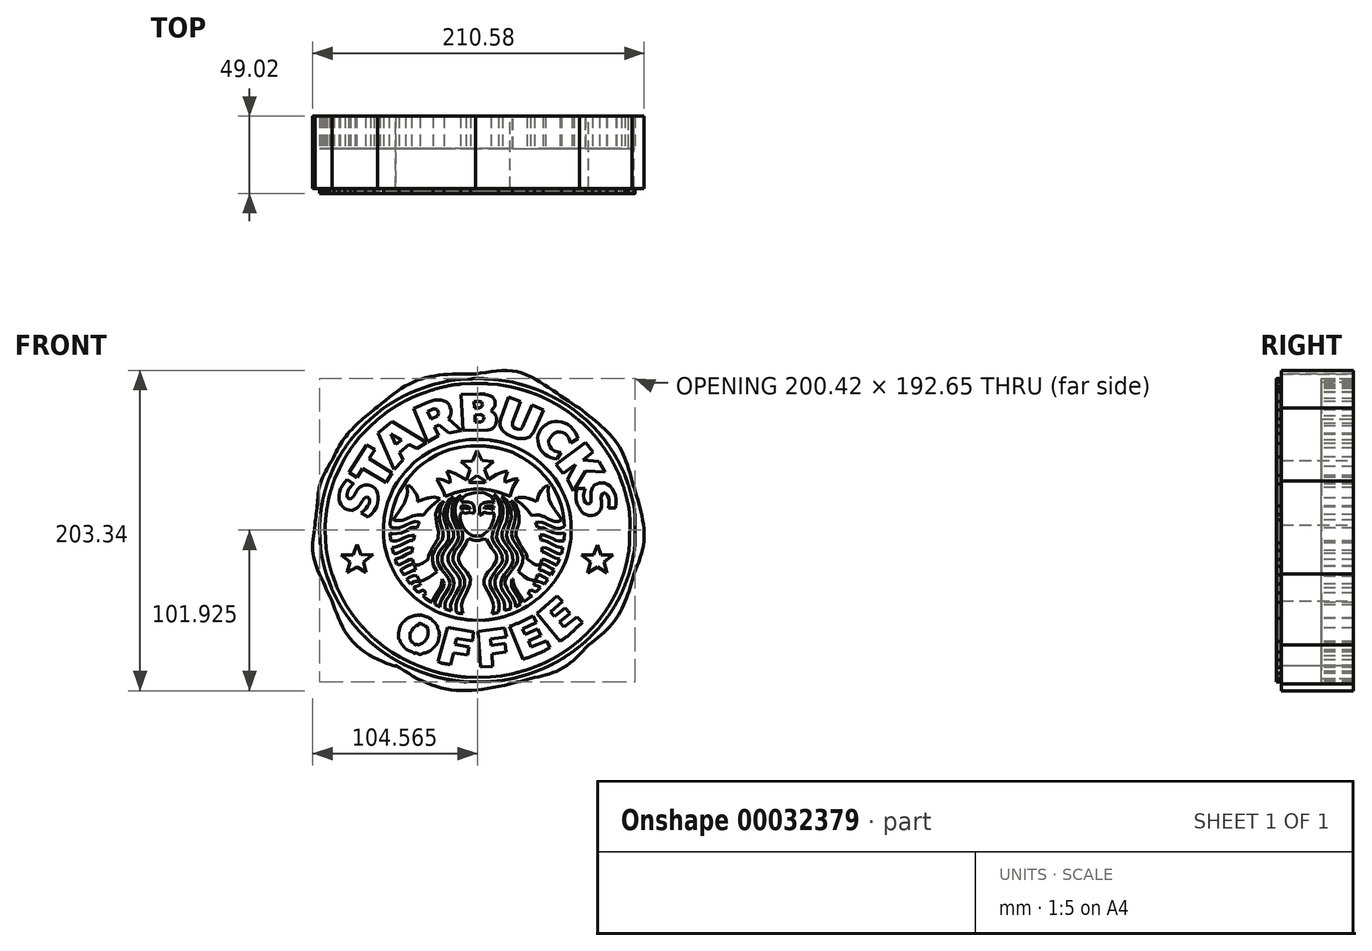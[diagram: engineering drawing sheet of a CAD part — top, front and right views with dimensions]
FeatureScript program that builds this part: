
annotation { "Feature Type Name" : "Feature", "Feature Type Description" : "" }
export const myFeature = defineFeature(function(context is Context, id is Id, definition is map)
    precondition{}
    {
        {
            var Q0;
            Q0=qCreatedBy(makeId("Front.planeOp"),FACE);
            var sketch = newSketch(context, id + "F0", { "sketchPlane" : qUnion([Q0])});
            skFitSpline(sketch, "E0", {"points": [v(-1.26, 99.12) * mm, v(25.57, 100.63) * mm, v(47.78, 88.94) * mm, v(64.86, 77.55) * mm]});
            skFitSpline(sketch, "E1", {"points": [v(64.86, 77.55) * mm, v(80.4, 64.67) * mm, v(91.74, 50.25) * mm, v(98.22, 31.18) * mm]});
            skFitSpline(sketch, "E2", {"points": [v(98.22, 31.18) * mm, v(103.53, 13.35) * mm, v(105.81, -7.15) * mm, v(99.43, -27.68) * mm]});
            skFitSpline(sketch, "E3", {"points": [v(99.43, -27.68) * mm, v(94.37, -44) * mm, v(85.73, -59.44) * mm, v(70.7, -72.73) * mm]});
            skFitSpline(sketch, "E4", {"points": [v(70.7, -72.73) * mm, v(54.04, -87.63) * mm, v(36.86, -93.5) * mm, v(20.71, -97.63) * mm]});
            skFitSpline(sketch, "E5", {"points": [v(20.71, -97.63) * mm, v(-7.45, -101.86) * mm, v(-30.33, -97.78) * mm, v(-51.96, -85.74) * mm]});
            skFitSpline(sketch, "E6", {"points": [v(-51.96, -85.74) * mm, v(-52.06, -86.04) * mm, v(-74.8, -74.8) * mm, v(-92.18, -45.02) * mm]});
            skFitSpline(sketch, "E7", {"points": [v(-92.18, -45.02) * mm, v(-99.16, -30.2) * mm, v(-104.3, -14.84) * mm, v(-103.16, 3.47) * mm]});
            skFitSpline(sketch, "E8", {"points": [v(-103.16, 3.47) * mm, v(-101.66, 16.33) * mm, v(-99.76, 29.6) * mm, v(-92.28, 44.39) * mm]});
            skFitSpline(sketch, "E9", {"points": [v(-92.28, 44.39) * mm, v(-85.03, 57.64) * mm, v(-75.05, 68.69) * mm, v(-63.25, 78.46) * mm]});
            skFitSpline(sketch, "E10", {"points": [v(-63.25, 78.46) * mm, v(-42.92, 93.13) * mm, v(-22.97, 98.67) * mm, v(-1.26, 99.12) * mm]});
            skFitSpline(sketch, "E11", {"points": [v(52.4, -70.46) * mm, v(57.54, -67.03) * mm, v(62.11, -62.8) * mm, v(66.78, -58.62) * mm]});
            skLineSegment(sketch, "E12", {"start": v(38.05, -52.88) * mm, "end": v(52.4, -70.46) * mm});
            skLineSegment(sketch, "E13", {"start": v(52.4, -70.46) * mm, "end": v(38.05, -52.88) * mm});
            skFitSpline(sketch, "E14", {"points": [v(20.45, -61.17) * mm, v(25.51, -59.1) * mm, v(30.46, -56.86) * mm, v(35.24, -54.33) * mm]});
            skLineSegment(sketch, "E15", {"start": v(66.78, -58.62) * mm, "end": v(63.35, -55) * mm});
            skLineSegment(sketch, "E16", {"start": v(63.35, -55) * mm, "end": v(55.18, -61.45) * mm});
            skLineSegment(sketch, "E17", {"start": v(55.18, -61.45) * mm, "end": v(52.36, -58.22) * mm});
            skLineSegment(sketch, "E18", {"start": v(52.36, -58.22) * mm, "end": v(59.01, -52.78) * mm});
            skLineSegment(sketch, "E19", {"start": v(59.01, -52.78) * mm, "end": v(55.81, -49.27) * mm});
            skLineSegment(sketch, "E20", {"start": v(55.81, -49.27) * mm, "end": v(49.02, -54.8) * mm});
            skLineSegment(sketch, "E21", {"start": v(49.02, -54.8) * mm, "end": v(46.52, -51.77) * mm});
            skLineSegment(sketch, "E22", {"start": v(46.52, -51.77) * mm, "end": v(54.09, -45.04) * mm});
            skLineSegment(sketch, "E23", {"start": v(54.09, -45.04) * mm, "end": v(50.65, -41.84) * mm});
            skLineSegment(sketch, "E24", {"start": v(50.65, -41.84) * mm, "end": v(38.05, -52.88) * mm});
            skLineSegment(sketch, "E25", {"start": v(38.05, -52.88) * mm, "end": v(66.78, -58.62) * mm});
            skFitSpline(sketch, "E26", {"points": [v(46.18, -74.46) * mm, v(40.49, -77.49) * mm, v(34.71, -79.84) * mm, v(28.93, -82.12) * mm]});
            skLineSegment(sketch, "E27", {"start": v(35.24, -54.33) * mm, "end": v(35.7, -54.4) * mm});
            skLineSegment(sketch, "E28", {"start": v(35.7, -54.4) * mm, "end": v(37.84, -57.92) * mm});
            skLineSegment(sketch, "E29", {"start": v(37.84, -57.92) * mm, "end": v(37.88, -58.25) * mm});
            skLineSegment(sketch, "E30", {"start": v(37.88, -58.25) * mm, "end": v(28.72, -62.63) * mm});
            skLineSegment(sketch, "E31", {"start": v(28.72, -62.63) * mm, "end": v(30.32, -66.05) * mm});
            skLineSegment(sketch, "E32", {"start": v(30.32, -66.05) * mm, "end": v(38.37, -62.6) * mm});
            skLineSegment(sketch, "E33", {"start": v(38.37, -62.6) * mm, "end": v(40.58, -66.8) * mm});
            skLineSegment(sketch, "E34", {"start": v(40.58, -66.8) * mm, "end": v(32.57, -70.3) * mm});
            skLineSegment(sketch, "E35", {"start": v(32.57, -70.3) * mm, "end": v(34.2, -74.21) * mm});
            skLineSegment(sketch, "E36", {"start": v(34.2, -74.21) * mm, "end": v(43.86, -70.18) * mm});
            skLineSegment(sketch, "E37", {"start": v(43.86, -70.18) * mm, "end": v(46.18, -74.46) * mm});
            skLineSegment(sketch, "E38", {"start": v(46.18, -74.46) * mm, "end": v(35.24, -54.33) * mm});
            skLineSegment(sketch, "E39", {"start": v(28.93, -82.12) * mm, "end": v(20.45, -61.17) * mm});
            skLineSegment(sketch, "E40", {"start": v(20.45, -61.17) * mm, "end": v(28.93, -82.12) * mm});
            skLineSegment(sketch, "E41", {"start": v(0.5, -64.16) * mm, "end": v(17.31, -62.17) * mm});
            skLineSegment(sketch, "E42", {"start": v(17.31, -62.17) * mm, "end": v(18.42, -67.69) * mm});
            skLineSegment(sketch, "E43", {"start": v(18.42, -67.69) * mm, "end": v(8.37, -69.15) * mm});
            skLineSegment(sketch, "E44", {"start": v(8.37, -69.15) * mm, "end": v(8.62, -73.03) * mm});
            skLineSegment(sketch, "E45", {"start": v(8.62, -73.03) * mm, "end": v(17.5, -71.9) * mm});
            skLineSegment(sketch, "E46", {"start": v(17.5, -71.9) * mm, "end": v(18.28, -77.24) * mm});
            skLineSegment(sketch, "E47", {"start": v(18.28, -77.24) * mm, "end": v(9.3, -78.42) * mm});
            skLineSegment(sketch, "E48", {"start": v(9.3, -78.42) * mm, "end": v(9.69, -86.4) * mm});
            skLineSegment(sketch, "E49", {"start": v(9.69, -86.4) * mm, "end": v(1.95, -86.75) * mm});
            skLineSegment(sketch, "E50", {"start": v(1.95, -86.75) * mm, "end": v(0.5, -64.16) * mm});
            skFitSpline(sketch, "E51", {"points": [v(-17.11, -85.44) * mm, v(-19.73, -84.85) * mm, v(-22.4, -84.38) * mm, v(-24.84, -83.44) * mm]});
            skLineSegment(sketch, "E52", {"start": v(-19.07, -61.56) * mm, "end": v(-2.32, -64.52) * mm});
            skLineSegment(sketch, "E53", {"start": v(-2.32, -64.52) * mm, "end": v(-3, -70.15) * mm});
            skLineSegment(sketch, "E54", {"start": v(-3, -70.15) * mm, "end": v(-13.23, -68.54) * mm});
            skLineSegment(sketch, "E55", {"start": v(-13.23, -68.54) * mm, "end": v(-14.08, -72.36) * mm});
            skLineSegment(sketch, "E56", {"start": v(-14.08, -72.36) * mm, "end": v(-5.28, -74.03) * mm});
            skLineSegment(sketch, "E57", {"start": v(-5.28, -74.03) * mm, "end": v(-6.17, -79.3) * mm});
            skLineSegment(sketch, "E58", {"start": v(-6.17, -79.3) * mm, "end": v(-15.08, -77.85) * mm});
            skLineSegment(sketch, "E59", {"start": v(-15.08, -77.85) * mm, "end": v(-17.11, -85.44) * mm});
            skLineSegment(sketch, "E60", {"start": v(-17.11, -85.44) * mm, "end": v(-19.07, -61.56) * mm});
            skFitSpline(sketch, "E61", {"points": [v(-38.45, -60.39) * mm, v(-38.66, -60.44) * mm, v(-40.27, -61.92) * mm, v(-40.32, -61.95) * mm]});
            skFitSpline(sketch, "E62", {"points": [v(-40.32, -61.95) * mm, v(-41.1, -62.57) * mm, v(-41.43, -63.51) * mm, v(-41.93, -64.37) * mm]});
            skFitSpline(sketch, "E63", {"points": [v(-41.93, -64.37) * mm, v(-42.79, -65.33) * mm, v(-42.74, -67) * mm, v(-42.69, -67.24) * mm]});
            skFitSpline(sketch, "E64", {"points": [v(-42.69, -67.24) * mm, v(-42.84, -68.64) * mm, v(-42.48, -69.28) * mm, v(-42.13, -70.06) * mm]});
            skFitSpline(sketch, "E65", {"points": [v(-42.13, -70.06) * mm, v(-41.65, -71.05) * mm, v(-40.74, -71.42) * mm, v(-40.22, -71.93) * mm]});
            skFitSpline(sketch, "E66", {"points": [v(-40.22, -71.93) * mm, v(-39.51, -72.72) * mm, v(-38.54, -72.43) * mm, v(-37.7, -72.68) * mm]});
            skFitSpline(sketch, "E67", {"points": [v(-37.7, -72.68) * mm, v(-36.96, -72.71) * mm, v(-36.14, -72.2) * mm, v(-35.58, -72.03) * mm]});
            skFitSpline(sketch, "E68", {"points": [v(-35.58, -72.03) * mm, v(-34.78, -71.65) * mm, v(-34.2, -71.06) * mm, v(-33.72, -70.72) * mm]});
            skFitSpline(sketch, "E69", {"points": [v(-33.72, -70.72) * mm, v(-32.97, -70.05) * mm, v(-32.64, -69.49) * mm, v(-32.46, -68.95) * mm]});
            skFitSpline(sketch, "E70", {"points": [v(-32.46, -68.95) * mm, v(-31.88, -68.29) * mm, v(-31.53, -67.38) * mm, v(-31.55, -67.14) * mm]});
            skFitSpline(sketch, "E71", {"points": [v(-31.55, -67.14) * mm, v(-31.25, -66.05) * mm, v(-31.24, -65.55) * mm, v(-31.3, -65.02) * mm]});
            skFitSpline(sketch, "E72", {"points": [v(-31.3, -65.02) * mm, v(-31.23, -64.28) * mm, v(-31.25, -63.34) * mm, v(-31.65, -62.86) * mm]});
            skFitSpline(sketch, "E73", {"points": [v(-31.65, -62.86) * mm, v(-31.9, -61.3) * mm, v(-33.05, -61.03) * mm, v(-33.56, -60.29) * mm]});
            skFitSpline(sketch, "E74", {"points": [v(-33.56, -60.29) * mm, v(-37.32, -59.31) * mm, v(-37.4, -60.37) * mm, v(-38.45, -60.39) * mm]});
            skLineSegment(sketch, "E75", {"start": v(-24.84, -83.44) * mm, "end": v(-19.07, -61.56) * mm});
            skLineSegment(sketch, "E76", {"start": v(-19.07, -61.56) * mm, "end": v(-24.84, -83.44) * mm});
            skFitSpline(sketch, "E77", {"points": [v(-40.82, -54.4) * mm, v(-41.9, -54.84) * mm, v(-42.77, -55.18) * mm, v(-43.8, -55.6) * mm]});
            skFitSpline(sketch, "E78", {"points": [v(-43.8, -55.6) * mm, v(-45, -56.3) * mm, v(-46.1, -57.47) * mm, v(-46.82, -58.07) * mm]});
            skFitSpline(sketch, "E79", {"points": [v(-46.82, -58.07) * mm, v(-47.5, -58.83) * mm, v(-48.6, -60.24) * mm, v(-48.88, -60.94) * mm]});
            skFitSpline(sketch, "E80", {"points": [v(-48.88, -60.94) * mm, v(-49.27, -61.9) * mm, v(-49.49, -62.95) * mm, v(-49.8, -63.97) * mm]});
            skFitSpline(sketch, "E81", {"points": [v(-49.8, -63.97) * mm, v(-49.92, -65.1) * mm, v(-49.98, -66.5) * mm, v(-49.94, -67.4) * mm]});
            skFitSpline(sketch, "E82", {"points": [v(-49.94, -67.4) * mm, v(-49.9, -68.95) * mm, v(-49.08, -69.92) * mm, v(-48.94, -70.92) * mm]});
            skFitSpline(sketch, "E83", {"points": [v(-48.94, -70.92) * mm, v(-48.3, -71.81) * mm, v(-47.7, -72.68) * mm, v(-47.22, -73.34) * mm]});
            skFitSpline(sketch, "E84", {"points": [v(-47.22, -73.34) * mm, v(-46.55, -74.1) * mm, v(-45.9, -74.77) * mm, v(-45.4, -75.3) * mm]});
            skFitSpline(sketch, "E85", {"points": [v(-45.4, -75.3) * mm, v(-43.93, -76.31) * mm, v(-42.53, -76.76) * mm, v(-41.02, -77.52) * mm]});
            skFitSpline(sketch, "E86", {"points": [v(-41.02, -77.52) * mm, v(-40.01, -78.08) * mm, v(-38.95, -78) * mm, v(-37.75, -78.28) * mm]});
            skFitSpline(sketch, "E87", {"points": [v(-37.75, -78.28) * mm, v(-36.4, -78.91) * mm, v(-34.56, -78.12) * mm, v(-33.72, -78.08) * mm]});
            skFitSpline(sketch, "E88", {"points": [v(-33.72, -78.08) * mm, v(-32.56, -77.77) * mm, v(-31.8, -77.38) * mm, v(-30.94, -77.07) * mm]});
            skFitSpline(sketch, "E89", {"points": [v(-30.94, -77.07) * mm, v(-29.98, -76.62) * mm, v(-29.2, -75.89) * mm, v(-28.63, -75.5) * mm]});
            skFitSpline(sketch, "E90", {"points": [v(-28.63, -75.5) * mm, v(-27.98, -74.72) * mm, v(-27.24, -73.97) * mm, v(-26.76, -73.44) * mm]});
            skFitSpline(sketch, "E91", {"points": [v(-26.76, -73.44) * mm, v(-26.1, -72.9) * mm, v(-25.75, -72.15) * mm, v(-25.35, -71.63) * mm]});
            skFitSpline(sketch, "E92", {"points": [v(-25.35, -71.63) * mm, v(-24.81, -70.53) * mm, v(-24.74, -69.25) * mm, v(-24.3, -68) * mm]});
            skFitSpline(sketch, "E93", {"points": [v(-24.3, -68) * mm, v(-24.4, -67.23) * mm, v(-23.8, -66.52) * mm, v(-24.3, -66.03) * mm]});
            skFitSpline(sketch, "E94", {"points": [v(-24.3, -66.03) * mm, v(-24.2, -64.6) * mm, v(-25.09, -62.38) * mm, v(-25.3, -60.94) * mm]});
            skFitSpline(sketch, "E95", {"points": [v(-25.3, -60.94) * mm, v(-25.47, -60.75) * mm, v(-26.52, -59.13) * mm, v(-27.16, -58.77) * mm]});
            skFitSpline(sketch, "E96", {"points": [v(-27.16, -58.77) * mm, v(-27.55, -57.95) * mm, v(-28.33, -57.67) * mm, v(-28.73, -57.21) * mm]});
            skFitSpline(sketch, "E97", {"points": [v(-28.73, -57.21) * mm, v(-29.65, -56.02) * mm, v(-30.05, -56.1) * mm, v(-30.74, -55.7) * mm]});
            skFitSpline(sketch, "E98", {"points": [v(-30.74, -55.7) * mm, v(-31.3, -55.06) * mm, v(-32.3, -55.05) * mm, v(-32.86, -54.7) * mm]});
            skFitSpline(sketch, "E99", {"points": [v(-32.86, -54.7) * mm, v(-33.62, -54.55) * mm, v(-34.3, -54.25) * mm, v(-35.13, -54.19) * mm]});
            skFitSpline(sketch, "E100", {"points": [v(-35.13, -54.19) * mm, v(-35.74, -53.8) * mm, v(-36.82, -54.04) * mm, v(-37.5, -53.79) * mm]});
            skFitSpline(sketch, "E101", {"points": [v(-37.5, -53.79) * mm, v(-38.92, -54.07) * mm, v(-39.58, -54.16) * mm, v(-40.82, -54.4) * mm]});
            skFitSpline(sketch, "E102", {"points": [v(-42.74, -51.32) * mm, v(-44.4, -52.08) * mm, v(-45.55, -52.66) * mm, v(-47.02, -53.38) * mm]});
            skFitSpline(sketch, "E103", {"points": [v(-47.02, -53.38) * mm, v(-47.94, -50.58) * mm, v(-49, -49.5) * mm, v(-50.65, -48.4) * mm]});
            skFitSpline(sketch, "E104", {"points": [v(-50.65, -48.4) * mm, v(-51.34, -47.59) * mm, v(-52.03, -47.77) * mm, v(-52.77, -47.44) * mm]});
            skFitSpline(sketch, "E105", {"points": [v(-52.77, -47.44) * mm, v(-53.56, -47.2) * mm, v(-54.37, -47.6) * mm, v(-55.23, -47.54) * mm]});
            skFitSpline(sketch, "E106", {"points": [v(-55.23, -47.54) * mm, v(-57.59, -48.17) * mm, v(-58.26, -49.4) * mm, v(-59.52, -50.26) * mm]});
            skFitSpline(sketch, "E107", {"points": [v(-59.52, -50.26) * mm, v(-61.02, -52.3) * mm, v(-60.88, -54.45) * mm, v(-60.07, -56.76) * mm]});
            skFitSpline(sketch, "E108", {"points": [v(-60.07, -56.76) * mm, v(-58.02, -60.05) * mm, v(-56.12, -59.45) * mm, v(-52.87, -60.44) * mm]});
            skFitSpline(sketch, "E109", {"points": [v(-54.63, -64.62) * mm, v(-54.02, -63.49) * mm, v(-52.8, -62.16) * mm, v(-52.41, -60.49) * mm]});
            skFitSpline(sketch, "E110", {"points": [v(-52.41, -60.49) * mm, v(-52.7, -60.51) * mm, v(-52.75, -60.4) * mm, v(-52.97, -60.34) * mm]});
            skLineSegment(sketch, "E111", {"start": v(-54.58, -64.82) * mm, "end": v(-54.58, -64.87) * mm});
            skFitSpline(sketch, "E112", {"points": [v(-57.35, -64.62) * mm, v(-59.72, -64.06) * mm, v(-61.79, -62.53) * mm, v(-63.6, -61.7) * mm]});
            skFitSpline(sketch, "E113", {"points": [v(-63.6, -61.7) * mm, v(-65.22, -60.15) * mm, v(-66.07, -58.44) * mm, v(-67.08, -56.96) * mm]});
            skFitSpline(sketch, "E114", {"points": [v(-67.08, -56.96) * mm, v(-67.51, -55.42) * mm, v(-67.7, -53.78) * mm, v(-67.73, -52.22) * mm]});
            skFitSpline(sketch, "E115", {"points": [v(-67.73, -52.22) * mm, v(-68.14, -50.5) * mm, v(-66.5, -46.73) * mm, v(-66.57, -47.39) * mm]});
            skFitSpline(sketch, "E116", {"points": [v(-66.57, -47.39) * mm, v(-65.76, -45.58) * mm, v(-64.45, -44.13) * mm, v(-62.9, -43.05) * mm]});
            skFitSpline(sketch, "E117", {"points": [v(-62.9, -43.05) * mm, v(-61.36, -41.63) * mm, v(-59.65, -41.36) * mm, v(-57.6, -40.93) * mm]});
            skFitSpline(sketch, "E118", {"points": [v(-57.6, -40.93) * mm, v(-55.6, -40.78) * mm, v(-53.72, -41.12) * mm, v(-51.9, -41.29) * mm]});
            skFitSpline(sketch, "E119", {"points": [v(-51.9, -41.29) * mm, v(-50.48, -41.91) * mm, v(-48.93, -42.81) * mm, v(-47.68, -43.45) * mm]});
            skFitSpline(sketch, "E120", {"points": [v(-47.68, -43.45) * mm, v(-45.8, -44.76) * mm, v(-44.8, -46.06) * mm, v(-44.15, -47.54) * mm]});
            skFitSpline(sketch, "E121", {"points": [v(-44.15, -47.54) * mm, v(-42.6, -48.51) * mm, v(-42.87, -51.05) * mm, v(-42.48, -51.16) * mm]});
            skFitSpline(sketch, "E122", {"points": [v(-81.34, 36.63) * mm, v(-77.63, 42.83) * mm, v(-73.92, 48.68) * mm, v(-70.2, 54.21) * mm]});
            skLineSegment(sketch, "E123", {"start": v(-54.58, -64.72) * mm, "end": v(-57.35, -64.62) * mm});
            skLineSegment(sketch, "E124", {"start": v(-70.2, 54.21) * mm, "end": v(-65.06, 51.3) * mm});
            skLineSegment(sketch, "E125", {"start": v(-65.06, 51.3) * mm, "end": v(-68.64, 45.55) * mm});
            skLineSegment(sketch, "E126", {"start": v(-68.64, 45.55) * mm, "end": v(-54.18, 36.42) * mm});
            skLineSegment(sketch, "E127", {"start": v(-54.18, 36.42) * mm, "end": v(-58.06, 30.33) * mm});
            skLineSegment(sketch, "E128", {"start": v(-58.06, 30.33) * mm, "end": v(-72.82, 39.25) * mm});
            skLineSegment(sketch, "E129", {"start": v(-72.82, 39.25) * mm, "end": v(-76.45, 33.65) * mm});
            skLineSegment(sketch, "E130", {"start": v(-76.45, 33.65) * mm, "end": v(-81.34, 36.63) * mm});
            skLineSegment(sketch, "E131", {"start": v(-81.34, 36.63) * mm, "end": v(-70.2, 54.21) * mm});
            skLineSegment(sketch, "E132", {"start": v(-62.9, 61.77) * mm, "end": v(-54.08, 69.03) * mm});
            skLineSegment(sketch, "E133", {"start": v(-54.08, 69.03) * mm, "end": v(-32.25, 55.88) * mm});
            skLineSegment(sketch, "E134", {"start": v(-32.25, 55.88) * mm, "end": v(-38.4, 51.9) * mm});
            skLineSegment(sketch, "E135", {"start": v(-38.4, 51.9) * mm, "end": v(-43.2, 54.37) * mm});
            skLineSegment(sketch, "E136", {"start": v(-43.2, 54.37) * mm, "end": v(-49.29, 49.33) * mm});
            skLineSegment(sketch, "E137", {"start": v(-49.29, 49.33) * mm, "end": v(-47.17, 44.59) * mm});
            skLineSegment(sketch, "E138", {"start": v(-47.17, 44.59) * mm, "end": v(-52.92, 38.6) * mm});
            skLineSegment(sketch, "E139", {"start": v(-52.92, 38.6) * mm, "end": v(-62.9, 61.77) * mm});
            skFitSpline(sketch, "E140", {"points": [v(68.8, 55.73) * mm, v(62.47, 51.53) * mm, v(56.28, 46.79) * mm, v(50.1, 41.92) * mm]});
            skLineSegment(sketch, "E141", {"start": v(-54.78, 61.27) * mm, "end": v(-51.9, 54.62) * mm});
            skLineSegment(sketch, "E142", {"start": v(-51.9, 54.62) * mm, "end": v(-48.18, 57.39) * mm});
            skLineSegment(sketch, "E143", {"start": v(-48.18, 57.39) * mm, "end": v(-54.78, 61.27) * mm});
            skLineSegment(sketch, "E144", {"start": v(50.1, 41.92) * mm, "end": v(54.48, 36.22) * mm});
            skLineSegment(sketch, "E145", {"start": v(54.48, 36.22) * mm, "end": v(62.24, 41.67) * mm});
            skLineSegment(sketch, "E146", {"start": v(62.24, 41.67) * mm, "end": v(57.2, 32.14) * mm});
            skLineSegment(sketch, "E147", {"start": v(57.2, 32.14) * mm, "end": v(61.13, 25.09) * mm});
            skLineSegment(sketch, "E148", {"start": v(61.13, 25.09) * mm, "end": v(68.84, 37.74) * mm});
            skLineSegment(sketch, "E149", {"start": v(68.84, 37.74) * mm, "end": v(81.24, 36.93) * mm});
            skLineSegment(sketch, "E150", {"start": v(81.24, 36.93) * mm, "end": v(77.36, 43.63) * mm});
            skLineSegment(sketch, "E151", {"start": v(77.36, 43.63) * mm, "end": v(66.98, 44.69) * mm});
            skLineSegment(sketch, "E152", {"start": v(66.98, 44.69) * mm, "end": v(73.63, 49.83) * mm});
            skLineSegment(sketch, "E153", {"start": v(73.63, 49.83) * mm, "end": v(68.8, 55.73) * mm});
            skLineSegment(sketch, "E154", {"start": v(68.8, 55.73) * mm, "end": v(50.1, 41.92) * mm});
            skLineSegment(sketch, "E155", {"start": v(76.4, -9.18) * mm, "end": v(73.73, -15.58) * mm});
            skLineSegment(sketch, "E156", {"start": v(73.73, -15.58) * mm, "end": v(66.12, -15.79) * mm});
            skLineSegment(sketch, "E157", {"start": v(66.12, -15.79) * mm, "end": v(71.92, -20.17) * mm});
            skLineSegment(sketch, "E158", {"start": v(71.92, -20.17) * mm, "end": v(69.9, -26.97) * mm});
            skLineSegment(sketch, "E159", {"start": v(69.9, -26.97) * mm, "end": v(76.25, -23.3) * mm});
            skLineSegment(sketch, "E160", {"start": v(76.25, -23.3) * mm, "end": v(82.25, -27.18) * mm});
            skLineSegment(sketch, "E161", {"start": v(82.25, -27.18) * mm, "end": v(80.43, -20.12) * mm});
            skLineSegment(sketch, "E162", {"start": v(80.43, -20.12) * mm, "end": v(86.18, -15.53) * mm});
            skLineSegment(sketch, "E163", {"start": v(86.18, -15.53) * mm, "end": v(78.67, -15.58) * mm});
            skLineSegment(sketch, "E164", {"start": v(78.67, -15.58) * mm, "end": v(76.4, -9.18) * mm});
            skLineSegment(sketch, "E165", {"start": v(-76.4, -9.03) * mm, "end": v(-78.97, -15.69) * mm});
            skLineSegment(sketch, "E166", {"start": v(-78.97, -15.69) * mm, "end": v(-86.63, -15.64) * mm});
            skLineSegment(sketch, "E167", {"start": v(-86.63, -15.64) * mm, "end": v(-80.74, -20.12) * mm});
            skLineSegment(sketch, "E168", {"start": v(-80.74, -20.12) * mm, "end": v(-82.7, -26.92) * mm});
            skLineSegment(sketch, "E169", {"start": v(-82.7, -26.92) * mm, "end": v(-76.45, -23.4) * mm});
            skLineSegment(sketch, "E170", {"start": v(-76.45, -23.4) * mm, "end": v(-70.56, -26.92) * mm});
            skLineSegment(sketch, "E171", {"start": v(-70.56, -26.92) * mm, "end": v(-72.22, -20.07) * mm});
            skLineSegment(sketch, "E172", {"start": v(-72.22, -20.07) * mm, "end": v(-66.37, -15.48) * mm});
            skLineSegment(sketch, "E173", {"start": v(-66.37, -15.48) * mm, "end": v(-73.78, -15.53) * mm});
            skLineSegment(sketch, "E174", {"start": v(-73.78, -15.53) * mm, "end": v(-76.4, -9.03) * mm});
            skFitSpline(sketch, "E175", {"points": [v(-75.13, 15.41) * mm, v(-74.72, 15.99) * mm, v(-74.33, 16.57) * mm, v(-73.95, 17.16) * mm]});
            skFitSpline(sketch, "E176", {"points": [v(-73.95, 17.16) * mm, v(-73.6, 17.71) * mm, v(-73.25, 18.27) * mm, v(-72.92, 18.84) * mm]});
            skLineSegment(sketch, "E177", {"start": v(-82.6, 32.13) * mm, "end": v(-84.25, 30.49) * mm});
            skLineSegment(sketch, "E178", {"start": v(-84.25, 30.49) * mm, "end": v(-85.7, 28.6) * mm});
            skLineSegment(sketch, "E179", {"start": v(-85.7, 28.6) * mm, "end": v(-86.7, 26.5) * mm});
            skLineSegment(sketch, "E180", {"start": v(-86.7, 26.5) * mm, "end": v(-87.42, 24.47) * mm});
            skLineSegment(sketch, "E181", {"start": v(-87.42, 24.47) * mm, "end": v(-87.78, 22.33) * mm});
            skLineSegment(sketch, "E182", {"start": v(-87.78, 22.33) * mm, "end": v(-87.74, 19.73) * mm});
            skLineSegment(sketch, "E183", {"start": v(-87.74, 19.73) * mm, "end": v(-87.5, 18.12) * mm});
            skLineSegment(sketch, "E184", {"start": v(-87.5, 18.12) * mm, "end": v(-86.64, 16.38) * mm});
            skLineSegment(sketch, "E185", {"start": v(-86.64, 16.38) * mm, "end": v(-85.57, 14.99) * mm});
            skLineSegment(sketch, "E186", {"start": v(-85.57, 14.99) * mm, "end": v(-84.32, 13.88) * mm});
            skLineSegment(sketch, "E187", {"start": v(-84.32, 13.88) * mm, "end": v(-82.86, 13.13) * mm});
            skLineSegment(sketch, "E188", {"start": v(-82.86, 13.13) * mm, "end": v(-81.33, 12.78) * mm});
            skLineSegment(sketch, "E189", {"start": v(-81.33, 12.78) * mm, "end": v(-79.69, 12.7) * mm});
            skLineSegment(sketch, "E190", {"start": v(-79.69, 12.7) * mm, "end": v(-78.15, 13.2) * mm});
            skLineSegment(sketch, "E191", {"start": v(-78.15, 13.2) * mm, "end": v(-76.48, 14.13) * mm});
            skLineSegment(sketch, "E192", {"start": v(-76.48, 14.13) * mm, "end": v(-75.13, 15.41) * mm});
            skFitSpline(sketch, "E193", {"points": [v(-76.87, 24.6) * mm, v(-77.11, 24.13) * mm, v(-77.36, 23.65) * mm, v(-77.62, 23.18) * mm]});
            skFitSpline(sketch, "E194", {"points": [v(-77.62, 23.18) * mm, v(-77.96, 22.56) * mm, v(-78.32, 21.94) * mm, v(-78.69, 21.33) * mm]});
            skLineSegment(sketch, "E195", {"start": v(-72.92, 18.84) * mm, "end": v(-71.85, 20.26) * mm});
            skLineSegment(sketch, "E196", {"start": v(-71.85, 20.26) * mm, "end": v(-70.92, 20.94) * mm});
            skLineSegment(sketch, "E197", {"start": v(-70.92, 20.94) * mm, "end": v(-70.14, 21.12) * mm});
            skLineSegment(sketch, "E198", {"start": v(-70.14, 21.12) * mm, "end": v(-69.25, 20.9) * mm});
            skLineSegment(sketch, "E199", {"start": v(-69.25, 20.9) * mm, "end": v(-68.85, 20.33) * mm});
            skLineSegment(sketch, "E200", {"start": v(-68.85, 20.33) * mm, "end": v(-68.43, 19.26) * mm});
            skLineSegment(sketch, "E201", {"start": v(-68.43, 19.26) * mm, "end": v(-68.46, 17.98) * mm});
            skLineSegment(sketch, "E202", {"start": v(-68.46, 17.98) * mm, "end": v(-68.89, 16.63) * mm});
            skLineSegment(sketch, "E203", {"start": v(-68.89, 16.63) * mm, "end": v(-69.57, 15.38) * mm});
            skLineSegment(sketch, "E204", {"start": v(-69.57, 15.38) * mm, "end": v(-70.64, 13.95) * mm});
            skLineSegment(sketch, "E205", {"start": v(-70.64, 13.95) * mm, "end": v(-71.7, 12.88) * mm});
            skLineSegment(sketch, "E206", {"start": v(-71.7, 12.88) * mm, "end": v(-73.84, 11.07) * mm});
            skLineSegment(sketch, "E207", {"start": v(-73.84, 11.07) * mm, "end": v(-69.28, 8.47) * mm});
            skLineSegment(sketch, "E208", {"start": v(-69.28, 8.47) * mm, "end": v(-67.86, 9.64) * mm});
            skLineSegment(sketch, "E209", {"start": v(-67.86, 9.64) * mm, "end": v(-66.79, 10.75) * mm});
            skLineSegment(sketch, "E210", {"start": v(-66.79, 10.75) * mm, "end": v(-65.54, 12.31) * mm});
            skLineSegment(sketch, "E211", {"start": v(-65.54, 12.31) * mm, "end": v(-64.58, 13.92) * mm});
            skLineSegment(sketch, "E212", {"start": v(-64.58, 13.92) * mm, "end": v(-63.83, 15.6) * mm});
            skLineSegment(sketch, "E213", {"start": v(-63.83, 15.6) * mm, "end": v(-63.3, 17.4) * mm});
            skLineSegment(sketch, "E214", {"start": v(-63.3, 17.4) * mm, "end": v(-63, 19.37) * mm});
            skLineSegment(sketch, "E215", {"start": v(-63, 19.37) * mm, "end": v(-62.94, 21.33) * mm});
            skLineSegment(sketch, "E216", {"start": v(-62.94, 21.33) * mm, "end": v(-63.26, 23.47) * mm});
            skLineSegment(sketch, "E217", {"start": v(-63.26, 23.47) * mm, "end": v(-63.97, 25.32) * mm});
            skLineSegment(sketch, "E218", {"start": v(-63.97, 25.32) * mm, "end": v(-65.08, 26.64) * mm});
            skLineSegment(sketch, "E219", {"start": v(-65.08, 26.64) * mm, "end": v(-66.4, 27.7) * mm});
            skLineSegment(sketch, "E220", {"start": v(-66.4, 27.7) * mm, "end": v(-68.1, 28.46) * mm});
            skLineSegment(sketch, "E221", {"start": v(-68.1, 28.46) * mm, "end": v(-69.25, 28.74) * mm});
            skLineSegment(sketch, "E222", {"start": v(-69.25, 28.74) * mm, "end": v(-71.74, 28.67) * mm});
            skLineSegment(sketch, "E223", {"start": v(-71.74, 28.67) * mm, "end": v(-73.13, 28.28) * mm});
            skLineSegment(sketch, "E224", {"start": v(-73.13, 28.28) * mm, "end": v(-74.48, 27.42) * mm});
            skLineSegment(sketch, "E225", {"start": v(-74.48, 27.42) * mm, "end": v(-75.66, 26.25) * mm});
            skLineSegment(sketch, "E226", {"start": v(-75.66, 26.25) * mm, "end": v(-76.87, 24.6) * mm});
            skFitSpline(sketch, "E227", {"points": [v(-80.33, 27.82) * mm, v(-79.94, 28.21) * mm, v(-79.54, 28.6) * mm, v(-79.12, 28.96) * mm]});
            skFitSpline(sketch, "E228", {"points": [v(-79.12, 28.96) * mm, v(-78.96, 29.09) * mm, v(-78.81, 29.22) * mm, v(-78.65, 29.35) * mm]});
            skLineSegment(sketch, "E229", {"start": v(-78.69, 21.33) * mm, "end": v(-80.11, 20.22) * mm});
            skLineSegment(sketch, "E230", {"start": v(-80.11, 20.22) * mm, "end": v(-80.97, 20.01) * mm});
            skLineSegment(sketch, "E231", {"start": v(-80.97, 20.01) * mm, "end": v(-81.79, 20.12) * mm});
            skLineSegment(sketch, "E232", {"start": v(-81.79, 20.12) * mm, "end": v(-82.43, 20.94) * mm});
            skLineSegment(sketch, "E233", {"start": v(-82.43, 20.94) * mm, "end": v(-82.68, 21.8) * mm});
            skLineSegment(sketch, "E234", {"start": v(-82.68, 21.8) * mm, "end": v(-82.65, 22.83) * mm});
            skLineSegment(sketch, "E235", {"start": v(-82.65, 22.83) * mm, "end": v(-82.54, 23.9) * mm});
            skLineSegment(sketch, "E236", {"start": v(-82.54, 23.9) * mm, "end": v(-82.04, 25.43) * mm});
            skLineSegment(sketch, "E237", {"start": v(-82.04, 25.43) * mm, "end": v(-81.4, 26.57) * mm});
            skLineSegment(sketch, "E238", {"start": v(-81.4, 26.57) * mm, "end": v(-80.33, 27.82) * mm});
            skLineSegment(sketch, "E239", {"start": v(-78.65, 29.35) * mm, "end": v(-82.6, 32.13) * mm});
            skLineSegment(sketch, "E240", {"start": v(-18.29, 70.8) * mm, "end": v(-9.91, 63.34) * mm});
            skLineSegment(sketch, "E241", {"start": v(-9.91, 63.34) * mm, "end": v(-18.04, 61.74) * mm});
            skLineSegment(sketch, "E242", {"start": v(-18.04, 61.74) * mm, "end": v(-24.34, 66.94) * mm});
            skLineSegment(sketch, "E243", {"start": v(-24.34, 66.94) * mm, "end": v(-27.16, 65.7) * mm});
            skLineSegment(sketch, "E244", {"start": v(-27.16, 65.7) * mm, "end": v(-24.45, 60.07) * mm});
            skLineSegment(sketch, "E245", {"start": v(-24.45, 60.07) * mm, "end": v(-31.58, 56.22) * mm});
            skLineSegment(sketch, "E246", {"start": v(-31.58, 56.22) * mm, "end": v(-40.56, 77.42) * mm});
            skLineSegment(sketch, "E247", {"start": v(-40.56, 77.42) * mm, "end": v(-31.08, 81.41) * mm});
            skLineSegment(sketch, "E248", {"start": v(-31.08, 81.41) * mm, "end": v(-29.01, 82.12) * mm});
            skLineSegment(sketch, "E249", {"start": v(-29.01, 82.12) * mm, "end": v(-27.12, 82.62) * mm});
            skLineSegment(sketch, "E250", {"start": v(-27.12, 82.62) * mm, "end": v(-25.6, 82.73) * mm});
            skLineSegment(sketch, "E251", {"start": v(-25.6, 82.73) * mm, "end": v(-23.1, 82.73) * mm});
            skLineSegment(sketch, "E252", {"start": v(-23.1, 82.73) * mm, "end": v(-21.07, 82.23) * mm});
            skLineSegment(sketch, "E253", {"start": v(-21.07, 82.23) * mm, "end": v(-19.53, 81.41) * mm});
            skLineSegment(sketch, "E254", {"start": v(-19.53, 81.41) * mm, "end": v(-18.36, 80.34) * mm});
            skLineSegment(sketch, "E255", {"start": v(-18.36, 80.34) * mm, "end": v(-17.6, 79.13) * mm});
            skLineSegment(sketch, "E256", {"start": v(-17.6, 79.13) * mm, "end": v(-17.18, 77.85) * mm});
            skLineSegment(sketch, "E257", {"start": v(-17.18, 77.85) * mm, "end": v(-16.72, 76.32) * mm});
            skLineSegment(sketch, "E258", {"start": v(-16.72, 76.32) * mm, "end": v(-16.72, 74.53) * mm});
            skLineSegment(sketch, "E259", {"start": v(-16.72, 74.53) * mm, "end": v(-17.04, 73.14) * mm});
            skLineSegment(sketch, "E260", {"start": v(-17.04, 73.14) * mm, "end": v(-17.22, 72.43) * mm});
            skLineSegment(sketch, "E261", {"start": v(-17.22, 72.43) * mm, "end": v(-18.29, 70.8) * mm});
            skLineSegment(sketch, "E262", {"start": v(-25.24, 72.47) * mm, "end": v(-29.51, 70.83) * mm});
            skLineSegment(sketch, "E263", {"start": v(-29.51, 70.83) * mm, "end": v(-31.65, 75.35) * mm});
            skLineSegment(sketch, "E264", {"start": v(-31.65, 75.35) * mm, "end": v(-28.02, 76.92) * mm});
            skLineSegment(sketch, "E265", {"start": v(-28.02, 76.92) * mm, "end": v(-26.73, 77.14) * mm});
            skLineSegment(sketch, "E266", {"start": v(-26.73, 77.14) * mm, "end": v(-25.56, 76.6) * mm});
            skLineSegment(sketch, "E267", {"start": v(-25.56, 76.6) * mm, "end": v(-24.8, 75.5) * mm});
            skLineSegment(sketch, "E268", {"start": v(-24.8, 75.5) * mm, "end": v(-24.6, 74.46) * mm});
            skLineSegment(sketch, "E269", {"start": v(-24.6, 74.46) * mm, "end": v(-24.8, 73.32) * mm});
            skLineSegment(sketch, "E270", {"start": v(-24.8, 73.32) * mm, "end": v(-25.24, 72.47) * mm});
            skFitSpline(sketch, "E271", {"points": [v(8.33, 85.4) * mm, v(7.76, 85.57) * mm, v(7.2, 85.74) * mm, v(6.62, 85.9) * mm]});
            skFitSpline(sketch, "E272", {"points": [v(6.62, 85.9) * mm, v(6.05, 86.07) * mm, v(5.48, 86.23) * mm, v(4.91, 86.4) * mm]});
            skFitSpline(sketch, "E273", {"points": [v(4.91, 86.4) * mm, v(4.32, 86.44) * mm, v(3.72, 86.48) * mm, v(3.13, 86.5) * mm]});
            skFitSpline(sketch, "E274", {"points": [v(3.13, 86.5) * mm, v(2.51, 86.54) * mm, v(1.9, 86.56) * mm, v(1.28, 86.58) * mm]});
            skLineSegment(sketch, "E275", {"start": v(1.28, 86.58) * mm, "end": v(-10.27, 86.15) * mm});
            skLineSegment(sketch, "E276", {"start": v(-10.27, 86.15) * mm, "end": v(-9.2, 63.49) * mm});
            skLineSegment(sketch, "E277", {"start": v(-9.2, 63.49) * mm, "end": v(6.87, 63.8) * mm});
            skLineSegment(sketch, "E278", {"start": v(6.87, 63.8) * mm, "end": v(8.37, 64.13) * mm});
            skLineSegment(sketch, "E279", {"start": v(8.37, 64.13) * mm, "end": v(9.55, 64.8) * mm});
            skLineSegment(sketch, "E280", {"start": v(9.55, 64.8) * mm, "end": v(10.61, 65.7) * mm});
            skLineSegment(sketch, "E281", {"start": v(10.61, 65.7) * mm, "end": v(11.47, 66.87) * mm});
            skLineSegment(sketch, "E282", {"start": v(11.47, 66.87) * mm, "end": v(12.04, 68.05) * mm});
            skLineSegment(sketch, "E283", {"start": v(12.04, 68.05) * mm, "end": v(12.32, 69.44) * mm});
            skLineSegment(sketch, "E284", {"start": v(12.32, 69.44) * mm, "end": v(12.32, 70.58) * mm});
            skLineSegment(sketch, "E285", {"start": v(12.32, 70.58) * mm, "end": v(12.22, 71.83) * mm});
            skLineSegment(sketch, "E286", {"start": v(12.22, 71.83) * mm, "end": v(11.68, 73.04) * mm});
            skLineSegment(sketch, "E287", {"start": v(11.68, 73.04) * mm, "end": v(10.86, 74.1) * mm});
            skLineSegment(sketch, "E288", {"start": v(10.86, 74.1) * mm, "end": v(9.83, 75) * mm});
            skLineSegment(sketch, "E289", {"start": v(9.83, 75) * mm, "end": v(8.76, 75.75) * mm});
            skLineSegment(sketch, "E290", {"start": v(8.76, 75.75) * mm, "end": v(9.83, 76.89) * mm});
            skLineSegment(sketch, "E291", {"start": v(9.83, 76.89) * mm, "end": v(10.65, 78.1) * mm});
            skLineSegment(sketch, "E292", {"start": v(10.65, 78.1) * mm, "end": v(11.15, 79.3) * mm});
            skLineSegment(sketch, "E293", {"start": v(11.15, 79.3) * mm, "end": v(11.33, 80.49) * mm});
            skLineSegment(sketch, "E294", {"start": v(11.33, 80.49) * mm, "end": v(11.18, 82.16) * mm});
            skLineSegment(sketch, "E295", {"start": v(11.18, 82.16) * mm, "end": v(10.69, 83.37) * mm});
            skLineSegment(sketch, "E296", {"start": v(10.69, 83.37) * mm, "end": v(9.65, 84.65) * mm});
            skLineSegment(sketch, "E297", {"start": v(9.65, 84.65) * mm, "end": v(8.33, 85.4) * mm});
            skLineSegment(sketch, "E298", {"start": v(-2.04, 81.8) * mm, "end": v(-1.86, 77.78) * mm});
            skLineSegment(sketch, "E299", {"start": v(-1.86, 77.78) * mm, "end": v(1.2, 77.81) * mm});
            skLineSegment(sketch, "E300", {"start": v(1.2, 77.81) * mm, "end": v(2.31, 78.2) * mm});
            skLineSegment(sketch, "E301", {"start": v(2.31, 78.2) * mm, "end": v(3.1, 78.88) * mm});
            skLineSegment(sketch, "E302", {"start": v(3.1, 78.88) * mm, "end": v(3.17, 79.77) * mm});
            skLineSegment(sketch, "E303", {"start": v(3.17, 79.77) * mm, "end": v(3.13, 80.6) * mm});
            skLineSegment(sketch, "E304", {"start": v(3.13, 80.6) * mm, "end": v(2.74, 81.45) * mm});
            skLineSegment(sketch, "E305", {"start": v(2.74, 81.45) * mm, "end": v(1.67, 81.88) * mm});
            skLineSegment(sketch, "E306", {"start": v(1.67, 81.88) * mm, "end": v(-2.04, 81.8) * mm});
            skLineSegment(sketch, "E307", {"start": v(-1.4, 73.22) * mm, "end": v(-1.32, 68.76) * mm});
            skLineSegment(sketch, "E308", {"start": v(-1.32, 68.76) * mm, "end": v(2.35, 68.94) * mm});
            skLineSegment(sketch, "E309", {"start": v(2.35, 68.94) * mm, "end": v(3.24, 69.3) * mm});
            skLineSegment(sketch, "E310", {"start": v(3.24, 69.3) * mm, "end": v(4.1, 70.3) * mm});
            skLineSegment(sketch, "E311", {"start": v(4.1, 70.3) * mm, "end": v(4.16, 72.11) * mm});
            skLineSegment(sketch, "E312", {"start": v(4.16, 72.11) * mm, "end": v(3.45, 72.9) * mm});
            skLineSegment(sketch, "E313", {"start": v(3.45, 72.9) * mm, "end": v(2.17, 73.4) * mm});
            skLineSegment(sketch, "E314", {"start": v(2.17, 73.4) * mm, "end": v(-1.4, 73.22) * mm});
            skLineSegment(sketch, "E315", {"start": v(22.52, 68.51) * mm, "end": v(27.58, 81.91) * mm});
            skLineSegment(sketch, "E316", {"start": v(27.58, 81.91) * mm, "end": v(19.84, 84.55) * mm});
            skLineSegment(sketch, "E317", {"start": v(19.84, 84.55) * mm, "end": v(14.82, 70.5) * mm});
            skLineSegment(sketch, "E318", {"start": v(14.82, 70.5) * mm, "end": v(14.57, 68.87) * mm});
            skLineSegment(sketch, "E319", {"start": v(14.57, 68.87) * mm, "end": v(14.57, 66.23) * mm});
            skLineSegment(sketch, "E320", {"start": v(14.57, 66.23) * mm, "end": v(16.07, 63.52) * mm});
            skLineSegment(sketch, "E321", {"start": v(16.07, 63.52) * mm, "end": v(18.6, 61.28) * mm});
            skLineSegment(sketch, "E322", {"start": v(18.6, 61.28) * mm, "end": v(21.7, 59.46) * mm});
            skLineSegment(sketch, "E323", {"start": v(21.7, 59.46) * mm, "end": v(25.47, 58.43) * mm});
            skLineSegment(sketch, "E324", {"start": v(25.47, 58.43) * mm, "end": v(30.43, 58.32) * mm});
            skLineSegment(sketch, "E325", {"start": v(30.43, 58.32) * mm, "end": v(33.31, 59.35) * mm});
            skLineSegment(sketch, "E326", {"start": v(33.31, 59.35) * mm, "end": v(35.38, 61.88) * mm});
            skLineSegment(sketch, "E327", {"start": v(35.38, 61.88) * mm, "end": v(36.98, 64.95) * mm});
            skLineSegment(sketch, "E328", {"start": v(36.98, 64.95) * mm, "end": v(41.97, 76.53) * mm});
            skLineSegment(sketch, "E329", {"start": v(41.97, 76.53) * mm, "end": v(34.85, 79.67) * mm});
            skLineSegment(sketch, "E330", {"start": v(34.85, 79.67) * mm, "end": v(29.75, 67.73) * mm});
            skLineSegment(sketch, "E331", {"start": v(29.75, 67.73) * mm, "end": v(28.72, 65.7) * mm});
            skLineSegment(sketch, "E332", {"start": v(28.72, 65.7) * mm, "end": v(27.65, 64.27) * mm});
            skLineSegment(sketch, "E333", {"start": v(27.65, 64.27) * mm, "end": v(26.04, 64.1) * mm});
            skLineSegment(sketch, "E334", {"start": v(26.04, 64.1) * mm, "end": v(24.23, 64.66) * mm});
            skLineSegment(sketch, "E335", {"start": v(24.23, 64.66) * mm, "end": v(22.84, 65.55) * mm});
            skLineSegment(sketch, "E336", {"start": v(22.84, 65.55) * mm, "end": v(22.34, 66.84) * mm});
            skLineSegment(sketch, "E337", {"start": v(22.34, 66.84) * mm, "end": v(22.52, 68.51) * mm});
            skLineSegment(sketch, "E338", {"start": v(63.89, 58.28) * mm, "end": v(59.22, 55.58) * mm});
            skLineSegment(sketch, "E339", {"start": v(59.22, 55.58) * mm, "end": v(58.62, 57.43) * mm});
            skLineSegment(sketch, "E340", {"start": v(58.62, 57.43) * mm, "end": v(57.9, 58.89) * mm});
            skLineSegment(sketch, "E341", {"start": v(57.9, 58.89) * mm, "end": v(57.05, 60.14) * mm});
            skLineSegment(sketch, "E342", {"start": v(57.05, 60.14) * mm, "end": v(55.66, 61.35) * mm});
            skLineSegment(sketch, "E343", {"start": v(55.66, 61.35) * mm, "end": v(54.2, 62.17) * mm});
            skLineSegment(sketch, "E344", {"start": v(54.2, 62.17) * mm, "end": v(52.52, 62.49) * mm});
            skLineSegment(sketch, "E345", {"start": v(52.52, 62.49) * mm, "end": v(50.67, 62.38) * mm});
            skLineSegment(sketch, "E346", {"start": v(50.67, 62.38) * mm, "end": v(48.82, 61.53) * mm});
            skLineSegment(sketch, "E347", {"start": v(48.82, 61.53) * mm, "end": v(47.43, 60.35) * mm});
            skLineSegment(sketch, "E348", {"start": v(47.43, 60.35) * mm, "end": v(46.36, 59) * mm});
            skLineSegment(sketch, "E349", {"start": v(46.36, 59) * mm, "end": v(45.57, 57.57) * mm});
            skLineSegment(sketch, "E350", {"start": v(45.57, 57.57) * mm, "end": v(45.32, 56.32) * mm});
            skLineSegment(sketch, "E351", {"start": v(45.32, 56.32) * mm, "end": v(45.43, 54.61) * mm});
            skLineSegment(sketch, "E352", {"start": v(45.43, 54.61) * mm, "end": v(46.21, 53.15) * mm});
            skLineSegment(sketch, "E353", {"start": v(46.21, 53.15) * mm, "end": v(47.18, 51.66) * mm});
            skLineSegment(sketch, "E354", {"start": v(47.18, 51.66) * mm, "end": v(48.89, 50.48) * mm});
            skLineSegment(sketch, "E355", {"start": v(48.89, 50.48) * mm, "end": v(51.1, 49.59) * mm});
            skLineSegment(sketch, "E356", {"start": v(51.1, 49.59) * mm, "end": v(51.24, 49.62) * mm});
            skLineSegment(sketch, "E357", {"start": v(51.24, 49.62) * mm, "end": v(53.13, 49.34) * mm});
            skLineSegment(sketch, "E358", {"start": v(53.13, 49.34) * mm, "end": v(50.5, 45.35) * mm});
            skLineSegment(sketch, "E359", {"start": v(50.5, 45.35) * mm, "end": v(48.74, 45.5) * mm});
            skLineSegment(sketch, "E360", {"start": v(48.74, 45.5) * mm, "end": v(46.46, 46.1) * mm});
            skLineSegment(sketch, "E361", {"start": v(46.46, 46.1) * mm, "end": v(44.47, 47.2) * mm});
            skLineSegment(sketch, "E362", {"start": v(44.47, 47.2) * mm, "end": v(43.08, 48.2) * mm});
            skLineSegment(sketch, "E363", {"start": v(43.08, 48.2) * mm, "end": v(41.72, 49.41) * mm});
            skLineSegment(sketch, "E364", {"start": v(41.72, 49.41) * mm, "end": v(40.48, 50.76) * mm});
            skLineSegment(sketch, "E365", {"start": v(40.48, 50.76) * mm, "end": v(39.37, 52.65) * mm});
            skLineSegment(sketch, "E366", {"start": v(39.37, 52.65) * mm, "end": v(38.8, 54.47) * mm});
            skLineSegment(sketch, "E367", {"start": v(38.8, 54.47) * mm, "end": v(38.48, 56.72) * mm});
            skLineSegment(sketch, "E368", {"start": v(38.48, 56.72) * mm, "end": v(38.41, 58.71) * mm});
            skLineSegment(sketch, "E369", {"start": v(38.41, 58.71) * mm, "end": v(38.73, 60.67) * mm});
            skLineSegment(sketch, "E370", {"start": v(38.73, 60.67) * mm, "end": v(39.44, 62.45) * mm});
            skLineSegment(sketch, "E371", {"start": v(39.44, 62.45) * mm, "end": v(40.58, 64.34) * mm});
            skLineSegment(sketch, "E372", {"start": v(40.58, 64.34) * mm, "end": v(42.26, 66.12) * mm});
            skLineSegment(sketch, "E373", {"start": v(42.26, 66.12) * mm, "end": v(43.19, 66.84) * mm});
            skLineSegment(sketch, "E374", {"start": v(43.19, 66.84) * mm, "end": v(43.97, 67.3) * mm});
            skLineSegment(sketch, "E375", {"start": v(43.97, 67.3) * mm, "end": v(45.32, 68.08) * mm});
            skLineSegment(sketch, "E376", {"start": v(45.32, 68.08) * mm, "end": v(47.14, 68.73) * mm});
            skLineSegment(sketch, "E377", {"start": v(47.14, 68.73) * mm, "end": v(49.03, 69.05) * mm});
            skLineSegment(sketch, "E378", {"start": v(49.03, 69.05) * mm, "end": v(51.31, 69.15) * mm});
            skLineSegment(sketch, "E379", {"start": v(51.31, 69.15) * mm, "end": v(53.56, 68.76) * mm});
            skLineSegment(sketch, "E380", {"start": v(53.56, 68.76) * mm, "end": v(55.4, 68.2) * mm});
            skLineSegment(sketch, "E381", {"start": v(55.4, 68.2) * mm, "end": v(57.51, 67.05) * mm});
            skLineSegment(sketch, "E382", {"start": v(57.51, 67.05) * mm, "end": v(59.47, 65.66) * mm});
            skLineSegment(sketch, "E383", {"start": v(59.47, 65.66) * mm, "end": v(60.93, 64.16) * mm});
            skLineSegment(sketch, "E384", {"start": v(60.93, 64.16) * mm, "end": v(62.32, 62.17) * mm});
            skLineSegment(sketch, "E385", {"start": v(62.32, 62.17) * mm, "end": v(63.32, 60.03) * mm});
            skLineSegment(sketch, "E386", {"start": v(63.32, 60.03) * mm, "end": v(63.89, 58.28) * mm});
            skFitSpline(sketch, "E387", {"points": [v(83.6, 16.84) * mm, v(83.6, 17.37) * mm, v(83.6, 17.9) * mm, v(83.6, 18.44) * mm]});
            skFitSpline(sketch, "E388", {"points": [v(83.6, 18.44) * mm, v(83.58, 19) * mm, v(83.56, 19.54) * mm, v(83.53, 20.08) * mm]});
            skLineSegment(sketch, "E389", {"start": v(68.84, 17.62) * mm, "end": v(69.02, 17.4) * mm});
            skLineSegment(sketch, "E390", {"start": v(69.02, 17.4) * mm, "end": v(70.2, 16.63) * mm});
            skLineSegment(sketch, "E391", {"start": v(70.2, 16.63) * mm, "end": v(71.73, 17.05) * mm});
            skLineSegment(sketch, "E392", {"start": v(71.73, 17.05) * mm, "end": v(72.34, 18.23) * mm});
            skLineSegment(sketch, "E393", {"start": v(72.34, 18.23) * mm, "end": v(72.23, 24.25) * mm});
            skLineSegment(sketch, "E394", {"start": v(72.23, 24.25) * mm, "end": v(73.23, 27.17) * mm});
            skLineSegment(sketch, "E395", {"start": v(73.23, 27.17) * mm, "end": v(74.47, 28.64) * mm});
            skLineSegment(sketch, "E396", {"start": v(74.47, 28.64) * mm, "end": v(75.86, 29.5) * mm});
            skLineSegment(sketch, "E397", {"start": v(75.86, 29.5) * mm, "end": v(77.5, 30.06) * mm});
            skLineSegment(sketch, "E398", {"start": v(77.5, 30.06) * mm, "end": v(80.71, 30.06) * mm});
            skLineSegment(sketch, "E399", {"start": v(80.71, 30.06) * mm, "end": v(82.56, 29.24) * mm});
            skLineSegment(sketch, "E400", {"start": v(82.56, 29.24) * mm, "end": v(84.3, 28.06) * mm});
            skLineSegment(sketch, "E401", {"start": v(84.3, 28.06) * mm, "end": v(85.63, 26.46) * mm});
            skLineSegment(sketch, "E402", {"start": v(85.63, 26.46) * mm, "end": v(86.77, 24.47) * mm});
            skLineSegment(sketch, "E403", {"start": v(86.77, 24.47) * mm, "end": v(87.66, 22.15) * mm});
            skLineSegment(sketch, "E404", {"start": v(87.66, 22.15) * mm, "end": v(88.09, 19.94) * mm});
            skLineSegment(sketch, "E405", {"start": v(88.09, 19.94) * mm, "end": v(88.09, 17.23) * mm});
            skLineSegment(sketch, "E406", {"start": v(88.09, 17.23) * mm, "end": v(87.8, 14.3) * mm});
            skLineSegment(sketch, "E407", {"start": v(87.8, 14.3) * mm, "end": v(83.24, 14.2) * mm});
            skLineSegment(sketch, "E408", {"start": v(83.24, 14.2) * mm, "end": v(83.6, 16.84) * mm});
            skFitSpline(sketch, "E409", {"points": [v(62.6, 19.73) * mm, v(62.6, 20.51) * mm, v(62.63, 21.3) * mm, v(62.68, 22.08) * mm]});
            skFitSpline(sketch, "E410", {"points": [v(62.68, 22.08) * mm, v(62.71, 22.67) * mm, v(62.76, 23.27) * mm, v(62.82, 23.86) * mm]});
            skLineSegment(sketch, "E411", {"start": v(83.53, 20.08) * mm, "end": v(82.81, 21.94) * mm});
            skLineSegment(sketch, "E412", {"start": v(82.81, 21.94) * mm, "end": v(81.96, 22.93) * mm});
            skLineSegment(sketch, "E413", {"start": v(81.96, 22.93) * mm, "end": v(81.1, 23.61) * mm});
            skLineSegment(sketch, "E414", {"start": v(81.1, 23.61) * mm, "end": v(80.25, 23.65) * mm});
            skLineSegment(sketch, "E415", {"start": v(80.25, 23.65) * mm, "end": v(79.53, 23.18) * mm});
            skLineSegment(sketch, "E416", {"start": v(79.53, 23.18) * mm, "end": v(78.71, 21.4) * mm});
            skLineSegment(sketch, "E417", {"start": v(78.71, 21.4) * mm, "end": v(78.71, 20.08) * mm});
            skLineSegment(sketch, "E418", {"start": v(78.71, 20.08) * mm, "end": v(78.93, 18.73) * mm});
            skLineSegment(sketch, "E419", {"start": v(78.93, 18.73) * mm, "end": v(78.93, 14.88) * mm});
            skLineSegment(sketch, "E420", {"start": v(78.93, 14.88) * mm, "end": v(78.1, 13) * mm});
            skLineSegment(sketch, "E421", {"start": v(78.1, 13) * mm, "end": v(77.18, 11.64) * mm});
            skLineSegment(sketch, "E422", {"start": v(77.18, 11.64) * mm, "end": v(76.18, 10.53) * mm});
            skLineSegment(sketch, "E423", {"start": v(76.18, 10.53) * mm, "end": v(74.44, 9.68) * mm});
            skLineSegment(sketch, "E424", {"start": v(74.44, 9.68) * mm, "end": v(72.83, 9.32) * mm});
            skLineSegment(sketch, "E425", {"start": v(72.83, 9.32) * mm, "end": v(70.48, 9.53) * mm});
            skLineSegment(sketch, "E426", {"start": v(70.48, 9.53) * mm, "end": v(69.13, 9.93) * mm});
            skLineSegment(sketch, "E427", {"start": v(69.13, 9.93) * mm, "end": v(67.6, 10.82) * mm});
            skLineSegment(sketch, "E428", {"start": v(67.6, 10.82) * mm, "end": v(66.63, 11.67) * mm});
            skLineSegment(sketch, "E429", {"start": v(66.63, 11.67) * mm, "end": v(65.46, 13.03) * mm});
            skLineSegment(sketch, "E430", {"start": v(65.46, 13.03) * mm, "end": v(64.5, 14.67) * mm});
            skLineSegment(sketch, "E431", {"start": v(64.5, 14.67) * mm, "end": v(63.46, 16.77) * mm});
            skLineSegment(sketch, "E432", {"start": v(63.46, 16.77) * mm, "end": v(62.9, 18.4) * mm});
            skLineSegment(sketch, "E433", {"start": v(62.9, 18.4) * mm, "end": v(62.6, 19.73) * mm});
            skFitSpline(sketch, "E434", {"points": [v(-39.06, 88.68) * mm, v(-37.26, 89.36) * mm, v(-35.46, 90.04) * mm, v(-33.65, 90.68) * mm]});
            skFitSpline(sketch, "E435", {"points": [v(-33.65, 90.68) * mm, v(-31.78, 91.33) * mm, v(-29.9, 91.95) * mm, v(-28.02, 92.53) * mm]});
            skLineSegment(sketch, "E436", {"start": v(62.82, 23.86) * mm, "end": v(63.1, 25.4) * mm});
            skLineSegment(sketch, "E437", {"start": v(63.1, 25.4) * mm, "end": v(63.6, 26.57) * mm});
            skLineSegment(sketch, "E438", {"start": v(63.6, 26.57) * mm, "end": v(68.52, 26.6) * mm});
            skLineSegment(sketch, "E439", {"start": v(68.52, 26.6) * mm, "end": v(67.95, 24.93) * mm});
            skLineSegment(sketch, "E440", {"start": v(67.95, 24.93) * mm, "end": v(67.6, 22.3) * mm});
            skLineSegment(sketch, "E441", {"start": v(67.6, 22.3) * mm, "end": v(67.88, 19.37) * mm});
            skLineSegment(sketch, "E442", {"start": v(67.88, 19.37) * mm, "end": v(68.84, 17.62) * mm});
            skFitSpline(sketch, "E443", {"points": [v(-21.28, 94.2) * mm, v(-17.79, 95.07) * mm, v(-14.22, 95.6) * mm, v(-10.62, 95.8) * mm]});
            skLineSegment(sketch, "E444", {"start": v(-28.02, 92.53) * mm, "end": v(-21.28, 94.2) * mm});
            skFitSpline(sketch, "E445", {"points": [v(-4.21, 96.17) * mm, v(-0.52, 96.37) * mm, v(3.18, 96.31) * mm, v(6.87, 96.06) * mm]});
            skLineSegment(sketch, "E446", {"start": v(-10.62, 95.8) * mm, "end": v(-4.21, 96.17) * mm});
            skFitSpline(sketch, "E447", {"points": [v(22.3, 94.1) * mm, v(23.68, 93.72) * mm, v(25.06, 93.34) * mm, v(26.44, 92.96) * mm]});
            skFitSpline(sketch, "E448", {"points": [v(26.44, 92.96) * mm, v(28.19, 92.47) * mm, v(29.94, 92) * mm, v(31.68, 91.46) * mm]});
            skFitSpline(sketch, "E449", {"points": [v(31.68, 91.46) * mm, v(33.23, 90.99) * mm, v(34.78, 90.48) * mm, v(36.3, 89.93) * mm]});
            skFitSpline(sketch, "E450", {"points": [v(36.3, 89.93) * mm, v(38.11, 89.28) * mm, v(39.9, 88.58) * mm, v(41.65, 87.83) * mm]});
            skFitSpline(sketch, "E451", {"points": [v(41.65, 87.83) * mm, v(43.6, 86.91) * mm, v(45.52, 85.96) * mm, v(47.43, 84.98) * mm]});
            skFitSpline(sketch, "E452", {"points": [v(47.43, 84.98) * mm, v(49.42, 83.94) * mm, v(51.4, 82.87) * mm, v(53.34, 81.73) * mm]});
            skFitSpline(sketch, "E453", {"points": [v(53.34, 81.73) * mm, v(54.64, 80.97) * mm, v(55.92, 80.2) * mm, v(57.2, 79.38) * mm]});
            skFitSpline(sketch, "E454", {"points": [v(57.2, 79.38) * mm, v(58.6, 78.47) * mm, v(59.96, 77.5) * mm, v(61.29, 76.5) * mm]});
            skFitSpline(sketch, "E455", {"points": [v(61.29, 76.5) * mm, v(62.41, 75.64) * mm, v(63.51, 74.75) * mm, v(64.6, 73.86) * mm]});
            skFitSpline(sketch, "E456", {"points": [v(64.6, 73.86) * mm, v(65.94, 72.76) * mm, v(67.27, 71.66) * mm, v(68.6, 70.54) * mm]});
            skLineSegment(sketch, "E457", {"start": v(6.87, 96.06) * mm, "end": v(13.54, 95.6) * mm});
            skLineSegment(sketch, "E458", {"start": v(13.54, 95.6) * mm, "end": v(22.3, 94.1) * mm});
            skFitSpline(sketch, "E459", {"points": [v(77.47, 61.53) * mm, v(79.17, 59.48) * mm, v(80.8, 57.38) * mm, v(82.35, 55.22) * mm]});
            skFitSpline(sketch, "E460", {"points": [v(82.35, 55.22) * mm, v(83.28, 53.93) * mm, v(84.18, 52.62) * mm, v(85.06, 51.3) * mm]});
            skFitSpline(sketch, "E461", {"points": [v(85.06, 51.3) * mm, v(86.1, 49.72) * mm, v(87.11, 48.12) * mm, v(88.09, 46.49) * mm]});
            skFitSpline(sketch, "E462", {"points": [v(88.09, 46.49) * mm, v(89.22, 44.39) * mm, v(90.32, 42.26) * mm, v(91.37, 40.1) * mm]});
            skFitSpline(sketch, "E463", {"points": [v(91.37, 40.1) * mm, v(92.23, 38.34) * mm, v(93.06, 36.56) * mm, v(93.86, 34.76) * mm]});
            skLineSegment(sketch, "E464", {"start": v(68.6, 70.54) * mm, "end": v(73.23, 66.12) * mm});
            skLineSegment(sketch, "E465", {"start": v(73.23, 66.12) * mm, "end": v(77.47, 61.53) * mm});
            skFitSpline(sketch, "E466", {"points": [v(95.78, 29.45) * mm, v(96.57, 26.72) * mm, v(97.32, 23.98) * mm, v(98.03, 21.22) * mm]});
            skFitSpline(sketch, "E467", {"points": [v(98.03, 21.22) * mm, v(98.52, 19.3) * mm, v(99, 17.36) * mm, v(99.45, 15.41) * mm]});
            skFitSpline(sketch, "E468", {"points": [v(99.45, 15.41) * mm, v(99.7, 13.68) * mm, v(99.9, 11.93) * mm, v(100.02, 10.18) * mm]});
            skFitSpline(sketch, "E469", {"points": [v(100.02, 10.18) * mm, v(100.11, 9.01) * mm, v(100.17, 7.85) * mm, v(100.2, 6.68) * mm]});
            skLineSegment(sketch, "E470", {"start": v(93.86, 34.76) * mm, "end": v(95.78, 29.45) * mm});
            skFitSpline(sketch, "E471", {"points": [v(99.81, -12.85) * mm, v(99.3, -14.72) * mm, v(98.93, -16.64) * mm, v(98.56, -18.55) * mm]});
            skFitSpline(sketch, "E472", {"points": [v(98.56, -18.55) * mm, v(98.27, -20.08) * mm, v(97.94, -21.6) * mm, v(97.57, -23.1) * mm]});
            skFitSpline(sketch, "E473", {"points": [v(97.57, -23.1) * mm, v(97.12, -24.93) * mm, v(96.62, -26.73) * mm, v(96.07, -28.53) * mm]});
            skFitSpline(sketch, "E474", {"points": [v(96.07, -28.53) * mm, v(95.38, -30.43) * mm, v(94.66, -32.33) * mm, v(93.93, -34.23) * mm]});
            skFitSpline(sketch, "E475", {"points": [v(93.93, -34.23) * mm, v(93.21, -36.08) * mm, v(92.48, -37.92) * mm, v(91.72, -39.75) * mm]});
            skFitSpline(sketch, "E476", {"points": [v(91.72, -39.75) * mm, v(90.72, -41.79) * mm, v(89.67, -43.8) * mm, v(88.55, -45.77) * mm]});
            skFitSpline(sketch, "E477", {"points": [v(88.55, -45.77) * mm, v(87.53, -47.58) * mm, v(86.46, -49.37) * mm, v(85.34, -51.12) * mm]});
            skFitSpline(sketch, "E478", {"points": [v(85.34, -51.12) * mm, v(84.28, -52.74) * mm, v(83.18, -54.33) * mm, v(82.03, -55.9) * mm]});
            skFitSpline(sketch, "E479", {"points": [v(82.03, -55.9) * mm, v(80.69, -57.71) * mm, v(79.28, -59.48) * mm, v(77.82, -61.2) * mm]});
            skFitSpline(sketch, "E480", {"points": [v(77.82, -61.2) * mm, v(76.29, -62.95) * mm, v(74.7, -64.67) * mm, v(73.08, -66.33) * mm]});
            skFitSpline(sketch, "E481", {"points": [v(73.08, -66.33) * mm, v(71.68, -67.78) * mm, v(70.24, -69.2) * mm, v(68.77, -70.58) * mm]});
            skFitSpline(sketch, "E482", {"points": [v(68.77, -70.58) * mm, v(67.19, -71.92) * mm, v(65.59, -73.24) * mm, v(63.96, -74.53) * mm]});
            skFitSpline(sketch, "E483", {"points": [v(63.96, -74.53) * mm, v(62.73, -75.5) * mm, v(61.5, -76.47) * mm, v(60.22, -77.38) * mm]});
            skFitSpline(sketch, "E484", {"points": [v(60.22, -77.38) * mm, v(59.03, -78.23) * mm, v(57.81, -79.04) * mm, v(56.58, -79.84) * mm]});
            skFitSpline(sketch, "E485", {"points": [v(56.58, -79.84) * mm, v(55.2, -80.74) * mm, v(53.8, -81.64) * mm, v(52.38, -82.48) * mm]});
            skFitSpline(sketch, "E486", {"points": [v(52.38, -82.48) * mm, v(50.67, -83.49) * mm, v(48.91, -84.43) * mm, v(47.14, -85.33) * mm]});
            skFitSpline(sketch, "E487", {"points": [v(47.14, -85.33) * mm, v(45.87, -85.97) * mm, v(44.6, -86.6) * mm, v(43.3, -87.18) * mm]});
            skFitSpline(sketch, "E488", {"points": [v(43.3, -87.18) * mm, v(41.81, -87.84) * mm, v(40.3, -88.44) * mm, v(38.8, -89.03) * mm]});
            skFitSpline(sketch, "E489", {"points": [v(38.8, -89.03) * mm, v(37.16, -89.68) * mm, v(35.53, -90.32) * mm, v(33.88, -90.96) * mm]});
            skFitSpline(sketch, "E490", {"points": [v(33.88, -90.96) * mm, v(32.05, -91.5) * mm, v(30.2, -92.04) * mm, v(28.36, -92.56) * mm]});
            skFitSpline(sketch, "E491", {"points": [v(28.36, -92.56) * mm, v(26.44, -93.1) * mm, v(24.52, -93.63) * mm, v(22.59, -94.13) * mm]});
            skLineSegment(sketch, "E492", {"start": v(100.2, 6.68) * mm, "end": v(100.13, -7.9) * mm});
            skLineSegment(sketch, "E493", {"start": v(100.13, -7.9) * mm, "end": v(99.81, -12.85) * mm});
            skFitSpline(sketch, "E494", {"points": [v(-7.2, -96.27) * mm, v(-10.17, -95.96) * mm, v(-13.13, -95.58) * mm, v(-16.08, -95.13) * mm]});
            skFitSpline(sketch, "E495", {"points": [v(-16.08, -95.13) * mm, v(-17.72, -94.87) * mm, v(-19.36, -94.6) * mm, v(-21, -94.27) * mm]});
            skFitSpline(sketch, "E496", {"points": [v(-21, -94.27) * mm, v(-22.9, -93.9) * mm, v(-24.79, -93.46) * mm, v(-26.66, -92.95) * mm]});
            skFitSpline(sketch, "E497", {"points": [v(-26.66, -92.95) * mm, v(-28.2, -92.51) * mm, v(-29.74, -92.04) * mm, v(-31.26, -91.53) * mm]});
            skFitSpline(sketch, "E498", {"points": [v(-31.26, -91.53) * mm, v(-33.02, -90.94) * mm, v(-34.77, -90.31) * mm, v(-36.5, -89.64) * mm]});
            skFitSpline(sketch, "E499", {"points": [v(-36.5, -89.64) * mm, v(-38.24, -88.96) * mm, v(-39.98, -88.24) * mm, v(-41.7, -87.5) * mm]});
            skFitSpline(sketch, "E500", {"points": [v(-41.7, -87.5) * mm, v(-42.98, -86.95) * mm, v(-44.25, -86.39) * mm, v(-45.51, -85.8) * mm]});
            skFitSpline(sketch, "E501", {"points": [v(-45.51, -85.8) * mm, v(-47.24, -84.97) * mm, v(-48.94, -84.1) * mm, v(-50.6, -83.15) * mm]});
            skFitSpline(sketch, "E502", {"points": [v(-50.6, -83.15) * mm, v(-52.44, -82.1) * mm, v(-54.25, -81.01) * mm, v(-56.03, -79.88) * mm]});
            skFitSpline(sketch, "E503", {"points": [v(-56.03, -79.88) * mm, v(-58, -78.61) * mm, v(-59.96, -77.3) * mm, v(-61.87, -75.92) * mm]});
            skLineSegment(sketch, "E504", {"start": v(22.59, -94.13) * mm, "end": v(15.92, -95.34) * mm});
            skLineSegment(sketch, "E505", {"start": v(15.92, -95.34) * mm, "end": v(8.69, -96.13) * mm});
            skLineSegment(sketch, "E506", {"start": v(8.69, -96.13) * mm, "end": v(-7.2, -96.27) * mm});
            skFitSpline(sketch, "E507", {"points": [v(-67.68, -71.25) * mm, v(-69.35, -69.67) * mm, v(-70.99, -68.05) * mm, v(-72.6, -66.4) * mm]});
            skFitSpline(sketch, "E508", {"points": [v(-72.6, -66.4) * mm, v(-74.03, -64.93) * mm, v(-75.45, -63.44) * mm, v(-76.84, -61.92) * mm]});
            skFitSpline(sketch, "E509", {"points": [v(-76.84, -61.92) * mm, v(-78.54, -59.93) * mm, v(-80.17, -57.89) * mm, v(-81.72, -55.79) * mm]});
            skFitSpline(sketch, "E510", {"points": [v(-81.72, -55.79) * mm, v(-82.68, -54.49) * mm, v(-83.6, -53.17) * mm, v(-84.5, -51.83) * mm]});
            skFitSpline(sketch, "E511", {"points": [v(-84.5, -51.83) * mm, v(-85.47, -50.37) * mm, v(-86.41, -48.88) * mm, v(-87.31, -47.38) * mm]});
            skFitSpline(sketch, "E512", {"points": [v(-87.31, -47.38) * mm, v(-88.17, -45.82) * mm, v(-89, -44.25) * mm, v(-89.8, -42.67) * mm]});
            skFitSpline(sketch, "E513", {"points": [v(-89.8, -42.67) * mm, v(-90.8, -40.72) * mm, v(-91.77, -38.75) * mm, v(-92.7, -36.76) * mm]});
            skLineSegment(sketch, "E514", {"start": v(-61.87, -75.92) * mm, "end": v(-67.68, -71.25) * mm});
            skFitSpline(sketch, "E515", {"points": [v(-95.44, -29.34) * mm, v(-96.13, -27.15) * mm, v(-96.76, -24.94) * mm, v(-97.33, -22.72) * mm]});
            skFitSpline(sketch, "E516", {"points": [v(-97.33, -22.72) * mm, v(-98, -20.06) * mm, v(-98.6, -17.39) * mm, v(-99.1, -14.7) * mm]});
            skLineSegment(sketch, "E517", {"start": v(-92.7, -36.76) * mm, "end": v(-95.44, -29.34) * mm});
            skFitSpline(sketch, "E518", {"points": [v(-100.21, 1.37) * mm, v(-100.1, 3.94) * mm, v(-99.93, 6.51) * mm, v(-99.68, 9.07) * mm]});
            skFitSpline(sketch, "E519", {"points": [v(-99.68, 9.07) * mm, v(-99.5, 10.96) * mm, v(-99.27, 12.85) * mm, v(-99, 14.74) * mm]});
            skLineSegment(sketch, "E520", {"start": v(-99.1, -14.7) * mm, "end": v(-99.93, -6.79) * mm});
            skLineSegment(sketch, "E521", {"start": v(-99.93, -6.79) * mm, "end": v(-100.21, 1.37) * mm});
            skFitSpline(sketch, "E522", {"points": [v(-97.9, 20.51) * mm, v(-97.37, 22.74) * mm, v(-96.78, 24.95) * mm, v(-96.12, 27.14) * mm]});
            skFitSpline(sketch, "E523", {"points": [v(-96.12, 27.14) * mm, v(-95.46, 29.31) * mm, v(-94.73, 31.46) * mm, v(-93.94, 33.59) * mm]});
            skLineSegment(sketch, "E524", {"start": v(-99, 14.74) * mm, "end": v(-97.9, 20.51) * mm});
            skFitSpline(sketch, "E525", {"points": [v(-87.78, 46.42) * mm, v(-86.62, 48.42) * mm, v(-85.4, 50.38) * mm, v(-84.1, 52.3) * mm]});
            skFitSpline(sketch, "E526", {"points": [v(-84.1, 52.3) * mm, v(-82.98, 53.98) * mm, v(-81.8, 55.63) * mm, v(-80.58, 57.25) * mm]});
            skLineSegment(sketch, "E527", {"start": v(-93.94, 33.59) * mm, "end": v(-90.84, 40.68) * mm});
            skLineSegment(sketch, "E528", {"start": v(-90.84, 40.68) * mm, "end": v(-87.78, 46.42) * mm});
            skFitSpline(sketch, "E529", {"points": [v(-59.41, 77.67) * mm, v(-57.7, 78.8) * mm, v(-55.99, 79.91) * mm, v(-54.24, 80.98) * mm]});
            skFitSpline(sketch, "E530", {"points": [v(-54.24, 80.98) * mm, v(-52.7, 81.93) * mm, v(-51.15, 82.85) * mm, v(-49.57, 83.73) * mm]});
            skFitSpline(sketch, "E531", {"points": [v(-49.57, 83.73) * mm, v(-48.2, 84.5) * mm, v(-46.79, 85.23) * mm, v(-45.37, 85.94) * mm]});
            skFitSpline(sketch, "E532", {"points": [v(-45.37, 85.94) * mm, v(-44.19, 86.53) * mm, v(-43, 87.1) * mm, v(-41.77, 87.61) * mm]});
            skFitSpline(sketch, "E533", {"points": [v(-41.77, 87.61) * mm, v(-40.88, 87.99) * mm, v(-39.97, 88.34) * mm, v(-39.06, 88.68) * mm]});
            skFitSpline(sketch, "E534", {"points": [v(-37.63, 85.9) * mm, v(-35.89, 86.55) * mm, v(-34.15, 87.2) * mm, v(-32.4, 87.83) * mm]});
            skFitSpline(sketch, "E535", {"points": [v(-32.4, 87.83) * mm, v(-30.6, 88.46) * mm, v(-28.78, 89.06) * mm, v(-26.96, 89.62) * mm]});
            skLineSegment(sketch, "E536", {"start": v(-80.58, 57.25) * mm, "end": v(-77.7, 60.78) * mm});
            skLineSegment(sketch, "E537", {"start": v(-77.7, 60.78) * mm, "end": v(-71.03, 67.87) * mm});
            skLineSegment(sketch, "E538", {"start": v(-71.03, 67.87) * mm, "end": v(-65.68, 72.72) * mm});
            skLineSegment(sketch, "E539", {"start": v(-65.68, 72.72) * mm, "end": v(-59.41, 77.67) * mm});
            skFitSpline(sketch, "E540", {"points": [v(-20.45, 91.25) * mm, v(-17.08, 92.09) * mm, v(-13.63, 92.6) * mm, v(-10.16, 92.8) * mm]});
            skLineSegment(sketch, "E541", {"start": v(-26.96, 89.62) * mm, "end": v(-20.45, 91.25) * mm});
            skFitSpline(sketch, "E542", {"points": [v(-3.97, 93.15) * mm, v(-0.4, 93.34) * mm, v(3.18, 93.3) * mm, v(6.74, 93.04) * mm]});
            skLineSegment(sketch, "E543", {"start": v(-10.16, 92.8) * mm, "end": v(-3.97, 93.15) * mm});
            skFitSpline(sketch, "E544", {"points": [v(21.64, 91.14) * mm, v(22.97, 90.77) * mm, v(24.3, 90.4) * mm, v(25.63, 90.04) * mm]});
            skFitSpline(sketch, "E545", {"points": [v(25.63, 90.04) * mm, v(27.32, 89.57) * mm, v(29.01, 89.1) * mm, v(30.7, 88.59) * mm]});
            skFitSpline(sketch, "E546", {"points": [v(30.7, 88.59) * mm, v(32.2, 88.13) * mm, v(33.69, 87.63) * mm, v(35.17, 87.1) * mm]});
            skFitSpline(sketch, "E547", {"points": [v(35.17, 87.1) * mm, v(36.9, 86.47) * mm, v(38.63, 85.8) * mm, v(40.33, 85.06) * mm]});
            skFitSpline(sketch, "E548", {"points": [v(40.33, 85.06) * mm, v(42.2, 84.18) * mm, v(44.06, 83.26) * mm, v(45.9, 82.3) * mm]});
            skFitSpline(sketch, "E549", {"points": [v(45.9, 82.3) * mm, v(47.83, 81.3) * mm, v(49.74, 80.26) * mm, v(51.62, 79.16) * mm]});
            skFitSpline(sketch, "E550", {"points": [v(51.62, 79.16) * mm, v(52.87, 78.42) * mm, v(54.11, 77.66) * mm, v(55.34, 76.88) * mm]});
            skFitSpline(sketch, "E551", {"points": [v(55.34, 76.88) * mm, v(56.69, 76) * mm, v(58, 75.06) * mm, v(59.3, 74.08) * mm]});
            skFitSpline(sketch, "E552", {"points": [v(59.3, 74.08) * mm, v(60.38, 73.25) * mm, v(61.44, 72.4) * mm, v(62.5, 71.53) * mm]});
            skFitSpline(sketch, "E553", {"points": [v(62.5, 71.53) * mm, v(63.79, 70.46) * mm, v(65.07, 69.4) * mm, v(66.35, 68.31) * mm]});
            skLineSegment(sketch, "E554", {"start": v(6.74, 93.04) * mm, "end": v(13.17, 92.6) * mm});
            skLineSegment(sketch, "E555", {"start": v(13.17, 92.6) * mm, "end": v(21.64, 91.14) * mm});
            skFitSpline(sketch, "E556", {"points": [v(74.92, 59.58) * mm, v(76.56, 57.6) * mm, v(78.13, 55.55) * mm, v(79.63, 53.46) * mm]});
            skFitSpline(sketch, "E557", {"points": [v(79.63, 53.46) * mm, v(80.53, 52.22) * mm, v(81.4, 50.95) * mm, v(82.25, 49.67) * mm]});
            skFitSpline(sketch, "E558", {"points": [v(82.25, 49.67) * mm, v(83.26, 48.13) * mm, v(84.24, 46.58) * mm, v(85.17, 45) * mm]});
            skFitSpline(sketch, "E559", {"points": [v(85.17, 45) * mm, v(86.27, 42.96) * mm, v(87.33, 40.9) * mm, v(88.34, 38.82) * mm]});
            skFitSpline(sketch, "E560", {"points": [v(88.34, 38.82) * mm, v(89.17, 37.1) * mm, v(89.98, 35.38) * mm, v(90.75, 33.64) * mm]});
            skLineSegment(sketch, "E561", {"start": v(66.35, 68.31) * mm, "end": v(70.82, 64.03) * mm});
            skLineSegment(sketch, "E562", {"start": v(70.82, 64.03) * mm, "end": v(74.92, 59.58) * mm});
            skFitSpline(sketch, "E563", {"points": [v(92.6, 28.5) * mm, v(93.37, 25.85) * mm, v(94.1, 23.19) * mm, v(94.78, 20.52) * mm]});
            skFitSpline(sketch, "E564", {"points": [v(94.78, 20.52) * mm, v(95.26, 18.65) * mm, v(95.71, 16.77) * mm, v(96.15, 14.89) * mm]});
            skFitSpline(sketch, "E565", {"points": [v(96.15, 14.89) * mm, v(96.4, 13.2) * mm, v(96.58, 11.5) * mm, v(96.7, 9.81) * mm]});
            skFitSpline(sketch, "E566", {"points": [v(96.7, 9.81) * mm, v(96.79, 8.68) * mm, v(96.85, 7.56) * mm, v(96.88, 6.43) * mm]});
            skLineSegment(sketch, "E567", {"start": v(90.75, 33.64) * mm, "end": v(92.6, 28.5) * mm});
            skFitSpline(sketch, "E568", {"points": [v(96.5, -12.5) * mm, v(96, -14.32) * mm, v(95.65, -16.17) * mm, v(95.3, -18.02) * mm]});
            skFitSpline(sketch, "E569", {"points": [v(95.3, -18.02) * mm, v(95, -19.5) * mm, v(94.69, -20.98) * mm, v(94.33, -22.44) * mm]});
            skFitSpline(sketch, "E570", {"points": [v(94.33, -22.44) * mm, v(93.9, -24.2) * mm, v(93.42, -25.96) * mm, v(92.88, -27.7) * mm]});
            skFitSpline(sketch, "E571", {"points": [v(92.88, -27.7) * mm, v(92.22, -29.54) * mm, v(91.53, -31.39) * mm, v(90.82, -33.22) * mm]});
            skFitSpline(sketch, "E572", {"points": [v(90.82, -33.22) * mm, v(90.13, -35.01) * mm, v(89.42, -36.8) * mm, v(88.69, -38.57) * mm]});
            skFitSpline(sketch, "E573", {"points": [v(88.69, -38.57) * mm, v(87.72, -40.55) * mm, v(86.7, -42.5) * mm, v(85.62, -44.4) * mm]});
            skFitSpline(sketch, "E574", {"points": [v(85.62, -44.4) * mm, v(84.64, -46.16) * mm, v(83.6, -47.9) * mm, v(82.52, -49.59) * mm]});
            skFitSpline(sketch, "E575", {"points": [v(82.52, -49.59) * mm, v(81.5, -51.16) * mm, v(80.44, -52.7) * mm, v(79.32, -54.22) * mm]});
            skFitSpline(sketch, "E576", {"points": [v(79.32, -54.22) * mm, v(78.03, -55.98) * mm, v(76.67, -57.7) * mm, v(75.26, -59.36) * mm]});
            skFitSpline(sketch, "E577", {"points": [v(75.26, -59.36) * mm, v(73.78, -61.06) * mm, v(72.25, -62.72) * mm, v(70.69, -64.34) * mm]});
            skFitSpline(sketch, "E578", {"points": [v(70.69, -64.34) * mm, v(69.33, -65.74) * mm, v(67.94, -67.1) * mm, v(66.52, -68.45) * mm]});
            skFitSpline(sketch, "E579", {"points": [v(66.52, -68.45) * mm, v(65, -69.75) * mm, v(63.44, -71.03) * mm, v(61.87, -72.28) * mm]});
            skFitSpline(sketch, "E580", {"points": [v(61.87, -72.28) * mm, v(60.69, -73.23) * mm, v(59.5, -74.16) * mm, v(58.26, -75.04) * mm]});
            skFitSpline(sketch, "E581", {"points": [v(58.26, -75.04) * mm, v(57.11, -75.87) * mm, v(55.93, -76.65) * mm, v(54.75, -77.43) * mm]});
            skFitSpline(sketch, "E582", {"points": [v(54.75, -77.43) * mm, v(53.41, -78.3) * mm, v(52.06, -79.17) * mm, v(50.69, -79.98) * mm]});
            skFitSpline(sketch, "E583", {"points": [v(50.69, -79.98) * mm, v(49.04, -80.96) * mm, v(47.34, -81.87) * mm, v(45.63, -82.74) * mm]});
            skFitSpline(sketch, "E584", {"points": [v(45.63, -82.74) * mm, v(44.4, -83.37) * mm, v(43.17, -83.98) * mm, v(41.91, -84.54) * mm]});
            skFitSpline(sketch, "E585", {"points": [v(41.91, -84.54) * mm, v(40.48, -85.18) * mm, v(39.03, -85.76) * mm, v(37.58, -86.34) * mm]});
            skFitSpline(sketch, "E586", {"points": [v(37.58, -86.34) * mm, v(36, -86.96) * mm, v(34.41, -87.58) * mm, v(32.83, -88.2) * mm]});
            skFitSpline(sketch, "E587", {"points": [v(32.83, -88.2) * mm, v(31.05, -88.73) * mm, v(29.27, -89.25) * mm, v(27.5, -89.75) * mm]});
            skFitSpline(sketch, "E588", {"points": [v(27.5, -89.75) * mm, v(25.64, -90.28) * mm, v(23.78, -90.78) * mm, v(21.92, -91.27) * mm]});
            skLineSegment(sketch, "E589", {"start": v(96.88, 6.43) * mm, "end": v(96.8, -7.7) * mm});
            skLineSegment(sketch, "E590", {"start": v(96.8, -7.7) * mm, "end": v(96.5, -12.5) * mm});
            skFitSpline(sketch, "E591", {"points": [v(-6.86, -93.35) * mm, v(-9.72, -93.05) * mm, v(-12.58, -92.68) * mm, v(-15.43, -92.24) * mm]});
            skFitSpline(sketch, "E592", {"points": [v(-15.43, -92.24) * mm, v(-17.01, -92) * mm, v(-18.6, -91.73) * mm, v(-20.18, -91.41) * mm]});
            skFitSpline(sketch, "E593", {"points": [v(-20.18, -91.41) * mm, v(-22.01, -91.05) * mm, v(-23.84, -90.62) * mm, v(-25.65, -90.13) * mm]});
            skFitSpline(sketch, "E594", {"points": [v(-25.65, -90.13) * mm, v(-27.14, -89.7) * mm, v(-28.62, -89.24) * mm, v(-30.09, -88.75) * mm]});
            skFitSpline(sketch, "E595", {"points": [v(-30.09, -88.75) * mm, v(-31.79, -88.18) * mm, v(-33.48, -87.57) * mm, v(-35.15, -86.92) * mm]});
            skFitSpline(sketch, "E596", {"points": [v(-35.15, -86.92) * mm, v(-36.84, -86.27) * mm, v(-38.5, -85.57) * mm, v(-40.17, -84.85) * mm]});
            skFitSpline(sketch, "E597", {"points": [v(-40.17, -84.85) * mm, v(-41.4, -84.32) * mm, v(-42.64, -83.77) * mm, v(-43.86, -83.2) * mm]});
            skFitSpline(sketch, "E598", {"points": [v(-43.86, -83.2) * mm, v(-45.53, -82.4) * mm, v(-47.17, -81.55) * mm, v(-48.78, -80.64) * mm]});
            skLineSegment(sketch, "E599", {"start": v(21.92, -91.27) * mm, "end": v(15.48, -92.45) * mm});
            skLineSegment(sketch, "E600", {"start": v(15.48, -92.45) * mm, "end": v(8.5, -93.2) * mm});
            skLineSegment(sketch, "E601", {"start": v(8.5, -93.2) * mm, "end": v(-6.86, -93.35) * mm});
            skFitSpline(sketch, "E602", {"points": [v(-65.26, -69.1) * mm, v(-66.88, -67.57) * mm, v(-68.46, -66) * mm, v(-70.01, -64.4) * mm]});
            skFitSpline(sketch, "E603", {"points": [v(-70.01, -64.4) * mm, v(-71.4, -62.98) * mm, v(-72.77, -61.53) * mm, v(-74.1, -60.05) * mm]});
            skFitSpline(sketch, "E604", {"points": [v(-74.1, -60.05) * mm, v(-75.75, -58.13) * mm, v(-77.33, -56.15) * mm, v(-78.82, -54.11) * mm]});
            skFitSpline(sketch, "E605", {"points": [v(-78.82, -54.11) * mm, v(-79.75, -52.86) * mm, v(-80.64, -51.58) * mm, v(-81.5, -50.28) * mm]});
            skFitSpline(sketch, "E606", {"points": [v(-81.5, -50.28) * mm, v(-82.45, -48.86) * mm, v(-83.36, -47.43) * mm, v(-84.23, -45.96) * mm]});
            skFitSpline(sketch, "E607", {"points": [v(-84.23, -45.96) * mm, v(-85.05, -44.46) * mm, v(-85.86, -42.94) * mm, v(-86.64, -41.4) * mm]});
            skFitSpline(sketch, "E608", {"points": [v(-86.64, -41.4) * mm, v(-87.6, -39.51) * mm, v(-88.53, -37.6) * mm, v(-89.42, -35.67) * mm]});
            skLineSegment(sketch, "E609", {"start": v(-48.78, -80.64) * mm, "end": v(-54, -77.46) * mm});
            skLineSegment(sketch, "E610", {"start": v(-54, -77.46) * mm, "end": v(-59.65, -73.63) * mm});
            skLineSegment(sketch, "E611", {"start": v(-59.65, -73.63) * mm, "end": v(-65.26, -69.1) * mm});
            skFitSpline(sketch, "E612", {"points": [v(-92.07, -28.49) * mm, v(-92.74, -26.36) * mm, v(-93.35, -24.22) * mm, v(-93.9, -22.06) * mm]});
            skFitSpline(sketch, "E613", {"points": [v(-93.9, -22.06) * mm, v(-94.55, -19.5) * mm, v(-95.13, -16.9) * mm, v(-95.62, -14.3) * mm]});
            skLineSegment(sketch, "E614", {"start": v(-89.42, -35.67) * mm, "end": v(-92.07, -28.49) * mm});
            skFitSpline(sketch, "E615", {"points": [v(-96.69, 1.28) * mm, v(-96.58, 3.77) * mm, v(-96.41, 6.26) * mm, v(-96.17, 8.74) * mm]});
            skFitSpline(sketch, "E616", {"points": [v(-96.17, 8.74) * mm, v(-96, 10.58) * mm, v(-95.77, 12.4) * mm, v(-95.52, 14.23) * mm]});
            skLineSegment(sketch, "E617", {"start": v(-95.62, -14.3) * mm, "end": v(-96.41, -6.63) * mm});
            skLineSegment(sketch, "E618", {"start": v(-96.41, -6.63) * mm, "end": v(-96.69, 1.28) * mm});
            skFitSpline(sketch, "E619", {"points": [v(-94.45, 19.83) * mm, v(-93.94, 21.98) * mm, v(-93.37, 24.13) * mm, v(-92.73, 26.25) * mm]});
            skFitSpline(sketch, "E620", {"points": [v(-92.73, 26.25) * mm, v(-92.1, 28.35) * mm, v(-91.4, 30.44) * mm, v(-90.63, 32.5) * mm]});
            skLineSegment(sketch, "E621", {"start": v(-95.52, 14.23) * mm, "end": v(-94.45, 19.83) * mm});
            skFitSpline(sketch, "E622", {"points": [v(-84.67, 44.93) * mm, v(-83.55, 46.87) * mm, v(-82.37, 48.77) * mm, v(-81.13, 50.63) * mm]});
            skFitSpline(sketch, "E623", {"points": [v(-81.13, 50.63) * mm, v(-80.04, 52.26) * mm, v(-78.9, 53.87) * mm, v(-77.72, 55.43) * mm]});
            skLineSegment(sketch, "E624", {"start": v(-90.63, 32.5) * mm, "end": v(-87.63, 39.37) * mm});
            skLineSegment(sketch, "E625", {"start": v(-87.63, 39.37) * mm, "end": v(-84.67, 44.93) * mm});
            skFitSpline(sketch, "E626", {"points": [v(-57.28, 75.22) * mm, v(-55.63, 76.32) * mm, v(-53.97, 77.4) * mm, v(-52.29, 78.43) * mm]});
            skFitSpline(sketch, "E627", {"points": [v(-52.29, 78.43) * mm, v(-50.8, 79.35) * mm, v(-49.3, 80.24) * mm, v(-47.78, 81.1) * mm]});
            skFitSpline(sketch, "E628", {"points": [v(-47.78, 81.1) * mm, v(-46.44, 81.84) * mm, v(-45.09, 82.55) * mm, v(-43.72, 83.23) * mm]});
            skFitSpline(sketch, "E629", {"points": [v(-43.72, 83.23) * mm, v(-42.57, 83.8) * mm, v(-41.42, 84.36) * mm, v(-40.24, 84.86) * mm]});
            skFitSpline(sketch, "E630", {"points": [v(-40.24, 84.86) * mm, v(-39.38, 85.22) * mm, v(-38.5, 85.56) * mm, v(-37.63, 85.9) * mm]});
            skLineSegment(sketch, "E631", {"start": v(-77.72, 55.43) * mm, "end": v(-74.93, 58.85) * mm});
            skLineSegment(sketch, "E632", {"start": v(-74.93, 58.85) * mm, "end": v(-68.5, 65.72) * mm});
            skLineSegment(sketch, "E633", {"start": v(-68.5, 65.72) * mm, "end": v(-63.34, 70.42) * mm});
            skLineSegment(sketch, "E634", {"start": v(-63.34, 70.42) * mm, "end": v(-57.28, 75.22) * mm});
            skFitSpline(sketch, "E635", {"points": [v(-44.24, 38.77) * mm, v(-45.53, 37.33) * mm, v(-46.78, 35.85) * mm, v(-47.98, 34.33) * mm]});
            skFitSpline(sketch, "E636", {"points": [v(-47.98, 34.33) * mm, v(-49.02, 33.01) * mm, v(-50.03, 31.67) * mm, v(-51, 30.3) * mm]});
            skLineSegment(sketch, "E637", {"start": v(-29.86, 50.13) * mm, "end": v(-35.16, 47) * mm});
            skLineSegment(sketch, "E638", {"start": v(-35.16, 47) * mm, "end": v(-39.72, 43.25) * mm});
            skLineSegment(sketch, "E639", {"start": v(-39.72, 43.25) * mm, "end": v(-44.24, 38.77) * mm});
            skFitSpline(sketch, "E640", {"points": [v(-57.02, -17.1) * mm, v(-56.2, -19.15) * mm, v(-55.33, -21.19) * mm, v(-54.4, -23.2) * mm]});
            skFitSpline(sketch, "E641", {"points": [v(-54.4, -23.2) * mm, v(-53.44, -25.27) * mm, v(-52.42, -27.32) * mm, v(-51.35, -29.34) * mm]});
            skLineSegment(sketch, "E642", {"start": v(-51, 30.3) * mm, "end": v(-53.08, 26.8) * mm});
            skLineSegment(sketch, "E643", {"start": v(-53.08, 26.8) * mm, "end": v(-55.25, 22.23) * mm});
            skLineSegment(sketch, "E644", {"start": v(-55.25, 22.23) * mm, "end": v(-56.99, 17.52) * mm});
            skLineSegment(sketch, "E645", {"start": v(-56.99, 17.52) * mm, "end": v(-58.26, 12.73) * mm});
            skLineSegment(sketch, "E646", {"start": v(-58.26, 12.73) * mm, "end": v(-59.15, 7.67) * mm});
            skLineSegment(sketch, "E647", {"start": v(-59.15, 7.67) * mm, "end": v(-59.65, 1.72) * mm});
            skLineSegment(sketch, "E648", {"start": v(-59.65, 1.72) * mm, "end": v(-59.65, -4.23) * mm});
            skLineSegment(sketch, "E649", {"start": v(-59.65, -4.23) * mm, "end": v(-58.76, -10.06) * mm});
            skLineSegment(sketch, "E650", {"start": v(-58.76, -10.06) * mm, "end": v(-57.02, -17.1) * mm});
            skFitSpline(sketch, "E651", {"points": [v(-37.01, -44.8) * mm, v(-36.1, -45.5) * mm, v(-35.16, -46.17) * mm, v(-34.2, -46.8) * mm]});
            skFitSpline(sketch, "E652", {"points": [v(-34.2, -46.8) * mm, v(-33.32, -47.38) * mm, v(-32.43, -47.93) * mm, v(-31.53, -48.46) * mm]});
            skFitSpline(sketch, "E653", {"points": [v(-31.53, -48.46) * mm, v(-30.62, -49) * mm, v(-29.7, -49.54) * mm, v(-28.78, -50.05) * mm]});
            skFitSpline(sketch, "E654", {"points": [v(-28.78, -50.05) * mm, v(-28.1, -50.43) * mm, v(-27.4, -50.8) * mm, v(-26.7, -51.17) * mm]});
            skLineSegment(sketch, "E655", {"start": v(-51.35, -29.34) * mm, "end": v(-47.71, -34.36) * mm});
            skLineSegment(sketch, "E656", {"start": v(-47.71, -34.36) * mm, "end": v(-44.4, -38.11) * mm});
            skLineSegment(sketch, "E657", {"start": v(-44.4, -38.11) * mm, "end": v(-40.06, -42.28) * mm});
            skLineSegment(sketch, "E658", {"start": v(-40.06, -42.28) * mm, "end": v(-37.01, -44.8) * mm});
            skFitSpline(sketch, "E659", {"points": [v(-24, -52.37) * mm, v(-22.64, -52.92) * mm, v(-21.26, -53.43) * mm, v(-19.86, -53.87) * mm]});
            skFitSpline(sketch, "E660", {"points": [v(-19.86, -53.87) * mm, v(-18.92, -54.17) * mm, v(-17.98, -54.44) * mm, v(-17.04, -54.72) * mm]});
            skFitSpline(sketch, "E661", {"points": [v(-17.04, -54.72) * mm, v(-15.98, -55.04) * mm, v(-14.92, -55.36) * mm, v(-13.87, -55.69) * mm]});
            skFitSpline(sketch, "E662", {"points": [v(-13.87, -55.69) * mm, v(-12.86, -55.82) * mm, v(-11.86, -55.96) * mm, v(-10.86, -56.11) * mm]});
            skFitSpline(sketch, "E663", {"points": [v(-10.86, -56.11) * mm, v(-9.5, -56.32) * mm, v(-8.15, -56.55) * mm, v(-6.8, -56.8) * mm]});
            skLineSegment(sketch, "E664", {"start": v(-26.7, -51.17) * mm, "end": v(-24, -52.37) * mm});
            skFitSpline(sketch, "E665", {"points": [v(4.2, -57.16) * mm, v(5.57, -57.02) * mm, v(6.92, -56.86) * mm, v(8.27, -56.65) * mm]});
            skFitSpline(sketch, "E666", {"points": [v(8.27, -56.65) * mm, v(9.46, -56.48) * mm, v(10.64, -56.27) * mm, v(11.82, -56.04) * mm]});
            skFitSpline(sketch, "E667", {"points": [v(11.82, -56.04) * mm, v(13.4, -55.72) * mm, v(14.97, -55.36) * mm, v(16.53, -54.95) * mm]});
            skLineSegment(sketch, "E668", {"start": v(-6.8, -56.8) * mm, "end": v(-3.17, -57.08) * mm});
            skLineSegment(sketch, "E669", {"start": v(-3.17, -57.08) * mm, "end": v(4.2, -57.16) * mm});
            skFitSpline(sketch, "E670", {"points": [v(20.78, -53.56) * mm, v(22.2, -53.03) * mm, v(23.58, -52.45) * mm, v(24.96, -51.83) * mm]});
            skFitSpline(sketch, "E671", {"points": [v(24.96, -51.83) * mm, v(26.22, -51.25) * mm, v(27.47, -50.65) * mm, v(28.7, -50) * mm]});
            skLineSegment(sketch, "E672", {"start": v(16.53, -54.95) * mm, "end": v(20.78, -53.56) * mm});
            skFitSpline(sketch, "E673", {"points": [v(31.95, -48.16) * mm, v(32.81, -47.59) * mm, v(33.66, -47) * mm, v(34.5, -46.38) * mm]});
            skFitSpline(sketch, "E674", {"points": [v(34.5, -46.38) * mm, v(35.27, -45.81) * mm, v(36.02, -45.23) * mm, v(36.78, -44.64) * mm]});
            skFitSpline(sketch, "E675", {"points": [v(36.78, -44.64) * mm, v(37.64, -43.97) * mm, v(38.5, -43.3) * mm, v(39.37, -42.63) * mm]});
            skLineSegment(sketch, "E676", {"start": v(28.7, -50) * mm, "end": v(31.95, -48.16) * mm});
            skFitSpline(sketch, "E677", {"points": [v(42.42, -39.93) * mm, v(43.28, -39.08) * mm, v(44.12, -38.2) * mm, v(44.93, -37.3) * mm]});
            skFitSpline(sketch, "E678", {"points": [v(44.93, -37.3) * mm, v(45.75, -36.38) * mm, v(46.55, -35.44) * mm, v(47.32, -34.48) * mm]});
            skFitSpline(sketch, "E679", {"points": [v(47.32, -34.48) * mm, v(48.08, -33.54) * mm, v(48.81, -32.59) * mm, v(49.53, -31.62) * mm]});
            skFitSpline(sketch, "E680", {"points": [v(49.53, -31.62) * mm, v(50.19, -30.64) * mm, v(50.83, -29.65) * mm, v(51.46, -28.65) * mm]});
            skFitSpline(sketch, "E681", {"points": [v(51.46, -28.65) * mm, v(52.2, -27.46) * mm, v(52.9, -26.27) * mm, v(53.58, -25.05) * mm]});
            skLineSegment(sketch, "E682", {"start": v(39.37, -42.63) * mm, "end": v(42.42, -39.93) * mm});
            skFitSpline(sketch, "E683", {"points": [v(59.38, -5.08) * mm, v(59.5, -4.07) * mm, v(59.53, -3.05) * mm, v(59.53, -2.03) * mm]});
            skLineSegment(sketch, "E684", {"start": v(53.58, -25.05) * mm, "end": v(55.4, -21.3) * mm});
            skLineSegment(sketch, "E685", {"start": v(55.4, -21.3) * mm, "end": v(56.83, -17.25) * mm});
            skLineSegment(sketch, "E686", {"start": v(56.83, -17.25) * mm, "end": v(58.34, -11.92) * mm});
            skLineSegment(sketch, "E687", {"start": v(58.34, -11.92) * mm, "end": v(59.15, -7.01) * mm});
            skLineSegment(sketch, "E688", {"start": v(59.15, -7.01) * mm, "end": v(59.38, -5.08) * mm});
            skFitSpline(sketch, "E689", {"points": [v(59, 9.8) * mm, v(58.77, 10.99) * mm, v(58.51, 12.17) * mm, v(58.22, 13.35) * mm]});
            skFitSpline(sketch, "E690", {"points": [v(58.22, 13.35) * mm, v(57.93, 14.52) * mm, v(57.6, 15.68) * mm, v(57.25, 16.83) * mm]});
            skFitSpline(sketch, "E691", {"points": [v(57.25, 16.83) * mm, v(56.87, 17.9) * mm, v(56.47, 18.97) * mm, v(56.06, 20.03) * mm]});
            skFitSpline(sketch, "E692", {"points": [v(56.06, 20.03) * mm, v(55.65, 21.07) * mm, v(55.22, 22.1) * mm, v(54.78, 23.12) * mm]});
            skLineSegment(sketch, "E693", {"start": v(59.53, -2.03) * mm, "end": v(59.57, 4.3) * mm});
            skLineSegment(sketch, "E694", {"start": v(59.57, 4.3) * mm, "end": v(59.15, 8.75) * mm});
            skLineSegment(sketch, "E695", {"start": v(59.15, 8.75) * mm, "end": v(59, 9.8) * mm});
            skFitSpline(sketch, "E696", {"points": [v(42.15, 40.86) * mm, v(41.17, 41.8) * mm, v(40.16, 42.71) * mm, v(39.13, 43.6) * mm]});
            skFitSpline(sketch, "E697", {"points": [v(39.13, 43.6) * mm, v(38.07, 44.52) * mm, v(36.97, 45.4) * mm, v(35.85, 46.26) * mm]});
            skFitSpline(sketch, "E698", {"points": [v(35.85, 46.26) * mm, v(34.84, 46.98) * mm, v(33.8, 47.66) * mm, v(32.76, 48.31) * mm]});
            skFitSpline(sketch, "E699", {"points": [v(32.76, 48.31) * mm, v(31.56, 49.06) * mm, v(30.34, 49.77) * mm, v(29.09, 50.44) * mm]});
            skFitSpline(sketch, "E700", {"points": [v(29.09, 50.44) * mm, v(27.65, 51.18) * mm, v(26.2, 51.9) * mm, v(24.72, 52.56) * mm]});
            skFitSpline(sketch, "E701", {"points": [v(24.72, 52.56) * mm, v(23.6, 53.07) * mm, v(22.47, 53.56) * mm, v(21.32, 54.03) * mm]});
            skLineSegment(sketch, "E702", {"start": v(54.78, 23.12) * mm, "end": v(52.27, 28.03) * mm});
            skLineSegment(sketch, "E703", {"start": v(52.27, 28.03) * mm, "end": v(49.26, 32.78) * mm});
            skLineSegment(sketch, "E704", {"start": v(49.26, 32.78) * mm, "end": v(45.74, 37.1) * mm});
            skLineSegment(sketch, "E705", {"start": v(45.74, 37.1) * mm, "end": v(42.15, 40.86) * mm});
            skFitSpline(sketch, "E706", {"points": [v(16.96, 55.54) * mm, v(15.51, 55.9) * mm, v(14.06, 56.22) * mm, v(12.6, 56.5) * mm]});
            skFitSpline(sketch, "E707", {"points": [v(12.6, 56.5) * mm, v(10.95, 56.81) * mm, v(9.3, 57.07) * mm, v(7.65, 57.28) * mm]});
            skLineSegment(sketch, "E708", {"start": v(21.32, 54.03) * mm, "end": v(16.96, 55.54) * mm});
            skFitSpline(sketch, "E709", {"points": [v(4.33, 57.55) * mm, v(2.76, 57.67) * mm, v(1.18, 57.76) * mm, v(-0.39, 57.66) * mm]});
            skLineSegment(sketch, "E710", {"start": v(7.65, 57.28) * mm, "end": v(4.33, 57.55) * mm});
            skFitSpline(sketch, "E711", {"points": [v(-22.49, 53.49) * mm, v(-24, 52.87) * mm, v(-25.52, 52.21) * mm, v(-27, 51.52) * mm]});
            skFitSpline(sketch, "E712", {"points": [v(-27, 51.52) * mm, v(-27.97, 51.07) * mm, v(-28.92, 50.6) * mm, v(-29.86, 50.13) * mm]});
            skLineSegment(sketch, "E713", {"start": v(-0.39, 57.66) * mm, "end": v(-5.26, 57.62) * mm});
            skLineSegment(sketch, "E714", {"start": v(-5.26, 57.62) * mm, "end": v(-11.44, 56.73) * mm});
            skLineSegment(sketch, "E715", {"start": v(-11.44, 56.73) * mm, "end": v(-16.96, 55.42) * mm});
            skLineSegment(sketch, "E716", {"start": v(-16.96, 55.42) * mm, "end": v(-22.49, 53.49) * mm});
            skFitSpline(sketch, "E717", {"points": [v(17.46, 30.43) * mm, v(18.84, 30.96) * mm, v(20.23, 31.46) * mm, v(21.63, 31.93) * mm]});
            skFitSpline(sketch, "E718", {"points": [v(21.63, 31.93) * mm, v(22.35, 32.17) * mm, v(23.07, 32.4) * mm, v(23.8, 32.63) * mm]});
            skLineSegment(sketch, "E719", {"start": v(-6.96, 32.09) * mm, "end": v(-4.71, 38.77) * mm});
            skLineSegment(sketch, "E720", {"start": v(-4.71, 38.77) * mm, "end": v(-10.32, 43.6) * mm});
            skLineSegment(sketch, "E721", {"start": v(-10.32, 43.6) * mm, "end": v(-3.01, 44.06) * mm});
            skLineSegment(sketch, "E722", {"start": v(-3.01, 44.06) * mm, "end": v(-0.04, 50.75) * mm});
            skLineSegment(sketch, "E723", {"start": v(-0.04, 50.75) * mm, "end": v(2.9, 44.26) * mm});
            skLineSegment(sketch, "E724", {"start": v(2.9, 44.26) * mm, "end": v(10.28, 43.75) * mm});
            skLineSegment(sketch, "E725", {"start": v(10.28, 43.75) * mm, "end": v(4.56, 38.54) * mm});
            skLineSegment(sketch, "E726", {"start": v(4.56, 38.54) * mm, "end": v(7.26, 32.36) * mm});
            skLineSegment(sketch, "E727", {"start": v(7.26, 32.36) * mm, "end": v(12.1, 35.3) * mm});
            skLineSegment(sketch, "E728", {"start": v(12.1, 35.3) * mm, "end": v(15.41, 36.6) * mm});
            skLineSegment(sketch, "E729", {"start": v(15.41, 36.6) * mm, "end": v(17.65, 37.22) * mm});
            skLineSegment(sketch, "E730", {"start": v(17.65, 37.22) * mm, "end": v(19.28, 37.26) * mm});
            skLineSegment(sketch, "E731", {"start": v(19.28, 37.26) * mm, "end": v(18.5, 35.33) * mm});
            skLineSegment(sketch, "E732", {"start": v(18.5, 35.33) * mm, "end": v(17.77, 32.97) * mm});
            skLineSegment(sketch, "E733", {"start": v(17.77, 32.97) * mm, "end": v(17.46, 30.43) * mm});
            skFitSpline(sketch, "E734", {"points": [v(14.18, 24.01) * mm, v(13.13, 24.27) * mm, v(12.09, 24.52) * mm, v(11.05, 24.78) * mm]});
            skFitSpline(sketch, "E735", {"points": [v(11.05, 24.78) * mm, v(9.89, 25.08) * mm, v(8.73, 25.37) * mm, v(7.57, 25.67) * mm]});
            skLineSegment(sketch, "E736", {"start": v(23.8, 32.63) * mm, "end": v(25.88, 32.67) * mm});
            skLineSegment(sketch, "E737", {"start": v(25.88, 32.67) * mm, "end": v(22.83, 27.37) * mm});
            skLineSegment(sketch, "E738", {"start": v(22.83, 27.37) * mm, "end": v(21.71, 24.78) * mm});
            skLineSegment(sketch, "E739", {"start": v(21.71, 24.78) * mm, "end": v(21.13, 22.62) * mm});
            skLineSegment(sketch, "E740", {"start": v(21.13, 22.62) * mm, "end": v(20.98, 21.58) * mm});
            skLineSegment(sketch, "E741", {"start": v(20.98, 21.58) * mm, "end": v(14.18, 24.01) * mm});
            skFitSpline(sketch, "E742", {"points": [v(-6.45, 25.6) * mm, v(-7.45, 25.42) * mm, v(-8.44, 25.23) * mm, v(-9.43, 25.02) * mm]});
            skFitSpline(sketch, "E743", {"points": [v(-9.43, 25.02) * mm, v(-10.87, 24.7) * mm, v(-12.3, 24.36) * mm, v(-13.72, 23.97) * mm]});
            skLineSegment(sketch, "E744", {"start": v(7.57, 25.67) * mm, "end": v(3.7, 26.14) * mm});
            skLineSegment(sketch, "E745", {"start": v(3.7, 26.14) * mm, "end": v(-2.47, 26.1) * mm});
            skLineSegment(sketch, "E746", {"start": v(-2.47, 26.1) * mm, "end": v(-6.45, 25.6) * mm});
            skFitSpline(sketch, "E747", {"points": [v(-21.6, 31.85) * mm, v(-20.75, 31.5) * mm, v(-19.9, 31.16) * mm, v(-19.05, 30.81) * mm]});
            skFitSpline(sketch, "E748", {"points": [v(-19.05, 30.81) * mm, v(-18.44, 30.57) * mm, v(-17.84, 30.32) * mm, v(-17.23, 30.08) * mm]});
            skLineSegment(sketch, "E749", {"start": v(-13.72, 23.97) * mm, "end": v(-20.52, 21.35) * mm});
            skLineSegment(sketch, "E750", {"start": v(-20.52, 21.35) * mm, "end": v(-21.17, 23.66) * mm});
            skLineSegment(sketch, "E751", {"start": v(-21.17, 23.66) * mm, "end": v(-22.02, 26.06) * mm});
            skLineSegment(sketch, "E752", {"start": v(-22.02, 26.06) * mm, "end": v(-24.88, 30.93) * mm});
            skLineSegment(sketch, "E753", {"start": v(-24.88, 30.93) * mm, "end": v(-25.96, 32.28) * mm});
            skLineSegment(sketch, "E754", {"start": v(-25.96, 32.28) * mm, "end": v(-24.26, 32.47) * mm});
            skLineSegment(sketch, "E755", {"start": v(-24.26, 32.47) * mm, "end": v(-21.6, 31.85) * mm});
            skFitSpline(sketch, "E756", {"points": [v(-17.77, 33.79) * mm, v(-18, 34.28) * mm, v(-18.24, 34.77) * mm, v(-18.47, 35.25) * mm]});
            skFitSpline(sketch, "E757", {"points": [v(-18.47, 35.25) * mm, v(-18.75, 35.85) * mm, v(-19.03, 36.44) * mm, v(-19.32, 37.03) * mm]});
            skLineSegment(sketch, "E758", {"start": v(-17.23, 30.08) * mm, "end": v(-17.15, 31.7) * mm});
            skLineSegment(sketch, "E759", {"start": v(-17.15, 31.7) * mm, "end": v(-17.77, 33.79) * mm});
            skFitSpline(sketch, "E760", {"points": [v(-14.18, 35.95) * mm, v(-13.24, 35.45) * mm, v(-12.3, 34.95) * mm, v(-11.36, 34.44) * mm]});
            skFitSpline(sketch, "E761", {"points": [v(-11.36, 34.44) * mm, v(-9.9, 33.66) * mm, v(-8.42, 32.87) * mm, v(-6.96, 32.09) * mm]});
            skLineSegment(sketch, "E762", {"start": v(-19.32, 37.03) * mm, "end": v(-19.36, 37.42) * mm});
            skLineSegment(sketch, "E763", {"start": v(-19.36, 37.42) * mm, "end": v(-17.58, 37.22) * mm});
            skLineSegment(sketch, "E764", {"start": v(-17.58, 37.22) * mm, "end": v(-14.18, 35.95) * mm});
            skLineSegment(sketch, "E765", {"start": v(-5.37, 30.81) * mm, "end": v(-4.83, 30.39) * mm});
            skLineSegment(sketch, "E766", {"start": v(-4.83, 30.39) * mm, "end": v(4.75, 30.5) * mm});
            skLineSegment(sketch, "E767", {"start": v(4.75, 30.5) * mm, "end": v(5.25, 30.85) * mm});
            skLineSegment(sketch, "E768", {"start": v(5.25, 30.85) * mm, "end": v(4.98, 31.28) * mm});
            skLineSegment(sketch, "E769", {"start": v(4.98, 31.28) * mm, "end": v(-0.23, 34.87) * mm});
            skLineSegment(sketch, "E770", {"start": v(-0.23, 34.87) * mm, "end": v(-5.06, 31.4) * mm});
            skLineSegment(sketch, "E771", {"start": v(-5.06, 31.4) * mm, "end": v(-5.37, 30.81) * mm});
            skFitSpline(sketch, "E772", {"points": [v(6.22, 17.83) * mm, v(5.78, 17.74) * mm, v(5.34, 17.65) * mm, v(4.9, 17.56) * mm]});
            skFitSpline(sketch, "E773", {"points": [v(4.9, 17.56) * mm, v(4.39, 17.45) * mm, v(3.87, 17.33) * mm, v(3.36, 17.21) * mm]});
            skFitSpline(sketch, "E774", {"points": [v(3.36, 17.21) * mm, v(3.3, 17.2) * mm, v(3.26, 17.19) * mm, v(3.2, 17.17) * mm]});
            skLineSegment(sketch, "E775", {"start": v(-2.36, 23.86) * mm, "end": v(2.93, 23.9) * mm});
            skLineSegment(sketch, "E776", {"start": v(2.93, 23.9) * mm, "end": v(4.71, 23.55) * mm});
            skLineSegment(sketch, "E777", {"start": v(4.71, 23.55) * mm, "end": v(6.6, 22.81) * mm});
            skLineSegment(sketch, "E778", {"start": v(6.6, 22.81) * mm, "end": v(8.42, 21.7) * mm});
            skLineSegment(sketch, "E779", {"start": v(8.42, 21.7) * mm, "end": v(9.62, 20.5) * mm});
            skLineSegment(sketch, "E780", {"start": v(9.62, 20.5) * mm, "end": v(10.4, 18.95) * mm});
            skLineSegment(sketch, "E781", {"start": v(10.4, 18.95) * mm, "end": v(10.55, 17.64) * mm});
            skLineSegment(sketch, "E782", {"start": v(10.55, 17.64) * mm, "end": v(10.24, 17.48) * mm});
            skLineSegment(sketch, "E783", {"start": v(10.24, 17.48) * mm, "end": v(9, 17.9) * mm});
            skLineSegment(sketch, "E784", {"start": v(9, 17.9) * mm, "end": v(6.22, 17.83) * mm});
            skFitSpline(sketch, "E785", {"points": [v(1.43, 15.05) * mm, v(1.4, 14.68) * mm, v(1.37, 14.3) * mm, v(1.35, 13.93) * mm]});
            skFitSpline(sketch, "E786", {"points": [v(1.35, 13.93) * mm, v(1.3, 13.05) * mm, v(1.28, 12.18) * mm, v(1.27, 11.3) * mm]});
            skLineSegment(sketch, "E787", {"start": v(3.2, 17.17) * mm, "end": v(2.28, 16.25) * mm});
            skLineSegment(sketch, "E788", {"start": v(2.28, 16.25) * mm, "end": v(1.43, 15.05) * mm});
            skFitSpline(sketch, "E789", {"points": [v(2.4, -3.56) * mm, v(1.96, -3.7) * mm, v(1.48, -3.73) * mm, v(1, -3.73) * mm]});
            skLineSegment(sketch, "E790", {"start": v(1.27, 11.3) * mm, "end": v(1.54, 10.41) * mm});
            skLineSegment(sketch, "E791", {"start": v(1.54, 10.41) * mm, "end": v(1.9, 9.72) * mm});
            skLineSegment(sketch, "E792", {"start": v(1.9, 9.72) * mm, "end": v(2.55, 9.56) * mm});
            skLineSegment(sketch, "E793", {"start": v(2.55, 9.56) * mm, "end": v(3.05, 10.1) * mm});
            skLineSegment(sketch, "E794", {"start": v(3.05, 10.1) * mm, "end": v(3.78, 11.07) * mm});
            skLineSegment(sketch, "E795", {"start": v(3.78, 11.07) * mm, "end": v(4.17, 11.34) * mm});
            skLineSegment(sketch, "E796", {"start": v(4.17, 11.34) * mm, "end": v(5.02, 11.19) * mm});
            skLineSegment(sketch, "E797", {"start": v(5.02, 11.19) * mm, "end": v(5.95, 10.88) * mm});
            skLineSegment(sketch, "E798", {"start": v(5.95, 10.88) * mm, "end": v(7.88, 10.8) * mm});
            skLineSegment(sketch, "E799", {"start": v(7.88, 10.8) * mm, "end": v(8.88, 11.03) * mm});
            skLineSegment(sketch, "E800", {"start": v(8.88, 11.03) * mm, "end": v(9.46, 11.42) * mm});
            skLineSegment(sketch, "E801", {"start": v(9.46, 11.42) * mm, "end": v(9.93, 11.19) * mm});
            skLineSegment(sketch, "E802", {"start": v(9.93, 11.19) * mm, "end": v(10.5, 10.6) * mm});
            skLineSegment(sketch, "E803", {"start": v(10.5, 10.6) * mm, "end": v(10.7, 8.83) * mm});
            skLineSegment(sketch, "E804", {"start": v(10.7, 8.83) * mm, "end": v(10.44, 6.92) * mm});
            skLineSegment(sketch, "E805", {"start": v(10.44, 6.92) * mm, "end": v(8.86, 2.49) * mm});
            skLineSegment(sketch, "E806", {"start": v(8.86, 2.49) * mm, "end": v(7.17, 0.14) * mm});
            skLineSegment(sketch, "E807", {"start": v(7.17, 0.14) * mm, "end": v(3.64, -2.88) * mm});
            skLineSegment(sketch, "E808", {"start": v(3.64, -2.88) * mm, "end": v(2.4, -3.56) * mm});
            skFitSpline(sketch, "E809", {"points": [v(-10.16, 18.91) * mm, v(-10.02, 19.15) * mm, v(-9.87, 19.38) * mm, v(-9.72, 19.61) * mm]});
            skFitSpline(sketch, "E810", {"points": [v(-9.72, 19.61) * mm, v(-9.46, 20.01) * mm, v(-9.2, 20.4) * mm, v(-8.94, 20.8) * mm]});
            skLineSegment(sketch, "E811", {"start": v(1, -3.73) * mm, "end": v(-0.39, -3.73) * mm});
            skLineSegment(sketch, "E812", {"start": v(-0.39, -3.73) * mm, "end": v(-2.28, -3.46) * mm});
            skLineSegment(sketch, "E813", {"start": v(-2.28, -3.46) * mm, "end": v(-3.88, -2.97) * mm});
            skLineSegment(sketch, "E814", {"start": v(-3.88, -2.97) * mm, "end": v(-6.2, -1.34) * mm});
            skLineSegment(sketch, "E815", {"start": v(-6.2, -1.34) * mm, "end": v(-7.39, -0.18) * mm});
            skLineSegment(sketch, "E816", {"start": v(-7.39, -0.18) * mm, "end": v(-8.64, 1.42) * mm});
            skLineSegment(sketch, "E817", {"start": v(-8.64, 1.42) * mm, "end": v(-9.77, 3.5) * mm});
            skLineSegment(sketch, "E818", {"start": v(-9.77, 3.5) * mm, "end": v(-10.64, 5.92) * mm});
            skLineSegment(sketch, "E819", {"start": v(-10.64, 5.92) * mm, "end": v(-10.9, 8.48) * mm});
            skLineSegment(sketch, "E820", {"start": v(-10.9, 8.48) * mm, "end": v(-10.66, 10.64) * mm});
            skLineSegment(sketch, "E821", {"start": v(-10.66, 10.64) * mm, "end": v(-10, 11.46) * mm});
            skLineSegment(sketch, "E822", {"start": v(-10, 11.46) * mm, "end": v(-8.93, 11.22) * mm});
            skLineSegment(sketch, "E823", {"start": v(-8.93, 11.22) * mm, "end": v(-7.46, 10.8) * mm});
            skLineSegment(sketch, "E824", {"start": v(-7.46, 10.8) * mm, "end": v(-6.41, 10.95) * mm});
            skLineSegment(sketch, "E825", {"start": v(-6.41, 10.95) * mm, "end": v(-5.37, 11.19) * mm});
            skLineSegment(sketch, "E826", {"start": v(-5.37, 11.19) * mm, "end": v(-4.29, 11.19) * mm});
            skLineSegment(sketch, "E827", {"start": v(-4.29, 11.19) * mm, "end": v(-3.29, 10.68) * mm});
            skLineSegment(sketch, "E828", {"start": v(-3.29, 10.68) * mm, "end": v(-2.55, 10.95) * mm});
            skLineSegment(sketch, "E829", {"start": v(-2.55, 10.95) * mm, "end": v(-2.13, 11.46) * mm});
            skLineSegment(sketch, "E830", {"start": v(-2.13, 11.46) * mm, "end": v(-1.74, 12.38) * mm});
            skLineSegment(sketch, "E831", {"start": v(-1.74, 12.38) * mm, "end": v(-2.01, 14.62) * mm});
            skLineSegment(sketch, "E832", {"start": v(-2.01, 14.62) * mm, "end": v(-2.32, 16.13) * mm});
            skLineSegment(sketch, "E833", {"start": v(-2.32, 16.13) * mm, "end": v(-3.63, 17.33) * mm});
            skLineSegment(sketch, "E834", {"start": v(-3.63, 17.33) * mm, "end": v(-5.8, 17.87) * mm});
            skLineSegment(sketch, "E835", {"start": v(-5.8, 17.87) * mm, "end": v(-9.39, 17.9) * mm});
            skLineSegment(sketch, "E836", {"start": v(-9.39, 17.9) * mm, "end": v(-10.05, 18.14) * mm});
            skLineSegment(sketch, "E837", {"start": v(-10.05, 18.14) * mm, "end": v(-10.16, 18.91) * mm});
            skLineSegment(sketch, "E838", {"start": v(-8.94, 20.8) * mm, "end": v(-7.13, 22.28) * mm});
            skLineSegment(sketch, "E839", {"start": v(-7.13, 22.28) * mm, "end": v(-5.06, 23.16) * mm});
            skLineSegment(sketch, "E840", {"start": v(-5.06, 23.16) * mm, "end": v(-2.36, 23.86) * mm});
            skLineSegment(sketch, "E841", {"start": v(4.69, 14.71) * mm, "end": v(5.29, 15.1) * mm});
            skLineSegment(sketch, "E842", {"start": v(5.29, 15.1) * mm, "end": v(6.46, 15.37) * mm});
            skLineSegment(sketch, "E843", {"start": v(6.46, 15.37) * mm, "end": v(7.67, 15.53) * mm});
            skLineSegment(sketch, "E844", {"start": v(7.67, 15.53) * mm, "end": v(9.17, 15.5) * mm});
            skLineSegment(sketch, "E845", {"start": v(9.17, 15.5) * mm, "end": v(10.26, 14.99) * mm});
            skLineSegment(sketch, "E846", {"start": v(10.26, 14.99) * mm, "end": v(10.5, 14.06) * mm});
            skLineSegment(sketch, "E847", {"start": v(10.5, 14.06) * mm, "end": v(10.1, 13.4) * mm});
            skLineSegment(sketch, "E848", {"start": v(10.1, 13.4) * mm, "end": v(9.28, 13.57) * mm});
            skLineSegment(sketch, "E849", {"start": v(9.28, 13.57) * mm, "end": v(8.16, 13.92) * mm});
            skLineSegment(sketch, "E850", {"start": v(8.16, 13.92) * mm, "end": v(7.1, 14.11) * mm});
            skLineSegment(sketch, "E851", {"start": v(7.1, 14.11) * mm, "end": v(5.75, 14.09) * mm});
            skLineSegment(sketch, "E852", {"start": v(5.75, 14.09) * mm, "end": v(5.04, 13.79) * mm});
            skLineSegment(sketch, "E853", {"start": v(5.04, 13.79) * mm, "end": v(4.58, 13.68) * mm});
            skLineSegment(sketch, "E854", {"start": v(4.58, 13.68) * mm, "end": v(4.41, 14.22) * mm});
            skLineSegment(sketch, "E855", {"start": v(4.41, 14.22) * mm, "end": v(4.69, 14.71) * mm});
            skFitSpline(sketch, "E856", {"points": [v(-8.89, 13.81) * mm, v(-9.09, 13.67) * mm, v(-9.29, 13.53) * mm, v(-9.5, 13.4) * mm]});
            skFitSpline(sketch, "E857", {"points": [v(-9.5, 13.4) * mm, v(-9.6, 13.33) * mm, v(-9.73, 13.26) * mm, v(-9.85, 13.18) * mm]});
            skLineSegment(sketch, "E858", {"start": v(-9.19, 15.64) * mm, "end": v(-7.06, 15.59) * mm});
            skLineSegment(sketch, "E859", {"start": v(-7.06, 15.59) * mm, "end": v(-5.86, 15.15) * mm});
            skLineSegment(sketch, "E860", {"start": v(-5.86, 15.15) * mm, "end": v(-5.04, 14.6) * mm});
            skLineSegment(sketch, "E861", {"start": v(-5.04, 14.6) * mm, "end": v(-4.55, 14.11) * mm});
            skLineSegment(sketch, "E862", {"start": v(-4.55, 14.11) * mm, "end": v(-4.5, 13.51) * mm});
            skLineSegment(sketch, "E863", {"start": v(-4.5, 13.51) * mm, "end": v(-4.98, 13.54) * mm});
            skLineSegment(sketch, "E864", {"start": v(-4.98, 13.54) * mm, "end": v(-5.37, 13.73) * mm});
            skLineSegment(sketch, "E865", {"start": v(-5.37, 13.73) * mm, "end": v(-5.75, 13.7) * mm});
            skLineSegment(sketch, "E866", {"start": v(-5.75, 13.7) * mm, "end": v(-6, 13.92) * mm});
            skLineSegment(sketch, "E867", {"start": v(-6, 13.92) * mm, "end": v(-6.76, 13.98) * mm});
            skLineSegment(sketch, "E868", {"start": v(-6.76, 13.98) * mm, "end": v(-6.95, 14.2) * mm});
            skLineSegment(sketch, "E869", {"start": v(-6.95, 14.2) * mm, "end": v(-8.15, 14.14) * mm});
            skLineSegment(sketch, "E870", {"start": v(-8.15, 14.14) * mm, "end": v(-8.89, 13.81) * mm});
            skFitSpline(sketch, "E871", {"points": [v(-9.87, 15.37) * mm, v(-9.75, 15.41) * mm, v(-9.64, 15.46) * mm, v(-9.52, 15.5) * mm]});
            skFitSpline(sketch, "E872", {"points": [v(-9.52, 15.5) * mm, v(-9.4, 15.55) * mm, v(-9.3, 15.6) * mm, v(-9.19, 15.64) * mm]});
            skLineSegment(sketch, "E873", {"start": v(-9.85, 13.18) * mm, "end": v(-10.26, 13.43) * mm});
            skLineSegment(sketch, "E874", {"start": v(-10.26, 13.43) * mm, "end": v(-10.23, 15.02) * mm});
            skLineSegment(sketch, "E875", {"start": v(-10.23, 15.02) * mm, "end": v(-9.87, 15.37) * mm});
            skLineSegment(sketch, "E876", {"start": v(0.8, 5.92) * mm, "end": v(1.03, 5.95) * mm});
            skLineSegment(sketch, "E877", {"start": v(1.03, 5.95) * mm, "end": v(1.68, 6.22) * mm});
            skLineSegment(sketch, "E878", {"start": v(1.68, 6.22) * mm, "end": v(2.28, 6.55) * mm});
            skLineSegment(sketch, "E879", {"start": v(2.28, 6.55) * mm, "end": v(2.34, 6.98) * mm});
            skLineSegment(sketch, "E880", {"start": v(2.34, 6.98) * mm, "end": v(1.98, 7.28) * mm});
            skLineSegment(sketch, "E881", {"start": v(1.98, 7.28) * mm, "end": v(1.03, 7.64) * mm});
            skLineSegment(sketch, "E882", {"start": v(1.03, 7.64) * mm, "end": v(-0.58, 7.61) * mm});
            skLineSegment(sketch, "E883", {"start": v(-0.58, 7.61) * mm, "end": v(-1.43, 7.4) * mm});
            skLineSegment(sketch, "E884", {"start": v(-1.43, 7.4) * mm, "end": v(-2.06, 7.04) * mm});
            skLineSegment(sketch, "E885", {"start": v(-2.06, 7.04) * mm, "end": v(-2.36, 6.74) * mm});
            skLineSegment(sketch, "E886", {"start": v(-2.36, 6.74) * mm, "end": v(-2.36, 6.27) * mm});
            skLineSegment(sketch, "E887", {"start": v(-2.36, 6.27) * mm, "end": v(-1.87, 5.9) * mm});
            skLineSegment(sketch, "E888", {"start": v(-1.87, 5.9) * mm, "end": v(0.8, 5.92) * mm});
            skFitSpline(sketch, "E889", {"points": [v(35.91, 41.16) * mm, v(34.54, 42.18) * mm, v(33.15, 43.16) * mm, v(31.73, 44.1) * mm]});
            skFitSpline(sketch, "E890", {"points": [v(31.73, 44.1) * mm, v(30.43, 44.98) * mm, v(29.11, 45.82) * mm, v(27.77, 46.62) * mm]});
            skLineSegment(sketch, "E891", {"start": v(47.63, -5.34) * mm, "end": v(50.06, -6.35) * mm});
            skLineSegment(sketch, "E892", {"start": v(50.06, -6.35) * mm, "end": v(51.48, -6.76) * mm});
            skLineSegment(sketch, "E893", {"start": v(51.48, -6.76) * mm, "end": v(54.32, -6.9) * mm});
            skLineSegment(sketch, "E894", {"start": v(54.32, -6.9) * mm, "end": v(55.17, -6.43) * mm});
            skLineSegment(sketch, "E895", {"start": v(55.17, -6.43) * mm, "end": v(55.34, -1.68) * mm});
            skLineSegment(sketch, "E896", {"start": v(55.34, -1.68) * mm, "end": v(53.53, -2.11) * mm});
            skLineSegment(sketch, "E897", {"start": v(53.53, -2.11) * mm, "end": v(50.77, -2.14) * mm});
            skLineSegment(sketch, "E898", {"start": v(50.77, -2.14) * mm, "end": v(47.69, -1.32) * mm});
            skLineSegment(sketch, "E899", {"start": v(47.69, -1.32) * mm, "end": v(44.98, 0.04) * mm});
            skLineSegment(sketch, "E900", {"start": v(44.98, 0.04) * mm, "end": v(41.98, 1.38) * mm});
            skLineSegment(sketch, "E901", {"start": v(41.98, 1.38) * mm, "end": v(39.76, 1.88) * mm});
            skLineSegment(sketch, "E902", {"start": v(39.76, 1.88) * mm, "end": v(38.23, 1.9) * mm});
            skLineSegment(sketch, "E903", {"start": v(38.23, 1.9) * mm, "end": v(36.9, 5.13) * mm});
            skLineSegment(sketch, "E904", {"start": v(36.9, 5.13) * mm, "end": v(39.03, 5.32) * mm});
            skLineSegment(sketch, "E905", {"start": v(39.03, 5.32) * mm, "end": v(41.3, 5.1) * mm});
            skLineSegment(sketch, "E906", {"start": v(41.3, 5.1) * mm, "end": v(43.67, 4.06) * mm});
            skLineSegment(sketch, "E907", {"start": v(43.67, 4.06) * mm, "end": v(47.77, 2.1) * mm});
            skLineSegment(sketch, "E908", {"start": v(47.77, 2.1) * mm, "end": v(50.34, 1.11) * mm});
            skLineSegment(sketch, "E909", {"start": v(50.34, 1.11) * mm, "end": v(52.66, 1.14) * mm});
            skLineSegment(sketch, "E910", {"start": v(52.66, 1.14) * mm, "end": v(55.53, 2.4) * mm});
            skLineSegment(sketch, "E911", {"start": v(55.53, 2.4) * mm, "end": v(54.87, 8.76) * mm});
            skLineSegment(sketch, "E912", {"start": v(54.87, 8.76) * mm, "end": v(54.13, 12.67) * mm});
            skLineSegment(sketch, "E913", {"start": v(54.13, 12.67) * mm, "end": v(53.15, 16.5) * mm});
            skLineSegment(sketch, "E914", {"start": v(53.15, 16.5) * mm, "end": v(51.48, 20.67) * mm});
            skLineSegment(sketch, "E915", {"start": v(51.48, 20.67) * mm, "end": v(49.93, 23.95) * mm});
            skLineSegment(sketch, "E916", {"start": v(49.93, 23.95) * mm, "end": v(47.96, 27.47) * mm});
            skLineSegment(sketch, "E917", {"start": v(47.96, 27.47) * mm, "end": v(45.25, 31.54) * mm});
            skLineSegment(sketch, "E918", {"start": v(45.25, 31.54) * mm, "end": v(42.71, 34.6) * mm});
            skLineSegment(sketch, "E919", {"start": v(42.71, 34.6) * mm, "end": v(39.46, 37.99) * mm});
            skLineSegment(sketch, "E920", {"start": v(39.46, 37.99) * mm, "end": v(35.91, 41.16) * mm});
            skFitSpline(sketch, "E921", {"points": [v(21.93, 49.68) * mm, v(20.26, 50.25) * mm, v(18.59, 50.78) * mm, v(16.9, 51.27) * mm]});
            skFitSpline(sketch, "E922", {"points": [v(16.9, 51.27) * mm, v(15.6, 51.64) * mm, v(14.3, 51.98) * mm, v(13, 52.3) * mm]});
            skFitSpline(sketch, "E923", {"points": [v(13, 52.3) * mm, v(11.39, 52.6) * mm, v(9.77, 52.85) * mm, v(8.16, 53.07) * mm]});
            skFitSpline(sketch, "E924", {"points": [v(8.16, 53.07) * mm, v(6.63, 53.28) * mm, v(5.1, 53.46) * mm, v(3.57, 53.62) * mm]});
            skLineSegment(sketch, "E925", {"start": v(27.77, 46.62) * mm, "end": v(21.93, 49.68) * mm});
            skLineSegment(sketch, "E926", {"start": v(3.57, 53.62) * mm, "end": v(-4.3, 53.67) * mm});
            skLineSegment(sketch, "E927", {"start": v(-4.3, 53.67) * mm, "end": v(-7.52, 53.37) * mm});
            skLineSegment(sketch, "E928", {"start": v(-7.52, 53.37) * mm, "end": v(-11.54, 52.71) * mm});
            skLineSegment(sketch, "E929", {"start": v(-11.54, 52.71) * mm, "end": v(-17.41, 51.24) * mm});
            skLineSegment(sketch, "E930", {"start": v(-17.41, 51.24) * mm, "end": v(-21.76, 49.6) * mm});
            skLineSegment(sketch, "E931", {"start": v(-21.76, 49.6) * mm, "end": v(-25.85, 47.69) * mm});
            skLineSegment(sketch, "E932", {"start": v(-25.85, 47.69) * mm, "end": v(-30.58, 45.06) * mm});
            skLineSegment(sketch, "E933", {"start": v(-30.58, 45.06) * mm, "end": v(-34.7, 42.25) * mm});
            skLineSegment(sketch, "E934", {"start": v(-34.7, 42.25) * mm, "end": v(-37.68, 39.74) * mm});
            skLineSegment(sketch, "E935", {"start": v(-37.68, 39.74) * mm, "end": v(-39.79, 37.66) * mm});
            skLineSegment(sketch, "E936", {"start": v(-39.79, 37.66) * mm, "end": v(-41.94, 35.2) * mm});
            skLineSegment(sketch, "E937", {"start": v(-41.94, 35.2) * mm, "end": v(-44.18, 32.6) * mm});
            skLineSegment(sketch, "E938", {"start": v(-44.18, 32.6) * mm, "end": v(-46.64, 29.11) * mm});
            skLineSegment(sketch, "E939", {"start": v(-46.64, 29.11) * mm, "end": v(-49.24, 24.66) * mm});
            skFitSpline(sketch, "E940", {"points": [v(-53.94, 12.78) * mm, v(-54.2, 11.43) * mm, v(-54.45, 10.08) * mm, v(-54.7, 8.73) * mm]});
            skFitSpline(sketch, "E941", {"points": [v(-54.7, 8.73) * mm, v(-54.95, 7.4) * mm, v(-55.2, 6.06) * mm, v(-55.44, 4.72) * mm]});
            skLineSegment(sketch, "E942", {"start": v(-49.37, 24.58) * mm, "end": v(-49.24, 24.66) * mm});
            skLineSegment(sketch, "E943", {"start": v(-49.24, 24.66) * mm, "end": v(-51.15, 20.78) * mm});
            skLineSegment(sketch, "E944", {"start": v(-51.15, 20.78) * mm, "end": v(-52.95, 16.1) * mm});
            skLineSegment(sketch, "E945", {"start": v(-52.95, 16.1) * mm, "end": v(-53.94, 12.78) * mm});
            skFitSpline(sketch, "E946", {"points": [v(-48.25, 1.98) * mm, v(-47.34, 2.4) * mm, v(-46.42, 2.82) * mm, v(-45.5, 3.24) * mm]});
            skFitSpline(sketch, "E947", {"points": [v(-45.5, 3.24) * mm, v(-44.1, 3.87) * mm, v(-42.71, 4.5) * mm, v(-41.32, 5.13) * mm]});
            skLineSegment(sketch, "E948", {"start": v(-55.44, 4.72) * mm, "end": v(-55.5, 2.91) * mm});
            skLineSegment(sketch, "E949", {"start": v(-55.5, 2.91) * mm, "end": v(-54.84, 2.07) * mm});
            skLineSegment(sketch, "E950", {"start": v(-54.84, 2.07) * mm, "end": v(-53.3, 1.5) * mm});
            skLineSegment(sketch, "E951", {"start": v(-53.3, 1.5) * mm, "end": v(-50.36, 1.38) * mm});
            skLineSegment(sketch, "E952", {"start": v(-50.36, 1.38) * mm, "end": v(-48.25, 1.98) * mm});
            skFitSpline(sketch, "E953", {"points": [v(-38.42, 1.93) * mm, v(-38.72, 1.93) * mm, v(-39.02, 1.93) * mm, v(-39.32, 1.93) * mm]});
            skFitSpline(sketch, "E954", {"points": [v(-39.32, 1.93) * mm, v(-39.75, 1.93) * mm, v(-40.18, 1.92) * mm, v(-40.6, 1.9) * mm]});
            skLineSegment(sketch, "E955", {"start": v(-41.32, 5.13) * mm, "end": v(-39.49, 5.45) * mm});
            skLineSegment(sketch, "E956", {"start": v(-39.49, 5.45) * mm, "end": v(-37.4, 5.43) * mm});
            skLineSegment(sketch, "E957", {"start": v(-37.4, 5.43) * mm, "end": v(-36.86, 4.96) * mm});
            skLineSegment(sketch, "E958", {"start": v(-36.86, 4.96) * mm, "end": v(-37, 4.39) * mm});
            skLineSegment(sketch, "E959", {"start": v(-37, 4.39) * mm, "end": v(-37.6, 3.35) * mm});
            skLineSegment(sketch, "E960", {"start": v(-37.6, 3.35) * mm, "end": v(-37.76, 2.75) * mm});
            skLineSegment(sketch, "E961", {"start": v(-37.76, 2.75) * mm, "end": v(-38.42, 1.93) * mm});
            skFitSpline(sketch, "E962", {"points": [v(-41.4, -13.91) * mm, v(-41.72, -14.04) * mm, v(-42.05, -14.15) * mm, v(-42.38, -14.27) * mm]});
            skFitSpline(sketch, "E963", {"points": [v(-42.38, -14.27) * mm, v(-43.11, -14.52) * mm, v(-43.85, -14.76) * mm, v(-44.6, -14.98) * mm]});
            skLineSegment(sketch, "E964", {"start": v(-40.6, 1.9) * mm, "end": v(-41.59, 1.66) * mm});
            skLineSegment(sketch, "E965", {"start": v(-41.59, 1.66) * mm, "end": v(-44.73, 0) * mm});
            skLineSegment(sketch, "E966", {"start": v(-44.73, 0) * mm, "end": v(-48.12, -1.54) * mm});
            skLineSegment(sketch, "E967", {"start": v(-48.12, -1.54) * mm, "end": v(-50.96, -2.17) * mm});
            skLineSegment(sketch, "E968", {"start": v(-50.96, -2.17) * mm, "end": v(-53.72, -2.2) * mm});
            skLineSegment(sketch, "E969", {"start": v(-53.72, -2.2) * mm, "end": v(-55.36, -1.65) * mm});
            skLineSegment(sketch, "E970", {"start": v(-55.36, -1.65) * mm, "end": v(-55.06, -6.57) * mm});
            skLineSegment(sketch, "E971", {"start": v(-55.06, -6.57) * mm, "end": v(-53.5, -6.84) * mm});
            skLineSegment(sketch, "E972", {"start": v(-53.5, -6.84) * mm, "end": v(-51.72, -6.81) * mm});
            skLineSegment(sketch, "E973", {"start": v(-51.72, -6.81) * mm, "end": v(-49.37, -6.16) * mm});
            skLineSegment(sketch, "E974", {"start": v(-49.37, -6.16) * mm, "end": v(-46.72, -4.9) * mm});
            skLineSegment(sketch, "E975", {"start": v(-46.72, -4.9) * mm, "end": v(-43.8, -3.5) * mm});
            skLineSegment(sketch, "E976", {"start": v(-43.8, -3.5) * mm, "end": v(-41.86, -3.15) * mm});
            skLineSegment(sketch, "E977", {"start": v(-41.86, -3.15) * mm, "end": v(-39.9, -3.18) * mm});
            skLineSegment(sketch, "E978", {"start": v(-39.9, -3.18) * mm, "end": v(-40.28, -5.12) * mm});
            skLineSegment(sketch, "E979", {"start": v(-40.28, -5.12) * mm, "end": v(-40.74, -6.46) * mm});
            skLineSegment(sketch, "E980", {"start": v(-40.74, -6.46) * mm, "end": v(-42.52, -6.6) * mm});
            skLineSegment(sketch, "E981", {"start": v(-42.52, -6.6) * mm, "end": v(-44.07, -7.14) * mm});
            skLineSegment(sketch, "E982", {"start": v(-44.07, -7.14) * mm, "end": v(-46.5, -8.37) * mm});
            skLineSegment(sketch, "E983", {"start": v(-46.5, -8.37) * mm, "end": v(-49.05, -9.73) * mm});
            skLineSegment(sketch, "E984", {"start": v(-49.05, -9.73) * mm, "end": v(-51.78, -10.72) * mm});
            skLineSegment(sketch, "E985", {"start": v(-51.78, -10.72) * mm, "end": v(-54.2, -10.85) * mm});
            skLineSegment(sketch, "E986", {"start": v(-54.2, -10.85) * mm, "end": v(-53.14, -14.62) * mm});
            skLineSegment(sketch, "E987", {"start": v(-53.14, -14.62) * mm, "end": v(-51.23, -14.7) * mm});
            skLineSegment(sketch, "E988", {"start": v(-51.23, -14.7) * mm, "end": v(-48.3, -13.45) * mm});
            skLineSegment(sketch, "E989", {"start": v(-48.3, -13.45) * mm, "end": v(-44.1, -11.32) * mm});
            skLineSegment(sketch, "E990", {"start": v(-44.1, -11.32) * mm, "end": v(-41.15, -11.02) * mm});
            skLineSegment(sketch, "E991", {"start": v(-41.15, -11.02) * mm, "end": v(-41.4, -13.91) * mm});
            skFitSpline(sketch, "E992", {"points": [v(-44.38, -22.68) * mm, v(-45.2, -23.12) * mm, v(-46, -23.58) * mm, v(-46.8, -24.05) * mm]});
            skFitSpline(sketch, "E993", {"points": [v(-46.8, -24.05) * mm, v(-47.43, -24.41) * mm, v(-48.05, -24.79) * mm, v(-48.66, -25.17) * mm]});
            skLineSegment(sketch, "E994", {"start": v(-44.6, -14.98) * mm, "end": v(-47.7, -16.84) * mm});
            skLineSegment(sketch, "E995", {"start": v(-47.7, -16.84) * mm, "end": v(-50.55, -18.01) * mm});
            skLineSegment(sketch, "E996", {"start": v(-50.55, -18.01) * mm, "end": v(-52, -18.07) * mm});
            skLineSegment(sketch, "E997", {"start": v(-52, -18.07) * mm, "end": v(-51.83, -19.76) * mm});
            skLineSegment(sketch, "E998", {"start": v(-51.83, -19.76) * mm, "end": v(-51.01, -21.48) * mm});
            skLineSegment(sketch, "E999", {"start": v(-51.01, -21.48) * mm, "end": v(-49.7, -21.95) * mm});
            skLineSegment(sketch, "E1000", {"start": v(-49.7, -21.95) * mm, "end": v(-47.3, -20.85) * mm});
            skLineSegment(sketch, "E1001", {"start": v(-47.3, -20.85) * mm, "end": v(-44.73, -19.38) * mm});
            skLineSegment(sketch, "E1002", {"start": v(-44.73, -19.38) * mm, "end": v(-42.9, -18.56) * mm});
            skLineSegment(sketch, "E1003", {"start": v(-42.9, -18.56) * mm, "end": v(-41.01, -18.59) * mm});
            skLineSegment(sketch, "E1004", {"start": v(-41.01, -18.59) * mm, "end": v(-40.41, -21.5) * mm});
            skLineSegment(sketch, "E1005", {"start": v(-40.41, -21.5) * mm, "end": v(-42.19, -21.7) * mm});
            skLineSegment(sketch, "E1006", {"start": v(-42.19, -21.7) * mm, "end": v(-44.38, -22.68) * mm});
            skFitSpline(sketch, "E1007", {"points": [v(-46.64, -28.26) * mm, v(-45.6, -27.78) * mm, v(-44.57, -27.3) * mm, v(-43.53, -26.8) * mm]});
            skFitSpline(sketch, "E1008", {"points": [v(-43.53, -26.8) * mm, v(-42.64, -26.4) * mm, v(-41.74, -25.97) * mm, v(-40.85, -25.55) * mm]});
            skLineSegment(sketch, "E1009", {"start": v(-48.66, -25.17) * mm, "end": v(-48.83, -25.25) * mm});
            skLineSegment(sketch, "E1010", {"start": v(-48.83, -25.25) * mm, "end": v(-46.64, -28.26) * mm});
            skFitSpline(sketch, "E1011", {"points": [v(-29.51, -12.99) * mm, v(-28.84, -11.76) * mm, v(-28.15, -10.55) * mm, v(-27.44, -9.35) * mm]});
            skFitSpline(sketch, "E1012", {"points": [v(-27.44, -9.35) * mm, v(-26.59, -7.92) * mm, v(-25.71, -6.5) * mm, v(-24.82, -5.1) * mm]});
            skLineSegment(sketch, "E1013", {"start": v(-40.85, -25.55) * mm, "end": v(-39.21, -25.47) * mm});
            skLineSegment(sketch, "E1014", {"start": v(-39.21, -25.47) * mm, "end": v(-39.84, -22) * mm});
            skLineSegment(sketch, "E1015", {"start": v(-39.84, -22) * mm, "end": v(-37.46, -22.16) * mm});
            skLineSegment(sketch, "E1016", {"start": v(-37.46, -22.16) * mm, "end": v(-34.57, -20.88) * mm});
            skLineSegment(sketch, "E1017", {"start": v(-34.57, -20.88) * mm, "end": v(-31.4, -18.5) * mm});
            skLineSegment(sketch, "E1018", {"start": v(-31.4, -18.5) * mm, "end": v(-30.83, -16) * mm});
            skLineSegment(sketch, "E1019", {"start": v(-30.83, -16) * mm, "end": v(-29.51, -12.99) * mm});
            skFitSpline(sketch, "E1020", {"points": [v(-21.07, 18.73) * mm, v(-21.47, 18) * mm, v(-21.87, 17.27) * mm, v(-22.27, 16.54) * mm]});
            skFitSpline(sketch, "E1021", {"points": [v(-22.27, 16.54) * mm, v(-22.6, 15.94) * mm, v(-22.95, 15.34) * mm, v(-23.29, 14.74) * mm]});
            skLineSegment(sketch, "E1022", {"start": v(-24.82, -5.1) * mm, "end": v(-24.7, -0.47) * mm});
            skLineSegment(sketch, "E1023", {"start": v(-24.7, -0.47) * mm, "end": v(-25.55, 2.61) * mm});
            skLineSegment(sketch, "E1024", {"start": v(-25.55, 2.61) * mm, "end": v(-26.37, 7.42) * mm});
            skLineSegment(sketch, "E1025", {"start": v(-26.37, 7.42) * mm, "end": v(-26.43, 10.23) * mm});
            skLineSegment(sketch, "E1026", {"start": v(-26.43, 10.23) * mm, "end": v(-25.03, 14.55) * mm});
            skLineSegment(sketch, "E1027", {"start": v(-25.03, 14.55) * mm, "end": v(-23.72, 16.6) * mm});
            skLineSegment(sketch, "E1028", {"start": v(-23.72, 16.6) * mm, "end": v(-22.22, 18.13) * mm});
            skLineSegment(sketch, "E1029", {"start": v(-22.22, 18.13) * mm, "end": v(-21.07, 18.73) * mm});
            skFitSpline(sketch, "E1030", {"points": [v(-22.52, -6.27) * mm, v(-23.24, -7.21) * mm, v(-23.95, -8.18) * mm, v(-24.62, -9.16) * mm]});
            skFitSpline(sketch, "E1031", {"points": [v(-24.62, -9.16) * mm, v(-25.5, -10.43) * mm, v(-26.34, -11.72) * mm, v(-27.14, -13.04) * mm]});
            skLineSegment(sketch, "E1032", {"start": v(-23.29, 14.74) * mm, "end": v(-23.83, 11.96) * mm});
            skLineSegment(sketch, "E1033", {"start": v(-23.83, 11.96) * mm, "end": v(-23.97, 7.89) * mm});
            skLineSegment(sketch, "E1034", {"start": v(-23.97, 7.89) * mm, "end": v(-23.72, 5.62) * mm});
            skLineSegment(sketch, "E1035", {"start": v(-23.72, 5.62) * mm, "end": v(-23.15, 3.16) * mm});
            skLineSegment(sketch, "E1036", {"start": v(-23.15, 3.16) * mm, "end": v(-22.2, 0.3) * mm});
            skLineSegment(sketch, "E1037", {"start": v(-22.2, 0.3) * mm, "end": v(-21.65, -1.62) * mm});
            skLineSegment(sketch, "E1038", {"start": v(-21.65, -1.62) * mm, "end": v(-21.73, -3.86) * mm});
            skLineSegment(sketch, "E1039", {"start": v(-21.73, -3.86) * mm, "end": v(-22.52, -6.27) * mm});
            skFitSpline(sketch, "E1040", {"points": [v(-27.93, -43.23) * mm, v(-27.34, -42.29) * mm, v(-26.75, -41.35) * mm, v(-26.15, -40.41) * mm]});
            skFitSpline(sketch, "E1041", {"points": [v(-26.15, -40.41) * mm, v(-25.52, -39.42) * mm, v(-24.9, -38.43) * mm, v(-24.27, -37.44) * mm]});
            skFitSpline(sketch, "E1042", {"points": [v(-24.27, -37.44) * mm, v(-23.86, -36.77) * mm, v(-23.45, -36.1) * mm, v(-23.04, -35.44) * mm]});
            skFitSpline(sketch, "E1043", {"points": [v(-23.04, -35.44) * mm, v(-22.8, -34.24) * mm, v(-22.59, -33.02) * mm, v(-22.41, -31.8) * mm]});
            skFitSpline(sketch, "E1044", {"points": [v(-22.41, -31.8) * mm, v(-22.37, -31.54) * mm, v(-22.34, -31.28) * mm, v(-22.3, -31.02) * mm]});
            skLineSegment(sketch, "E1045", {"start": v(-27.14, -13.04) * mm, "end": v(-28.37, -16) * mm});
            skLineSegment(sketch, "E1046", {"start": v(-28.37, -16) * mm, "end": v(-28.48, -19.13) * mm});
            skLineSegment(sketch, "E1047", {"start": v(-28.48, -19.13) * mm, "end": v(-27.71, -22.52) * mm});
            skLineSegment(sketch, "E1048", {"start": v(-27.71, -22.52) * mm, "end": v(-25.69, -26.1) * mm});
            skLineSegment(sketch, "E1049", {"start": v(-25.69, -26.1) * mm, "end": v(-26.15, -26.7) * mm});
            skLineSegment(sketch, "E1050", {"start": v(-26.15, -26.7) * mm, "end": v(-30.66, -30.03) * mm});
            skLineSegment(sketch, "E1051", {"start": v(-30.66, -30.03) * mm, "end": v(-34.46, -31.86) * mm});
            skLineSegment(sketch, "E1052", {"start": v(-34.46, -31.86) * mm, "end": v(-36.59, -32.08) * mm});
            skLineSegment(sketch, "E1053", {"start": v(-36.59, -32.08) * mm, "end": v(-38.2, -28.88) * mm});
            skLineSegment(sketch, "E1054", {"start": v(-38.2, -28.88) * mm, "end": v(-40.2, -28.7) * mm});
            skLineSegment(sketch, "E1055", {"start": v(-40.2, -28.7) * mm, "end": v(-43.28, -30.03) * mm});
            skLineSegment(sketch, "E1056", {"start": v(-43.28, -30.03) * mm, "end": v(-44.87, -31.23) * mm});
            skLineSegment(sketch, "E1057", {"start": v(-44.87, -31.23) * mm, "end": v(-42.44, -34.16) * mm});
            skLineSegment(sketch, "E1058", {"start": v(-42.44, -34.16) * mm, "end": v(-39.73, -32.52) * mm});
            skLineSegment(sketch, "E1059", {"start": v(-39.73, -32.52) * mm, "end": v(-37.85, -32.4) * mm});
            skLineSegment(sketch, "E1060", {"start": v(-37.85, -32.4) * mm, "end": v(-36.8, -32.76) * mm});
            skLineSegment(sketch, "E1061", {"start": v(-36.8, -32.76) * mm, "end": v(-36.13, -33.88) * mm});
            skLineSegment(sketch, "E1062", {"start": v(-36.13, -33.88) * mm, "end": v(-36.32, -34.76) * mm});
            skLineSegment(sketch, "E1063", {"start": v(-36.32, -34.76) * mm, "end": v(-38.04, -35.25) * mm});
            skLineSegment(sketch, "E1064", {"start": v(-38.04, -35.25) * mm, "end": v(-39.84, -35.93) * mm});
            skLineSegment(sketch, "E1065", {"start": v(-39.84, -35.93) * mm, "end": v(-40.33, -36.64) * mm});
            skLineSegment(sketch, "E1066", {"start": v(-40.33, -36.64) * mm, "end": v(-37.63, -39.35) * mm});
            skLineSegment(sketch, "E1067", {"start": v(-37.63, -39.35) * mm, "end": v(-35.22, -38.36) * mm});
            skLineSegment(sketch, "E1068", {"start": v(-35.22, -38.36) * mm, "end": v(-33.78, -38.3) * mm});
            skLineSegment(sketch, "E1069", {"start": v(-33.78, -38.3) * mm, "end": v(-32.4, -40.11) * mm});
            skLineSegment(sketch, "E1070", {"start": v(-32.4, -40.11) * mm, "end": v(-34.46, -41.67) * mm});
            skLineSegment(sketch, "E1071", {"start": v(-34.46, -41.67) * mm, "end": v(-32.74, -43.45) * mm});
            skLineSegment(sketch, "E1072", {"start": v(-32.74, -43.45) * mm, "end": v(-29.43, -45.52) * mm});
            skLineSegment(sketch, "E1073", {"start": v(-29.43, -45.52) * mm, "end": v(-28.89, -45.58) * mm});
            skLineSegment(sketch, "E1074", {"start": v(-28.89, -45.58) * mm, "end": v(-27.93, -43.23) * mm});
            skFitSpline(sketch, "E1075", {"points": [v(-18.5, -19.08) * mm, v(-18.52, -19.02) * mm, v(-18.54, -18.97) * mm, v(-18.56, -18.91) * mm]});
            skLineSegment(sketch, "E1076", {"start": v(-22.3, -31.02) * mm, "end": v(-21.1, -33.88) * mm});
            skLineSegment(sketch, "E1077", {"start": v(-21.1, -33.88) * mm, "end": v(-21.9, -37.08) * mm});
            skLineSegment(sketch, "E1078", {"start": v(-21.9, -37.08) * mm, "end": v(-24.19, -40.5) * mm});
            skLineSegment(sketch, "E1079", {"start": v(-24.19, -40.5) * mm, "end": v(-26, -43.36) * mm});
            skLineSegment(sketch, "E1080", {"start": v(-26, -43.36) * mm, "end": v(-26.95, -45.5) * mm});
            skLineSegment(sketch, "E1081", {"start": v(-26.95, -45.5) * mm, "end": v(-26.8, -47.08) * mm});
            skLineSegment(sketch, "E1082", {"start": v(-26.8, -47.08) * mm, "end": v(-23.75, -48.72) * mm});
            skLineSegment(sketch, "E1083", {"start": v(-23.75, -48.72) * mm, "end": v(-23.67, -46.64) * mm});
            skLineSegment(sketch, "E1084", {"start": v(-23.67, -46.64) * mm, "end": v(-22.58, -44.02) * mm});
            skLineSegment(sketch, "E1085", {"start": v(-22.58, -44.02) * mm, "end": v(-19.73, -39.57) * mm});
            skLineSegment(sketch, "E1086", {"start": v(-19.73, -39.57) * mm, "end": v(-17.93, -36.18) * mm});
            skLineSegment(sketch, "E1087", {"start": v(-17.93, -36.18) * mm, "end": v(-17.36, -33.4) * mm});
            skLineSegment(sketch, "E1088", {"start": v(-17.36, -33.4) * mm, "end": v(-18.23, -30.72) * mm});
            skLineSegment(sketch, "E1089", {"start": v(-18.23, -30.72) * mm, "end": v(-19.76, -28.37) * mm});
            skLineSegment(sketch, "E1090", {"start": v(-19.76, -28.37) * mm, "end": v(-22.68, -24.81) * mm});
            skLineSegment(sketch, "E1091", {"start": v(-22.68, -24.81) * mm, "end": v(-24.65, -21.8) * mm});
            skLineSegment(sketch, "E1092", {"start": v(-24.65, -21.8) * mm, "end": v(-25.33, -19.46) * mm});
            skLineSegment(sketch, "E1093", {"start": v(-25.33, -19.46) * mm, "end": v(-25.23, -16.76) * mm});
            skLineSegment(sketch, "E1094", {"start": v(-25.23, -16.76) * mm, "end": v(-24.05, -13.4) * mm});
            skLineSegment(sketch, "E1095", {"start": v(-24.05, -13.4) * mm, "end": v(-21.5, -10.17) * mm});
            skLineSegment(sketch, "E1096", {"start": v(-21.5, -10.17) * mm, "end": v(-19.32, -7.58) * mm});
            skLineSegment(sketch, "E1097", {"start": v(-19.32, -7.58) * mm, "end": v(-18.34, -5.4) * mm});
            skLineSegment(sketch, "E1098", {"start": v(-18.34, -5.4) * mm, "end": v(-18.23, -3.4) * mm});
            skLineSegment(sketch, "E1099", {"start": v(-18.23, -3.4) * mm, "end": v(-18.37, -1.38) * mm});
            skLineSegment(sketch, "E1100", {"start": v(-18.37, -1.38) * mm, "end": v(-19.22, 1.38) * mm});
            skLineSegment(sketch, "E1101", {"start": v(-19.22, 1.38) * mm, "end": v(-20.3, 4.28) * mm});
            skLineSegment(sketch, "E1102", {"start": v(-20.3, 4.28) * mm, "end": v(-21.13, 7.26) * mm});
            skLineSegment(sketch, "E1103", {"start": v(-21.13, 7.26) * mm, "end": v(-21.48, 10.1) * mm});
            skLineSegment(sketch, "E1104", {"start": v(-21.48, 10.1) * mm, "end": v(-20.94, 13.13) * mm});
            skLineSegment(sketch, "E1105", {"start": v(-20.94, 13.13) * mm, "end": v(-19.32, 16.95) * mm});
            skLineSegment(sketch, "E1106", {"start": v(-19.32, 16.95) * mm, "end": v(-17.69, 19.5) * mm});
            skLineSegment(sketch, "E1107", {"start": v(-17.69, 19.5) * mm, "end": v(-15.25, 21.33) * mm});
            skLineSegment(sketch, "E1108", {"start": v(-15.25, 21.33) * mm, "end": v(-16.1, 19.93) * mm});
            skLineSegment(sketch, "E1109", {"start": v(-16.1, 19.93) * mm, "end": v(-17.93, 16.6) * mm});
            skLineSegment(sketch, "E1110", {"start": v(-17.93, 16.6) * mm, "end": v(-18.91, 13.02) * mm});
            skLineSegment(sketch, "E1111", {"start": v(-18.91, 13.02) * mm, "end": v(-19.16, 9.33) * mm});
            skLineSegment(sketch, "E1112", {"start": v(-19.16, 9.33) * mm, "end": v(-18.45, 5.67) * mm});
            skLineSegment(sketch, "E1113", {"start": v(-18.45, 5.67) * mm, "end": v(-16.81, 2.53) * mm});
            skLineSegment(sketch, "E1114", {"start": v(-16.81, 2.53) * mm, "end": v(-15.17, -1.35) * mm});
            skLineSegment(sketch, "E1115", {"start": v(-15.17, -1.35) * mm, "end": v(-15.25, -4.63) * mm});
            skLineSegment(sketch, "E1116", {"start": v(-15.25, -4.63) * mm, "end": v(-16.87, -8.04) * mm});
            skLineSegment(sketch, "E1117", {"start": v(-16.87, -8.04) * mm, "end": v(-19.46, -11.26) * mm});
            skLineSegment(sketch, "E1118", {"start": v(-19.46, -11.26) * mm, "end": v(-21.46, -14.19) * mm});
            skLineSegment(sketch, "E1119", {"start": v(-21.46, -14.19) * mm, "end": v(-22.36, -16.65) * mm});
            skLineSegment(sketch, "E1120", {"start": v(-22.36, -16.65) * mm, "end": v(-22.41, -20.25) * mm});
            skLineSegment(sketch, "E1121", {"start": v(-22.41, -20.25) * mm, "end": v(-20.88, -23.26) * mm});
            skLineSegment(sketch, "E1122", {"start": v(-20.88, -23.26) * mm, "end": v(-18.15, -26.34) * mm});
            skLineSegment(sketch, "E1123", {"start": v(-18.15, -26.34) * mm, "end": v(-15.58, -29.9) * mm});
            skLineSegment(sketch, "E1124", {"start": v(-15.58, -29.9) * mm, "end": v(-14.74, -33.45) * mm});
            skLineSegment(sketch, "E1125", {"start": v(-14.74, -33.45) * mm, "end": v(-15.3, -37.22) * mm});
            skLineSegment(sketch, "E1126", {"start": v(-15.3, -37.22) * mm, "end": v(-17.71, -41.48) * mm});
            skLineSegment(sketch, "E1127", {"start": v(-17.71, -41.48) * mm, "end": v(-19.7, -44.57) * mm});
            skLineSegment(sketch, "E1128", {"start": v(-19.7, -44.57) * mm, "end": v(-20.47, -46.59) * mm});
            skLineSegment(sketch, "E1129", {"start": v(-20.47, -46.59) * mm, "end": v(-20.58, -49.95) * mm});
            skLineSegment(sketch, "E1130", {"start": v(-20.58, -49.95) * mm, "end": v(-16.67, -51.31) * mm});
            skLineSegment(sketch, "E1131", {"start": v(-16.67, -51.31) * mm, "end": v(-16.84, -47.57) * mm});
            skLineSegment(sketch, "E1132", {"start": v(-16.84, -47.57) * mm, "end": v(-15.86, -44.35) * mm});
            skLineSegment(sketch, "E1133", {"start": v(-15.86, -44.35) * mm, "end": v(-13.72, -40.39) * mm});
            skLineSegment(sketch, "E1134", {"start": v(-13.72, -40.39) * mm, "end": v(-11.57, -36.75) * mm});
            skLineSegment(sketch, "E1135", {"start": v(-11.57, -36.75) * mm, "end": v(-10.97, -34.95) * mm});
            skLineSegment(sketch, "E1136", {"start": v(-10.97, -34.95) * mm, "end": v(-11.05, -31.5) * mm});
            skLineSegment(sketch, "E1137", {"start": v(-11.05, -31.5) * mm, "end": v(-12.41, -28.26) * mm});
            skLineSegment(sketch, "E1138", {"start": v(-12.41, -28.26) * mm, "end": v(-15.53, -24.84) * mm});
            skLineSegment(sketch, "E1139", {"start": v(-15.53, -24.84) * mm, "end": v(-17.71, -21.84) * mm});
            skLineSegment(sketch, "E1140", {"start": v(-17.71, -21.84) * mm, "end": v(-18.5, -19.08) * mm});
            skFitSpline(sketch, "E1141", {"points": [v(15.34, 5.8) * mm, v(14.93, 4.88) * mm, v(14.54, 3.94) * mm, v(14.17, 3) * mm]});
            skFitSpline(sketch, "E1142", {"points": [v(14.17, 3) * mm, v(13.8, 2.03) * mm, v(13.44, 1.05) * mm, v(13.1, 0.07) * mm]});
            skFitSpline(sketch, "E1143", {"points": [v(13.1, 0.07) * mm, v(12.85, -0.65) * mm, v(12.62, -1.38) * mm, v(12.4, -2.11) * mm]});
            skLineSegment(sketch, "E1144", {"start": v(-18.56, -18.91) * mm, "end": v(-18.48, -16.37) * mm});
            skLineSegment(sketch, "E1145", {"start": v(-18.48, -16.37) * mm, "end": v(-17.47, -13.8) * mm});
            skLineSegment(sketch, "E1146", {"start": v(-17.47, -13.8) * mm, "end": v(-14.87, -10.14) * mm});
            skLineSegment(sketch, "E1147", {"start": v(-14.87, -10.14) * mm, "end": v(-12.96, -7.28) * mm});
            skLineSegment(sketch, "E1148", {"start": v(-12.96, -7.28) * mm, "end": v(-11.98, -4.87) * mm});
            skLineSegment(sketch, "E1149", {"start": v(-11.98, -4.87) * mm, "end": v(-12.11, -1.98) * mm});
            skLineSegment(sketch, "E1150", {"start": v(-12.11, -1.98) * mm, "end": v(-12.71, 0.35) * mm});
            skLineSegment(sketch, "E1151", {"start": v(-12.71, 0.35) * mm, "end": v(-14.16, 3.54) * mm});
            skLineSegment(sketch, "E1152", {"start": v(-14.16, 3.54) * mm, "end": v(-15.47, 6.66) * mm});
            skLineSegment(sketch, "E1153", {"start": v(-15.47, 6.66) * mm, "end": v(-16.18, 9.39) * mm});
            skLineSegment(sketch, "E1154", {"start": v(-16.18, 9.39) * mm, "end": v(-16.16, 13.7) * mm});
            skLineSegment(sketch, "E1155", {"start": v(-16.16, 13.7) * mm, "end": v(-15.14, 17.36) * mm});
            skLineSegment(sketch, "E1156", {"start": v(-15.14, 17.36) * mm, "end": v(-13.42, 19.88) * mm});
            skLineSegment(sketch, "E1157", {"start": v(-13.42, 19.88) * mm, "end": v(-11.35, 21.7) * mm});
            skLineSegment(sketch, "E1158", {"start": v(-11.35, 21.7) * mm, "end": v(-10.2, 22.47) * mm});
            skLineSegment(sketch, "E1159", {"start": v(-10.2, 22.47) * mm, "end": v(-11.65, 20.53) * mm});
            skLineSegment(sketch, "E1160", {"start": v(-11.65, 20.53) * mm, "end": v(-13.04, 17.97) * mm});
            skLineSegment(sketch, "E1161", {"start": v(-13.04, 17.97) * mm, "end": v(-14.19, 14.96) * mm});
            skLineSegment(sketch, "E1162", {"start": v(-14.19, 14.96) * mm, "end": v(-14.22, 11.08) * mm});
            skLineSegment(sketch, "E1163", {"start": v(-14.22, 11.08) * mm, "end": v(-13.2, 7.04) * mm});
            skLineSegment(sketch, "E1164", {"start": v(-13.2, 7.04) * mm, "end": v(-11.48, 3.02) * mm});
            skLineSegment(sketch, "E1165", {"start": v(-11.48, 3.02) * mm, "end": v(-9.52, -1.48) * mm});
            skLineSegment(sketch, "E1166", {"start": v(-9.52, -1.48) * mm, "end": v(-9.46, -5.66) * mm});
            skLineSegment(sketch, "E1167", {"start": v(-9.46, -5.66) * mm, "end": v(-11.35, -9.7) * mm});
            skLineSegment(sketch, "E1168", {"start": v(-11.35, -9.7) * mm, "end": v(-14.16, -12.96) * mm});
            skLineSegment(sketch, "E1169", {"start": v(-14.16, -12.96) * mm, "end": v(-15.55, -16.7) * mm});
            skLineSegment(sketch, "E1170", {"start": v(-15.55, -16.7) * mm, "end": v(-15.55, -19.46) * mm});
            skLineSegment(sketch, "E1171", {"start": v(-15.55, -19.46) * mm, "end": v(-13.97, -22.47) * mm});
            skLineSegment(sketch, "E1172", {"start": v(-13.97, -22.47) * mm, "end": v(-11.32, -25.83) * mm});
            skLineSegment(sketch, "E1173", {"start": v(-11.32, -25.83) * mm, "end": v(-9.35, -28.23) * mm});
            skLineSegment(sketch, "E1174", {"start": v(-9.35, -28.23) * mm, "end": v(-8.2, -31.64) * mm});
            skLineSegment(sketch, "E1175", {"start": v(-8.2, -31.64) * mm, "end": v(-8.1, -35.03) * mm});
            skLineSegment(sketch, "E1176", {"start": v(-8.1, -35.03) * mm, "end": v(-10.42, -39.92) * mm});
            skLineSegment(sketch, "E1177", {"start": v(-10.42, -39.92) * mm, "end": v(-12.6, -43.9) * mm});
            skLineSegment(sketch, "E1178", {"start": v(-12.6, -43.9) * mm, "end": v(-13.59, -47.02) * mm});
            skLineSegment(sketch, "E1179", {"start": v(-13.59, -47.02) * mm, "end": v(-13.56, -50.9) * mm});
            skLineSegment(sketch, "E1180", {"start": v(-13.56, -50.9) * mm, "end": v(-13.12, -52.1) * mm});
            skLineSegment(sketch, "E1181", {"start": v(-13.12, -52.1) * mm, "end": v(-11.18, -52.84) * mm});
            skLineSegment(sketch, "E1182", {"start": v(-11.18, -52.84) * mm, "end": v(-8.97, -52.87) * mm});
            skLineSegment(sketch, "E1183", {"start": v(-8.97, -52.87) * mm, "end": v(-9.68, -51.07) * mm});
            skLineSegment(sketch, "E1184", {"start": v(-9.68, -51.07) * mm, "end": v(-9.98, -47.1) * mm});
            skLineSegment(sketch, "E1185", {"start": v(-9.98, -47.1) * mm, "end": v(-9.05, -43.85) * mm});
            skLineSegment(sketch, "E1186", {"start": v(-9.05, -43.85) * mm, "end": v(-6.81, -39.54) * mm});
            skLineSegment(sketch, "E1187", {"start": v(-6.81, -39.54) * mm, "end": v(-4.52, -34.18) * mm});
            skLineSegment(sketch, "E1188", {"start": v(-4.52, -34.18) * mm, "end": v(-4.46, -30.66) * mm});
            skLineSegment(sketch, "E1189", {"start": v(-4.46, -30.66) * mm, "end": v(-6.57, -26.67) * mm});
            skLineSegment(sketch, "E1190", {"start": v(-6.57, -26.67) * mm, "end": v(-10.58, -21.86) * mm});
            skLineSegment(sketch, "E1191", {"start": v(-10.58, -21.86) * mm, "end": v(-11.98, -18.86) * mm});
            skLineSegment(sketch, "E1192", {"start": v(-11.98, -18.86) * mm, "end": v(-11.9, -16.24) * mm});
            skLineSegment(sketch, "E1193", {"start": v(-11.9, -16.24) * mm, "end": v(-9.8, -12.44) * mm});
            skLineSegment(sketch, "E1194", {"start": v(-9.8, -12.44) * mm, "end": v(-7.11, -8.42) * mm});
            skLineSegment(sketch, "E1195", {"start": v(-7.11, -8.42) * mm, "end": v(-6.43, -6.51) * mm});
            skLineSegment(sketch, "E1196", {"start": v(-6.43, -6.51) * mm, "end": v(-5.37, -5.58) * mm});
            skLineSegment(sketch, "E1197", {"start": v(-5.37, -5.58) * mm, "end": v(-4.35, -5.64) * mm});
            skLineSegment(sketch, "E1198", {"start": v(-4.35, -5.64) * mm, "end": v(-3.02, -6) * mm});
            skLineSegment(sketch, "E1199", {"start": v(-3.02, -6) * mm, "end": v(-1.54, -6.4) * mm});
            skLineSegment(sketch, "E1200", {"start": v(-1.54, -6.4) * mm, "end": v(0.95, -6.48) * mm});
            skLineSegment(sketch, "E1201", {"start": v(0.95, -6.48) * mm, "end": v(3.87, -5.58) * mm});
            skLineSegment(sketch, "E1202", {"start": v(3.87, -5.58) * mm, "end": v(5.84, -5.91) * mm});
            skLineSegment(sketch, "E1203", {"start": v(5.84, -5.91) * mm, "end": v(6.82, -7.55) * mm});
            skLineSegment(sketch, "E1204", {"start": v(6.82, -7.55) * mm, "end": v(9.2, -11.13) * mm});
            skLineSegment(sketch, "E1205", {"start": v(9.2, -11.13) * mm, "end": v(11.93, -15.03) * mm});
            skLineSegment(sketch, "E1206", {"start": v(11.93, -15.03) * mm, "end": v(12.1, -16.84) * mm});
            skLineSegment(sketch, "E1207", {"start": v(12.1, -16.84) * mm, "end": v(12.15, -19.08) * mm});
            skLineSegment(sketch, "E1208", {"start": v(12.15, -19.08) * mm, "end": v(11.3, -20.88) * mm});
            skLineSegment(sketch, "E1209", {"start": v(11.3, -20.88) * mm, "end": v(10.4, -22.47) * mm});
            skLineSegment(sketch, "E1210", {"start": v(10.4, -22.47) * mm, "end": v(9.11, -24.1) * mm});
            skLineSegment(sketch, "E1211", {"start": v(9.11, -24.1) * mm, "end": v(8.9, -24.27) * mm});
            skLineSegment(sketch, "E1212", {"start": v(8.9, -24.27) * mm, "end": v(6.82, -26.45) * mm});
            skLineSegment(sketch, "E1213", {"start": v(6.82, -26.45) * mm, "end": v(5.07, -29.13) * mm});
            skLineSegment(sketch, "E1214", {"start": v(5.07, -29.13) * mm, "end": v(4.3, -31.48) * mm});
            skLineSegment(sketch, "E1215", {"start": v(4.3, -31.48) * mm, "end": v(4.39, -34) * mm});
            skLineSegment(sketch, "E1216", {"start": v(4.39, -34) * mm, "end": v(5.26, -36.29) * mm});
            skLineSegment(sketch, "E1217", {"start": v(5.26, -36.29) * mm, "end": v(6.63, -38.45) * mm});
            skLineSegment(sketch, "E1218", {"start": v(6.63, -38.45) * mm, "end": v(7.83, -40.74) * mm});
            skLineSegment(sketch, "E1219", {"start": v(7.83, -40.74) * mm, "end": v(9.03, -43.5) * mm});
            skLineSegment(sketch, "E1220", {"start": v(9.03, -43.5) * mm, "end": v(10.12, -46.26) * mm});
            skLineSegment(sketch, "E1221", {"start": v(10.12, -46.26) * mm, "end": v(10.18, -48.58) * mm});
            skLineSegment(sketch, "E1222", {"start": v(10.18, -48.58) * mm, "end": v(10.1, -51.29) * mm});
            skLineSegment(sketch, "E1223", {"start": v(10.1, -51.29) * mm, "end": v(9.33, -53.12) * mm});
            skLineSegment(sketch, "E1224", {"start": v(9.33, -53.12) * mm, "end": v(13.27, -52.05) * mm});
            skLineSegment(sketch, "E1225", {"start": v(13.27, -52.05) * mm, "end": v(13.76, -49.92) * mm});
            skLineSegment(sketch, "E1226", {"start": v(13.76, -49.92) * mm, "end": v(13.81, -47.16) * mm});
            skLineSegment(sketch, "E1227", {"start": v(13.81, -47.16) * mm, "end": v(13.02, -44) * mm});
            skLineSegment(sketch, "E1228", {"start": v(13.02, -44) * mm, "end": v(11.33, -41.01) * mm});
            skLineSegment(sketch, "E1229", {"start": v(11.33, -41.01) * mm, "end": v(9.99, -38.53) * mm});
            skLineSegment(sketch, "E1230", {"start": v(9.99, -38.53) * mm, "end": v(8.54, -35.9) * mm});
            skLineSegment(sketch, "E1231", {"start": v(8.54, -35.9) * mm, "end": v(8.18, -34.27) * mm});
            skLineSegment(sketch, "E1232", {"start": v(8.18, -34.27) * mm, "end": v(8.21, -32.33) * mm});
            skLineSegment(sketch, "E1233", {"start": v(8.21, -32.33) * mm, "end": v(8.98, -29.65) * mm});
            skLineSegment(sketch, "E1234", {"start": v(8.98, -29.65) * mm, "end": v(11.87, -25.44) * mm});
            skLineSegment(sketch, "E1235", {"start": v(11.87, -25.44) * mm, "end": v(11.93, -25.3) * mm});
            skLineSegment(sketch, "E1236", {"start": v(11.93, -25.3) * mm, "end": v(15.01, -21.45) * mm});
            skLineSegment(sketch, "E1237", {"start": v(15.01, -21.45) * mm, "end": v(15.89, -19.51) * mm});
            skLineSegment(sketch, "E1238", {"start": v(15.89, -19.51) * mm, "end": v(15.62, -16) * mm});
            skLineSegment(sketch, "E1239", {"start": v(15.62, -16) * mm, "end": v(13.68, -12.3) * mm});
            skLineSegment(sketch, "E1240", {"start": v(13.68, -12.3) * mm, "end": v(11.33, -8.86) * mm});
            skLineSegment(sketch, "E1241", {"start": v(11.33, -8.86) * mm, "end": v(9.93, -6.84) * mm});
            skLineSegment(sketch, "E1242", {"start": v(9.93, -6.84) * mm, "end": v(9.44, -4.68) * mm});
            skLineSegment(sketch, "E1243", {"start": v(9.44, -4.68) * mm, "end": v(9.63, -2.17) * mm});
            skLineSegment(sketch, "E1244", {"start": v(9.63, -2.17) * mm, "end": v(10.73, 1.22) * mm});
            skLineSegment(sketch, "E1245", {"start": v(10.73, 1.22) * mm, "end": v(12.97, 5.56) * mm});
            skLineSegment(sketch, "E1246", {"start": v(12.97, 5.56) * mm, "end": v(14.36, 9.66) * mm});
            skLineSegment(sketch, "E1247", {"start": v(14.36, 9.66) * mm, "end": v(14.39, 15.07) * mm});
            skLineSegment(sketch, "E1248", {"start": v(14.39, 15.07) * mm, "end": v(13.02, 19.03) * mm});
            skLineSegment(sketch, "E1249", {"start": v(13.02, 19.03) * mm, "end": v(10.23, 22.83) * mm});
            skLineSegment(sketch, "E1250", {"start": v(10.23, 22.83) * mm, "end": v(12, 21.65) * mm});
            skLineSegment(sketch, "E1251", {"start": v(12, 21.65) * mm, "end": v(13.95, 19.66) * mm});
            skLineSegment(sketch, "E1252", {"start": v(13.95, 19.66) * mm, "end": v(15.8, 16.33) * mm});
            skLineSegment(sketch, "E1253", {"start": v(15.8, 16.33) * mm, "end": v(16.43, 13.9) * mm});
            skLineSegment(sketch, "E1254", {"start": v(16.43, 13.9) * mm, "end": v(16.43, 10.78) * mm});
            skLineSegment(sketch, "E1255", {"start": v(16.43, 10.78) * mm, "end": v(16.13, 8.65) * mm});
            skLineSegment(sketch, "E1256", {"start": v(16.13, 8.65) * mm, "end": v(15.34, 5.8) * mm});
            skFitSpline(sketch, "E1257", {"points": [v(13.13, -7.14) * mm, v(13.57, -7.8) * mm, v(14.02, -8.46) * mm, v(14.5, -9.1) * mm]});
            skFitSpline(sketch, "E1258", {"points": [v(14.5, -9.1) * mm, v(15.02, -9.82) * mm, v(15.57, -10.53) * mm, v(16.1, -11.24) * mm]});
            skFitSpline(sketch, "E1259", {"points": [v(16.1, -11.24) * mm, v(16.58, -11.86) * mm, v(17.04, -12.49) * mm, v(17.5, -13.12) * mm]});
            skLineSegment(sketch, "E1260", {"start": v(12.4, -2.11) * mm, "end": v(12.17, -4.57) * mm});
            skLineSegment(sketch, "E1261", {"start": v(12.17, -4.57) * mm, "end": v(13.13, -7.14) * mm});
            skFitSpline(sketch, "E1262", {"points": [v(17.1, -22.96) * mm, v(16.63, -23.6) * mm, v(16.14, -24.25) * mm, v(15.64, -24.87) * mm]});
            skFitSpline(sketch, "E1263", {"points": [v(15.64, -24.87) * mm, v(15.04, -25.62) * mm, v(14.41, -26.35) * mm, v(13.78, -27.08) * mm]});
            skFitSpline(sketch, "E1264", {"points": [v(13.78, -27.08) * mm, v(13.36, -27.57) * mm, v(12.95, -28.06) * mm, v(12.53, -28.56) * mm]});
            skLineSegment(sketch, "E1265", {"start": v(17.5, -13.12) * mm, "end": v(18.46, -14.76) * mm});
            skLineSegment(sketch, "E1266", {"start": v(18.46, -14.76) * mm, "end": v(18.95, -16.6) * mm});
            skLineSegment(sketch, "E1267", {"start": v(18.95, -16.6) * mm, "end": v(18.95, -19) * mm});
            skLineSegment(sketch, "E1268", {"start": v(18.95, -19) * mm, "end": v(18.3, -21.04) * mm});
            skLineSegment(sketch, "E1269", {"start": v(18.3, -21.04) * mm, "end": v(18.26, -21.15) * mm});
            skLineSegment(sketch, "E1270", {"start": v(18.26, -21.15) * mm, "end": v(17.1, -22.96) * mm});
            skFitSpline(sketch, "E1271", {"points": [v(12.61, -38.17) * mm, v(13.04, -38.87) * mm, v(13.48, -39.56) * mm, v(13.92, -40.25) * mm]});
            skFitSpline(sketch, "E1272", {"points": [v(13.92, -40.25) * mm, v(14.4, -41) * mm, v(14.89, -41.75) * mm, v(15.34, -42.52) * mm]});
            skFitSpline(sketch, "E1273", {"points": [v(15.34, -42.52) * mm, v(15.76, -43.21) * mm, v(16.15, -43.92) * mm, v(16.52, -44.65) * mm]});
            skLineSegment(sketch, "E1274", {"start": v(12.53, -28.56) * mm, "end": v(11.65, -30.14) * mm});
            skLineSegment(sketch, "E1275", {"start": v(11.65, -30.14) * mm, "end": v(11.27, -31.92) * mm});
            skLineSegment(sketch, "E1276", {"start": v(11.27, -31.92) * mm, "end": v(11.3, -34.32) * mm});
            skLineSegment(sketch, "E1277", {"start": v(11.3, -34.32) * mm, "end": v(11.68, -36.01) * mm});
            skLineSegment(sketch, "E1278", {"start": v(11.68, -36.01) * mm, "end": v(12.61, -38.17) * mm});
            skFitSpline(sketch, "E1279", {"points": [v(17.2, -28.17) * mm, v(17.75, -27.4) * mm, v(18.31, -26.63) * mm, v(18.9, -25.88) * mm]});
            skFitSpline(sketch, "E1280", {"points": [v(18.9, -25.88) * mm, v(19.5, -25.1) * mm, v(20.11, -24.34) * mm, v(20.75, -23.59) * mm]});
            skLineSegment(sketch, "E1281", {"start": v(16.52, -44.65) * mm, "end": v(17.45, -47.16) * mm});
            skLineSegment(sketch, "E1282", {"start": v(17.45, -47.16) * mm, "end": v(17.45, -49.95) * mm});
            skLineSegment(sketch, "E1283", {"start": v(17.45, -49.95) * mm, "end": v(17.36, -50.96) * mm});
            skLineSegment(sketch, "E1284", {"start": v(17.36, -50.96) * mm, "end": v(21, -49.81) * mm});
            skLineSegment(sketch, "E1285", {"start": v(21, -49.81) * mm, "end": v(20.97, -46.59) * mm});
            skLineSegment(sketch, "E1286", {"start": v(20.97, -46.59) * mm, "end": v(20.15, -44.35) * mm});
            skLineSegment(sketch, "E1287", {"start": v(20.15, -44.35) * mm, "end": v(19, -42.4) * mm});
            skLineSegment(sketch, "E1288", {"start": v(19, -42.4) * mm, "end": v(16.79, -39.24) * mm});
            skLineSegment(sketch, "E1289", {"start": v(16.79, -39.24) * mm, "end": v(15.48, -36.92) * mm});
            skLineSegment(sketch, "E1290", {"start": v(15.48, -36.92) * mm, "end": v(15.15, -35) * mm});
            skLineSegment(sketch, "E1291", {"start": v(15.15, -35) * mm, "end": v(15.15, -32.65) * mm});
            skLineSegment(sketch, "E1292", {"start": v(15.15, -32.65) * mm, "end": v(15.75, -30.69) * mm});
            skLineSegment(sketch, "E1293", {"start": v(15.75, -30.69) * mm, "end": v(17.2, -28.17) * mm});
            skFitSpline(sketch, "E1294", {"points": [v(19.96, -11.37) * mm, v(19.32, -10.55) * mm, v(18.7, -9.7) * mm, v(18.1, -8.83) * mm]});
            skFitSpline(sketch, "E1295", {"points": [v(18.1, -8.83) * mm, v(17.54, -8.02) * mm, v(17, -7.2) * mm, v(16.49, -6.35) * mm]});
            skLineSegment(sketch, "E1296", {"start": v(20.75, -23.59) * mm, "end": v(22.14, -21.5) * mm});
            skLineSegment(sketch, "E1297", {"start": v(22.14, -21.5) * mm, "end": v(22.64, -19.57) * mm});
            skLineSegment(sketch, "E1298", {"start": v(22.64, -19.57) * mm, "end": v(22.53, -16.7) * mm});
            skLineSegment(sketch, "E1299", {"start": v(22.53, -16.7) * mm, "end": v(21.57, -14.16) * mm});
            skLineSegment(sketch, "E1300", {"start": v(21.57, -14.16) * mm, "end": v(19.96, -11.37) * mm});
            skFitSpline(sketch, "E1301", {"points": [v(15.56, -1.62) * mm, v(15.8, -0.9) * mm, v(16.07, -0.2) * mm, v(16.35, 0.5) * mm]});
            skFitSpline(sketch, "E1302", {"points": [v(16.35, 0.5) * mm, v(16.7, 1.38) * mm, v(17.08, 2.25) * mm, v(17.47, 3.1) * mm]});
            skFitSpline(sketch, "E1303", {"points": [v(17.47, 3.1) * mm, v(17.82, 3.86) * mm, v(18.17, 4.62) * mm, v(18.54, 5.37) * mm]});
            skLineSegment(sketch, "E1304", {"start": v(16.49, -6.35) * mm, "end": v(15.97, -5.06) * mm});
            skLineSegment(sketch, "E1305", {"start": v(15.97, -5.06) * mm, "end": v(15.67, -3.72) * mm});
            skLineSegment(sketch, "E1306", {"start": v(15.67, -3.72) * mm, "end": v(15.56, -1.62) * mm});
            skFitSpline(sketch, "E1307", {"points": [v(21.02, 5.9) * mm, v(20.75, 5.1) * mm, v(20.49, 4.3) * mm, v(20.23, 3.51) * mm]});
            skFitSpline(sketch, "E1308", {"points": [v(20.23, 3.51) * mm, v(19.97, 2.7) * mm, v(19.73, 1.9) * mm, v(19.5, 1.08) * mm]});
            skFitSpline(sketch, "E1309", {"points": [v(19.5, 1.08) * mm, v(19.28, 0.35) * mm, v(19.08, -0.39) * mm, v(18.9, -1.13) * mm]});
            skLineSegment(sketch, "E1310", {"start": v(18.54, 5.37) * mm, "end": v(19.25, 8.43) * mm});
            skLineSegment(sketch, "E1311", {"start": v(19.25, 8.43) * mm, "end": v(19.28, 12.31) * mm});
            skLineSegment(sketch, "E1312", {"start": v(19.28, 12.31) * mm, "end": v(18.73, 15.45) * mm});
            skLineSegment(sketch, "E1313", {"start": v(18.73, 15.45) * mm, "end": v(17.7, 18) * mm});
            skLineSegment(sketch, "E1314", {"start": v(17.7, 18) * mm, "end": v(16.27, 20.31) * mm});
            skLineSegment(sketch, "E1315", {"start": v(16.27, 20.31) * mm, "end": v(15.34, 21.46) * mm});
            skLineSegment(sketch, "E1316", {"start": v(15.34, 21.46) * mm, "end": v(15.89, 21.33) * mm});
            skLineSegment(sketch, "E1317", {"start": v(15.89, 21.33) * mm, "end": v(16.9, 20.64) * mm});
            skLineSegment(sketch, "E1318", {"start": v(16.9, 20.64) * mm, "end": v(18.1, 19.36) * mm});
            skLineSegment(sketch, "E1319", {"start": v(18.1, 19.36) * mm, "end": v(18.16, 19.22) * mm});
            skLineSegment(sketch, "E1320", {"start": v(18.16, 19.22) * mm, "end": v(19.99, 16.63) * mm});
            skLineSegment(sketch, "E1321", {"start": v(19.99, 16.63) * mm, "end": v(20.91, 14.17) * mm});
            skLineSegment(sketch, "E1322", {"start": v(20.91, 14.17) * mm, "end": v(21.3, 12.83) * mm});
            skLineSegment(sketch, "E1323", {"start": v(21.3, 12.83) * mm, "end": v(21.52, 11.05) * mm});
            skLineSegment(sketch, "E1324", {"start": v(21.52, 11.05) * mm, "end": v(21.57, 8.49) * mm});
            skLineSegment(sketch, "E1325", {"start": v(21.57, 8.49) * mm, "end": v(21.02, 5.9) * mm});
            skFitSpline(sketch, "E1326", {"points": [v(20.48, -8.26) * mm, v(21.21, -9.24) * mm, v(21.94, -10.22) * mm, v(22.66, -11.21) * mm]});
            skFitSpline(sketch, "E1327", {"points": [v(22.66, -11.21) * mm, v(23.15, -11.87) * mm, v(23.63, -12.54) * mm, v(24.11, -13.2) * mm]});
            skLineSegment(sketch, "E1328", {"start": v(18.9, -1.13) * mm, "end": v(18.65, -3.29) * mm});
            skLineSegment(sketch, "E1329", {"start": v(18.65, -3.29) * mm, "end": v(19.22, -6.07) * mm});
            skLineSegment(sketch, "E1330", {"start": v(19.22, -6.07) * mm, "end": v(20.48, -8.26) * mm});
            skFitSpline(sketch, "E1331", {"points": [v(24.71, -21.56) * mm, v(24.21, -22.27) * mm, v(23.71, -22.97) * mm, v(23.2, -23.67) * mm]});
            skFitSpline(sketch, "E1332", {"points": [v(23.2, -23.67) * mm, v(22.38, -24.83) * mm, v(21.54, -25.99) * mm, v(20.7, -27.14) * mm]});
            skFitSpline(sketch, "E1333", {"points": [v(20.7, -27.14) * mm, v(19.94, -28.16) * mm, v(19.18, -29.18) * mm, v(18.4, -30.2) * mm]});
            skLineSegment(sketch, "E1334", {"start": v(24.11, -13.2) * mm, "end": v(25.2, -15.23) * mm});
            skLineSegment(sketch, "E1335", {"start": v(25.2, -15.23) * mm, "end": v(25.64, -17.17) * mm});
            skLineSegment(sketch, "E1336", {"start": v(25.64, -17.17) * mm, "end": v(25.64, -19.43) * mm});
            skLineSegment(sketch, "E1337", {"start": v(25.64, -19.43) * mm, "end": v(24.71, -21.56) * mm});
            skFitSpline(sketch, "E1338", {"points": [v(18.76, -36.94) * mm, v(19.2, -37.72) * mm, v(19.67, -38.48) * mm, v(20.15, -39.24) * mm]});
            skFitSpline(sketch, "E1339", {"points": [v(20.15, -39.24) * mm, v(20.75, -40.2) * mm, v(21.38, -41.13) * mm, v(22.03, -42.05) * mm]});
            skLineSegment(sketch, "E1340", {"start": v(18.4, -30.2) * mm, "end": v(17.72, -32.2) * mm});
            skLineSegment(sketch, "E1341", {"start": v(17.72, -32.2) * mm, "end": v(17.72, -34.16) * mm});
            skLineSegment(sketch, "E1342", {"start": v(17.72, -34.16) * mm, "end": v(18.76, -36.94) * mm});
            skFitSpline(sketch, "E1343", {"points": [v(26.54, -43.72) * mm, v(26.05, -42.96) * mm, v(25.56, -42.2) * mm, v(25.07, -41.45) * mm]});
            skFitSpline(sketch, "E1344", {"points": [v(25.07, -41.45) * mm, v(24.56, -40.67) * mm, v(24.05, -39.9) * mm, v(23.56, -39.1) * mm]});
            skFitSpline(sketch, "E1345", {"points": [v(23.56, -39.1) * mm, v(23, -38.17) * mm, v(22.46, -37.23) * mm, v(21.95, -36.26) * mm]});
            skLineSegment(sketch, "E1346", {"start": v(22.03, -42.05) * mm, "end": v(23.5, -44.95) * mm});
            skLineSegment(sketch, "E1347", {"start": v(23.5, -44.95) * mm, "end": v(24.22, -47.1) * mm});
            skLineSegment(sketch, "E1348", {"start": v(24.22, -47.1) * mm, "end": v(24.25, -48.55) * mm});
            skLineSegment(sketch, "E1349", {"start": v(24.25, -48.55) * mm, "end": v(27.36, -46.8) * mm});
            skLineSegment(sketch, "E1350", {"start": v(27.36, -46.8) * mm, "end": v(27.12, -45.44) * mm});
            skLineSegment(sketch, "E1351", {"start": v(27.12, -45.44) * mm, "end": v(26.54, -43.72) * mm});
            skFitSpline(sketch, "E1352", {"points": [v(34.63, -41.83) * mm, v(34.18, -41.47) * mm, v(33.71, -41.13) * mm, v(33.24, -40.8) * mm]});
            skFitSpline(sketch, "E1353", {"points": [v(33.24, -40.8) * mm, v(32.97, -40.6) * mm, v(32.7, -40.43) * mm, v(32.42, -40.25) * mm]});
            skLineSegment(sketch, "E1354", {"start": v(21.95, -36.26) * mm, "end": v(21.73, -35.93) * mm});
            skLineSegment(sketch, "E1355", {"start": v(21.73, -35.93) * mm, "end": v(21.7, -32.57) * mm});
            skLineSegment(sketch, "E1356", {"start": v(21.7, -32.57) * mm, "end": v(22.39, -30.8) * mm});
            skLineSegment(sketch, "E1357", {"start": v(22.39, -30.8) * mm, "end": v(22.66, -30.9) * mm});
            skLineSegment(sketch, "E1358", {"start": v(22.66, -30.9) * mm, "end": v(22.8, -32.82) * mm});
            skLineSegment(sketch, "E1359", {"start": v(22.8, -32.82) * mm, "end": v(23.18, -34.62) * mm});
            skLineSegment(sketch, "E1360", {"start": v(23.18, -34.62) * mm, "end": v(24.08, -36.59) * mm});
            skLineSegment(sketch, "E1361", {"start": v(24.08, -36.59) * mm, "end": v(25.59, -39.13) * mm});
            skLineSegment(sketch, "E1362", {"start": v(25.59, -39.13) * mm, "end": v(27.66, -42.02) * mm});
            skLineSegment(sketch, "E1363", {"start": v(27.66, -42.02) * mm, "end": v(28.7, -44.13) * mm});
            skLineSegment(sketch, "E1364", {"start": v(28.7, -44.13) * mm, "end": v(29.22, -45.55) * mm});
            skLineSegment(sketch, "E1365", {"start": v(29.22, -45.55) * mm, "end": v(34.63, -41.83) * mm});
            skFitSpline(sketch, "E1366", {"points": [v(26.98, -12.47) * mm, v(26, -11.07) * mm, v(25.04, -9.65) * mm, v(24.11, -8.2) * mm]});
            skFitSpline(sketch, "E1367", {"points": [v(24.11, -8.2) * mm, v(23.5, -7.25) * mm, v(22.9, -6.28) * mm, v(22.3, -5.3) * mm]});
            skLineSegment(sketch, "E1368", {"start": v(32.42, -40.25) * mm, "end": v(32.44, -39.51) * mm});
            skLineSegment(sketch, "E1369", {"start": v(32.44, -39.51) * mm, "end": v(33.86, -37.95) * mm});
            skLineSegment(sketch, "E1370", {"start": v(33.86, -37.95) * mm, "end": v(37.28, -39.1) * mm});
            skLineSegment(sketch, "E1371", {"start": v(37.28, -39.1) * mm, "end": v(40, -36.32) * mm});
            skLineSegment(sketch, "E1372", {"start": v(40, -36.32) * mm, "end": v(38.29, -35.25) * mm});
            skLineSegment(sketch, "E1373", {"start": v(38.29, -35.25) * mm, "end": v(36.08, -34.57) * mm});
            skLineSegment(sketch, "E1374", {"start": v(36.08, -34.57) * mm, "end": v(36.05, -33.75) * mm});
            skLineSegment(sketch, "E1375", {"start": v(36.05, -33.75) * mm, "end": v(36.98, -32.44) * mm});
            skLineSegment(sketch, "E1376", {"start": v(36.98, -32.44) * mm, "end": v(38.64, -32.5) * mm});
            skLineSegment(sketch, "E1377", {"start": v(38.64, -32.5) * mm, "end": v(40.86, -33.06) * mm});
            skLineSegment(sketch, "E1378", {"start": v(40.86, -33.06) * mm, "end": v(42.69, -34.02) * mm});
            skLineSegment(sketch, "E1379", {"start": v(42.69, -34.02) * mm, "end": v(44.98, -31.07) * mm});
            skLineSegment(sketch, "E1380", {"start": v(44.98, -31.07) * mm, "end": v(39.33, -28.2) * mm});
            skLineSegment(sketch, "E1381", {"start": v(39.33, -28.2) * mm, "end": v(38.56, -28.31) * mm});
            skLineSegment(sketch, "E1382", {"start": v(38.56, -28.31) * mm, "end": v(37.69, -29.9) * mm});
            skLineSegment(sketch, "E1383", {"start": v(37.69, -29.9) * mm, "end": v(36.9, -31.8) * mm});
            skLineSegment(sketch, "E1384", {"start": v(36.9, -31.8) * mm, "end": v(35.31, -31.75) * mm});
            skLineSegment(sketch, "E1385", {"start": v(35.31, -31.75) * mm, "end": v(32.28, -30.9) * mm});
            skLineSegment(sketch, "E1386", {"start": v(32.28, -30.9) * mm, "end": v(29.77, -29.24) * mm});
            skLineSegment(sketch, "E1387", {"start": v(29.77, -29.24) * mm, "end": v(26.19, -26.26) * mm});
            skLineSegment(sketch, "E1388", {"start": v(26.19, -26.26) * mm, "end": v(26.51, -25.28) * mm});
            skLineSegment(sketch, "E1389", {"start": v(26.51, -25.28) * mm, "end": v(27.72, -23.04) * mm});
            skLineSegment(sketch, "E1390", {"start": v(27.72, -23.04) * mm, "end": v(28.78, -20.44) * mm});
            skLineSegment(sketch, "E1391", {"start": v(28.78, -20.44) * mm, "end": v(28.92, -16.92) * mm});
            skLineSegment(sketch, "E1392", {"start": v(28.92, -16.92) * mm, "end": v(28.2, -14.68) * mm});
            skLineSegment(sketch, "E1393", {"start": v(28.2, -14.68) * mm, "end": v(26.98, -12.47) * mm});
            skFitSpline(sketch, "E1394", {"points": [v(26.4, 4.5) * mm, v(26.12, 3.6) * mm, v(25.83, 2.7) * mm, v(25.53, 1.8) * mm]});
            skFitSpline(sketch, "E1395", {"points": [v(25.53, 1.8) * mm, v(25.27, 1) * mm, v(25, 0.19) * mm, v(24.74, -0.61) * mm]});
            skLineSegment(sketch, "E1396", {"start": v(22.3, -5.3) * mm, "end": v(21.82, -2.36) * mm});
            skLineSegment(sketch, "E1397", {"start": v(21.82, -2.36) * mm, "end": v(22.42, 0.95) * mm});
            skLineSegment(sketch, "E1398", {"start": v(22.42, 0.95) * mm, "end": v(23.73, 4.99) * mm});
            skLineSegment(sketch, "E1399", {"start": v(23.73, 4.99) * mm, "end": v(24.27, 8.81) * mm});
            skLineSegment(sketch, "E1400", {"start": v(24.27, 8.81) * mm, "end": v(24.22, 11.68) * mm});
            skLineSegment(sketch, "E1401", {"start": v(24.22, 11.68) * mm, "end": v(23.05, 15.23) * mm});
            skLineSegment(sketch, "E1402", {"start": v(23.05, 15.23) * mm, "end": v(21.27, 19.03) * mm});
            skLineSegment(sketch, "E1403", {"start": v(21.27, 19.03) * mm, "end": v(22.58, 18.13) * mm});
            skLineSegment(sketch, "E1404", {"start": v(22.58, 18.13) * mm, "end": v(24.14, 16.7) * mm});
            skLineSegment(sketch, "E1405", {"start": v(24.14, 16.7) * mm, "end": v(25.07, 14.74) * mm});
            skLineSegment(sketch, "E1406", {"start": v(25.07, 14.74) * mm, "end": v(26.05, 11.76) * mm});
            skLineSegment(sketch, "E1407", {"start": v(26.05, 11.76) * mm, "end": v(26.49, 8.38) * mm});
            skLineSegment(sketch, "E1408", {"start": v(26.49, 8.38) * mm, "end": v(26.4, 4.5) * mm});
            skFitSpline(sketch, "E1409", {"points": [v(25.8, -6.51) * mm, v(26.35, -7.4) * mm, v(26.9, -8.28) * mm, v(27.44, -9.16) * mm]});
            skFitSpline(sketch, "E1410", {"points": [v(27.44, -9.16) * mm, v(28.08, -10.2) * mm, v(28.72, -11.22) * mm, v(29.36, -12.25) * mm]});
            skFitSpline(sketch, "E1411", {"points": [v(29.36, -12.25) * mm, v(29.85, -13.03) * mm, v(30.34, -13.82) * mm, v(30.83, -14.6) * mm]});
            skLineSegment(sketch, "E1412", {"start": v(24.74, -0.61) * mm, "end": v(24.68, -3.5) * mm});
            skLineSegment(sketch, "E1413", {"start": v(24.68, -3.5) * mm, "end": v(25.8, -6.51) * mm});
            skFitSpline(sketch, "E1414", {"points": [v(31.43, -18.15) * mm, v(31.99, -18.51) * mm, v(32.53, -18.89) * mm, v(33.07, -19.27) * mm]});
            skFitSpline(sketch, "E1415", {"points": [v(33.07, -19.27) * mm, v(33.82, -19.8) * mm, v(34.56, -20.36) * mm, v(35.28, -20.94) * mm]});
            skLineSegment(sketch, "E1416", {"start": v(30.83, -14.6) * mm, "end": v(31.46, -16.76) * mm});
            skLineSegment(sketch, "E1417", {"start": v(31.46, -16.76) * mm, "end": v(31.43, -18.15) * mm});
            skFitSpline(sketch, "E1418", {"points": [v(47.06, -24.27) * mm, v(46.37, -23.82) * mm, v(45.67, -23.4) * mm, v(44.95, -22.98) * mm]});
            skFitSpline(sketch, "E1419", {"points": [v(44.95, -22.98) * mm, v(44.37, -22.64) * mm, v(43.78, -22.32) * mm, v(43.18, -22) * mm]});
            skLineSegment(sketch, "E1420", {"start": v(35.28, -20.94) * mm, "end": v(37.22, -22.06) * mm});
            skLineSegment(sketch, "E1421", {"start": v(37.22, -22.06) * mm, "end": v(39.87, -22.06) * mm});
            skLineSegment(sketch, "E1422", {"start": v(39.87, -22.06) * mm, "end": v(39.35, -25.47) * mm});
            skLineSegment(sketch, "E1423", {"start": v(39.35, -25.47) * mm, "end": v(41.32, -25.63) * mm});
            skLineSegment(sketch, "E1424", {"start": v(41.32, -25.63) * mm, "end": v(43.18, -26.34) * mm});
            skLineSegment(sketch, "E1425", {"start": v(43.18, -26.34) * mm, "end": v(45.15, -27.5) * mm});
            skLineSegment(sketch, "E1426", {"start": v(45.15, -27.5) * mm, "end": v(46.95, -28.23) * mm});
            skLineSegment(sketch, "E1427", {"start": v(46.95, -28.23) * mm, "end": v(48.8, -25.09) * mm});
            skLineSegment(sketch, "E1428", {"start": v(48.8, -25.09) * mm, "end": v(47.06, -24.27) * mm});
            skFitSpline(sketch, "E1429", {"points": [v(44.87, -19.4) * mm, v(45.73, -19.88) * mm, v(46.6, -20.33) * mm, v(47.47, -20.77) * mm]});
            skFitSpline(sketch, "E1430", {"points": [v(47.47, -20.77) * mm, v(48.27, -21.18) * mm, v(49.08, -21.57) * mm, v(49.9, -21.95) * mm]});
            skLineSegment(sketch, "E1431", {"start": v(43.18, -22) * mm, "end": v(41.4, -21.34) * mm});
            skLineSegment(sketch, "E1432", {"start": v(41.4, -21.34) * mm, "end": v(40.23, -21.32) * mm});
            skLineSegment(sketch, "E1433", {"start": v(40.23, -21.32) * mm, "end": v(40.97, -18.5) * mm});
            skLineSegment(sketch, "E1434", {"start": v(40.97, -18.5) * mm, "end": v(42.52, -18.56) * mm});
            skLineSegment(sketch, "E1435", {"start": v(42.52, -18.56) * mm, "end": v(44.87, -19.4) * mm});
            skFitSpline(sketch, "E1436", {"points": [v(49.43, -17.55) * mm, v(48.36, -17.03) * mm, v(47.3, -16.5) * mm, v(46.24, -15.94) * mm]});
            skFitSpline(sketch, "E1437", {"points": [v(46.24, -15.94) * mm, v(45.52, -15.56) * mm, v(44.81, -15.16) * mm, v(44.1, -14.76) * mm]});
            skLineSegment(sketch, "E1438", {"start": v(49.9, -21.95) * mm, "end": v(50.28, -22) * mm});
            skLineSegment(sketch, "E1439", {"start": v(50.28, -22) * mm, "end": v(51.24, -20.66) * mm});
            skLineSegment(sketch, "E1440", {"start": v(51.24, -20.66) * mm, "end": v(52.06, -18.26) * mm});
            skLineSegment(sketch, "E1441", {"start": v(52.06, -18.26) * mm, "end": v(49.43, -17.55) * mm});
            skFitSpline(sketch, "E1442", {"points": [v(43.34, -11.13) * mm, v(44.36, -11.52) * mm, v(45.35, -11.96) * mm, v(46.32, -12.44) * mm]});
            skFitSpline(sketch, "E1443", {"points": [v(46.32, -12.44) * mm, v(47.1, -12.83) * mm, v(47.88, -13.25) * mm, v(48.67, -13.64) * mm]});
            skFitSpline(sketch, "E1444", {"points": [v(48.67, -13.64) * mm, v(49.48, -14.04) * mm, v(50.31, -14.4) * mm, v(51.16, -14.73) * mm]});
            skLineSegment(sketch, "E1445", {"start": v(44.1, -14.76) * mm, "end": v(41.98, -13.89) * mm});
            skLineSegment(sketch, "E1446", {"start": v(41.98, -13.89) * mm, "end": v(41.16, -13.75) * mm});
            skLineSegment(sketch, "E1447", {"start": v(41.16, -13.75) * mm, "end": v(41.16, -10.88) * mm});
            skLineSegment(sketch, "E1448", {"start": v(41.16, -10.88) * mm, "end": v(43.34, -11.13) * mm});
            skFitSpline(sketch, "E1449", {"points": [v(50.25, -10.25) * mm, v(49.36, -9.8) * mm, v(48.47, -9.33) * mm, v(47.58, -8.86) * mm]});
            skFitSpline(sketch, "E1450", {"points": [v(47.58, -8.86) * mm, v(46.46, -8.27) * mm, v(45.35, -7.68) * mm, v(44.24, -7.09) * mm]});
            skLineSegment(sketch, "E1451", {"start": v(51.16, -14.73) * mm, "end": v(52.58, -15.12) * mm});
            skLineSegment(sketch, "E1452", {"start": v(52.58, -15.12) * mm, "end": v(52.74, -15.12) * mm});
            skLineSegment(sketch, "E1453", {"start": v(52.74, -15.12) * mm, "end": v(53.64, -14.52) * mm});
            skLineSegment(sketch, "E1454", {"start": v(53.64, -14.52) * mm, "end": v(54.22, -10.88) * mm});
            skLineSegment(sketch, "E1455", {"start": v(54.22, -10.88) * mm, "end": v(52.8, -10.88) * mm});
            skLineSegment(sketch, "E1456", {"start": v(52.8, -10.88) * mm, "end": v(50.25, -10.25) * mm});
            skLineSegment(sketch, "E1457", {"start": v(44.24, -7.09) * mm, "end": v(41.98, -6.32) * mm});
            skLineSegment(sketch, "E1458", {"start": v(41.98, -6.32) * mm, "end": v(40.53, -6.21) * mm});
            skLineSegment(sketch, "E1459", {"start": v(40.53, -6.21) * mm, "end": v(39.9, -3.07) * mm});
            skLineSegment(sketch, "E1460", {"start": v(39.9, -3.07) * mm, "end": v(42.14, -3.12) * mm});
            skLineSegment(sketch, "E1461", {"start": v(42.14, -3.12) * mm, "end": v(44.5, -3.92) * mm});
            skLineSegment(sketch, "E1462", {"start": v(44.5, -3.92) * mm, "end": v(47.63, -5.34) * mm});
            skFitSpline(sketch, "E1463", {"points": [v(49.3, 12.8) * mm, v(50.03, 11.85) * mm, v(50.74, 10.89) * mm, v(51.43, 9.9) * mm]});
            skFitSpline(sketch, "E1464", {"points": [v(51.43, 9.9) * mm, v(52.18, 8.85) * mm, v(52.9, 7.77) * mm, v(53.61, 6.68) * mm]});
            skLineSegment(sketch, "E1465", {"start": v(45.3, 27.44) * mm, "end": v(44.87, 25.15) * mm});
            skLineSegment(sketch, "E1466", {"start": v(44.87, 25.15) * mm, "end": v(45.15, 21.98) * mm});
            skLineSegment(sketch, "E1467", {"start": v(45.15, 21.98) * mm, "end": v(45.7, 19.63) * mm});
            skLineSegment(sketch, "E1468", {"start": v(45.7, 19.63) * mm, "end": v(47.22, 16.14) * mm});
            skLineSegment(sketch, "E1469", {"start": v(47.22, 16.14) * mm, "end": v(49.3, 12.8) * mm});
            skFitSpline(sketch, "E1470", {"points": [v(48.8, 5.7) * mm, v(48.13, 5.94) * mm, v(47.45, 6.2) * mm, v(46.78, 6.46) * mm]});
            skFitSpline(sketch, "E1471", {"points": [v(46.78, 6.46) * mm, v(46.03, 6.76) * mm, v(45.29, 7.07) * mm, v(44.54, 7.4) * mm]});
            skLineSegment(sketch, "E1472", {"start": v(53.61, 6.68) * mm, "end": v(51.48, 5.75) * mm});
            skLineSegment(sketch, "E1473", {"start": v(51.48, 5.75) * mm, "end": v(48.8, 5.7) * mm});
            skFitSpline(sketch, "E1474", {"points": [v(27.72, 16.9) * mm, v(26.9, 17.55) * mm, v(26.07, 18.17) * mm, v(25.2, 18.76) * mm]});
            skFitSpline(sketch, "E1475", {"points": [v(25.2, 18.76) * mm, v(24.79, 19.04) * mm, v(24.37, 19.31) * mm, v(23.95, 19.58) * mm]});
            skLineSegment(sketch, "E1476", {"start": v(44.54, 7.4) * mm, "end": v(42.3, 8.76) * mm});
            skLineSegment(sketch, "E1477", {"start": v(42.3, 8.76) * mm, "end": v(41.81, 8.76) * mm});
            skLineSegment(sketch, "E1478", {"start": v(41.81, 8.76) * mm, "end": v(39.57, 9.69) * mm});
            skLineSegment(sketch, "E1479", {"start": v(39.57, 9.69) * mm, "end": v(37, 9.69) * mm});
            skLineSegment(sketch, "E1480", {"start": v(37, 9.69) * mm, "end": v(34.27, 9.41) * mm});
            skLineSegment(sketch, "E1481", {"start": v(34.27, 9.41) * mm, "end": v(31.76, 12.86) * mm});
            skLineSegment(sketch, "E1482", {"start": v(31.76, 12.86) * mm, "end": v(29.74, 15.1) * mm});
            skLineSegment(sketch, "E1483", {"start": v(29.74, 15.1) * mm, "end": v(27.72, 16.9) * mm});
            skFitSpline(sketch, "E1484", {"points": [v(25.59, 20.67) * mm, v(26.31, 20.7) * mm, v(27.04, 20.74) * mm, v(27.77, 20.78) * mm]});
            skFitSpline(sketch, "E1485", {"points": [v(27.77, 20.78) * mm, v(28.6, 20.82) * mm, v(29.41, 20.85) * mm, v(30.23, 20.89) * mm]});
            skLineSegment(sketch, "E1486", {"start": v(23.95, 19.58) * mm, "end": v(24.55, 20.23) * mm});
            skLineSegment(sketch, "E1487", {"start": v(24.55, 20.23) * mm, "end": v(25.59, 20.67) * mm});
            skFitSpline(sketch, "E1488", {"points": [v(32.52, 20.29) * mm, v(33.3, 20.04) * mm, v(34.06, 19.76) * mm, v(34.82, 19.47) * mm]});
            skFitSpline(sketch, "E1489", {"points": [v(34.82, 19.47) * mm, v(35.53, 19.19) * mm, v(36.24, 18.89) * mm, v(36.95, 18.6) * mm]});
            skFitSpline(sketch, "E1490", {"points": [v(36.95, 18.6) * mm, v(37.17, 18.5) * mm, v(37.39, 18.41) * mm, v(37.6, 18.32) * mm]});
            skLineSegment(sketch, "E1491", {"start": v(30.23, 20.89) * mm, "end": v(32.52, 20.29) * mm});
            skFitSpline(sketch, "E1492", {"points": [v(-44.51, 26.9) * mm, v(-44.47, 26.08) * mm, v(-44.46, 25.26) * mm, v(-44.46, 24.44) * mm]});
            skLineSegment(sketch, "E1493", {"start": v(37.6, 18.32) * mm, "end": v(38.1, 19.63) * mm});
            skLineSegment(sketch, "E1494", {"start": v(38.1, 19.63) * mm, "end": v(38.92, 22.58) * mm});
            skLineSegment(sketch, "E1495", {"start": v(38.92, 22.58) * mm, "end": v(40.34, 25.1) * mm});
            skLineSegment(sketch, "E1496", {"start": v(40.34, 25.1) * mm, "end": v(42.25, 27.23) * mm});
            skLineSegment(sketch, "E1497", {"start": v(42.25, 27.23) * mm, "end": v(44.16, 28.32) * mm});
            skLineSegment(sketch, "E1498", {"start": v(44.16, 28.32) * mm, "end": v(44.98, 28.16) * mm});
            skLineSegment(sketch, "E1499", {"start": v(44.98, 28.16) * mm, "end": v(45.3, 27.44) * mm});
            skFitSpline(sketch, "E1500", {"points": [v(-44.62, 22.42) * mm, v(-44.9, 21.48) * mm, v(-45.18, 20.55) * mm, v(-45.5, 19.63) * mm]});
            skFitSpline(sketch, "E1501", {"points": [v(-45.5, 19.63) * mm, v(-45.82, 18.68) * mm, v(-46.16, 17.73) * mm, v(-46.53, 16.8) * mm]});
            skFitSpline(sketch, "E1502", {"points": [v(-46.53, 16.8) * mm, v(-47.12, 15.92) * mm, v(-47.7, 15.05) * mm, v(-48.28, 14.17) * mm]});
            skFitSpline(sketch, "E1503", {"points": [v(-48.28, 14.17) * mm, v(-48.82, 13.35) * mm, v(-49.36, 12.52) * mm, v(-49.92, 11.7) * mm]});
            skFitSpline(sketch, "E1504", {"points": [v(-49.92, 11.7) * mm, v(-50.48, 10.9) * mm, v(-51.05, 10.1) * mm, v(-51.61, 9.3) * mm]});
            skFitSpline(sketch, "E1505", {"points": [v(-51.61, 9.3) * mm, v(-52.17, 8.53) * mm, v(-52.71, 7.74) * mm, v(-53.25, 6.96) * mm]});
            skLineSegment(sketch, "E1506", {"start": v(-44.46, 24.44) * mm, "end": v(-44.62, 22.42) * mm});
            skFitSpline(sketch, "E1507", {"points": [v(-52.49, 6.14) * mm, v(-51.78, 6.13) * mm, v(-51.07, 6.13) * mm, v(-50.36, 6.14) * mm]});
            skFitSpline(sketch, "E1508", {"points": [v(-50.36, 6.14) * mm, v(-49.52, 6.15) * mm, v(-48.68, 6.16) * mm, v(-47.84, 6.2) * mm]});
            skFitSpline(sketch, "E1509", {"points": [v(-47.84, 6.2) * mm, v(-47.04, 6.5) * mm, v(-46.24, 6.84) * mm, v(-45.44, 7.17) * mm]});
            skFitSpline(sketch, "E1510", {"points": [v(-45.44, 7.17) * mm, v(-43.95, 7.8) * mm, v(-42.47, 8.48) * mm, v(-41.01, 9.2) * mm]});
            skLineSegment(sketch, "E1511", {"start": v(-53.25, 6.96) * mm, "end": v(-52.49, 6.14) * mm});
            skFitSpline(sketch, "E1512", {"points": [v(-31.02, 20.62) * mm, v(-31.66, 20.45) * mm, v(-32.3, 20.27) * mm, v(-32.93, 20.07) * mm]});
            skFitSpline(sketch, "E1513", {"points": [v(-32.93, 20.07) * mm, v(-33.7, 19.83) * mm, v(-34.46, 19.56) * mm, v(-35.22, 19.3) * mm]});
            skFitSpline(sketch, "E1514", {"points": [v(-35.22, 19.3) * mm, v(-35.92, 19.07) * mm, v(-36.62, 18.85) * mm, v(-37.3, 18.6) * mm]});
            skFitSpline(sketch, "E1515", {"points": [v(-37.3, 18.6) * mm, v(-37.48, 18.52) * mm, v(-37.67, 18.45) * mm, v(-37.85, 18.38) * mm]});
            skLineSegment(sketch, "E1516", {"start": v(-41.01, 9.2) * mm, "end": v(-37.85, 9.85) * mm});
            skLineSegment(sketch, "E1517", {"start": v(-37.85, 9.85) * mm, "end": v(-35.6, 9.85) * mm});
            skLineSegment(sketch, "E1518", {"start": v(-35.6, 9.85) * mm, "end": v(-34.02, 9.74) * mm});
            skLineSegment(sketch, "E1519", {"start": v(-34.02, 9.74) * mm, "end": v(-31.84, 12.64) * mm});
            skLineSegment(sketch, "E1520", {"start": v(-31.84, 12.64) * mm, "end": v(-29.54, 15.2) * mm});
            skLineSegment(sketch, "E1521", {"start": v(-29.54, 15.2) * mm, "end": v(-26.97, 17.45) * mm});
            skLineSegment(sketch, "E1522", {"start": v(-26.97, 17.45) * mm, "end": v(-23.64, 19.74) * mm});
            skLineSegment(sketch, "E1523", {"start": v(-23.64, 19.74) * mm, "end": v(-24.9, 20.45) * mm});
            skLineSegment(sketch, "E1524", {"start": v(-24.9, 20.45) * mm, "end": v(-27.57, 21.05) * mm});
            skLineSegment(sketch, "E1525", {"start": v(-27.57, 21.05) * mm, "end": v(-29.49, 20.94) * mm});
            skLineSegment(sketch, "E1526", {"start": v(-29.49, 20.94) * mm, "end": v(-31.02, 20.62) * mm});
            skFitSpline(sketch, "E1527", {"points": [v(-38.72, 22.8) * mm, v(-39.17, 23.48) * mm, v(-39.62, 24.15) * mm, v(-40.09, 24.82) * mm]});
            skFitSpline(sketch, "E1528", {"points": [v(-40.09, 24.82) * mm, v(-40.57, 25.52) * mm, v(-41.06, 26.21) * mm, v(-41.56, 26.9) * mm]});
            skLineSegment(sketch, "E1529", {"start": v(-37.85, 18.38) * mm, "end": v(-38.06, 20.94) * mm});
            skLineSegment(sketch, "E1530", {"start": v(-38.06, 20.94) * mm, "end": v(-38.72, 22.8) * mm});
            skFitSpline(sketch, "E1531", {"points": [v(-44.57, 27.88) * mm, v(-44.54, 27.55) * mm, v(-44.53, 27.23) * mm, v(-44.51, 26.9) * mm]});
            skLineSegment(sketch, "E1532", {"start": v(-41.56, 26.9) * mm, "end": v(-43.04, 28.26) * mm});
            skLineSegment(sketch, "E1533", {"start": v(-43.04, 28.26) * mm, "end": v(-44.07, 28.32) * mm});
            skLineSegment(sketch, "E1534", {"start": v(-44.07, 28.32) * mm, "end": v(-44.57, 27.88) * mm});
            skSolve(sketch);
        }
        {
            var Q0;
            Q0=makeQuery(id+"F0.imprint","IMPRINT",FACE,{"disambiguationData":[TD([[makeQuery(id+"F0.imprint","IMPRINT",EDGE,{"derivedFrom":sQuery(id+"F0.wireOp",EDGE,"E124")}),-1.0]])]});
            var Q1;
            Q1=makeQuery(id+"F0.imprint","IMPRINT",FACE,{"disambiguationData":[TD([[makeQuery(id+"F0.imprint","IMPRINT",EDGE,{"derivedFrom":sQuery(id+"F0.wireOp",EDGE,"E132")}),-1.0]])]});
            var Q2;
            Q2=makeQuery(id+"F0.imprint","IMPRINT",FACE,{"disambiguationData":[TD([[makeQuery(id+"F0.imprint","IMPRINT",EDGE,{"derivedFrom":sQuery(id+"F0.wireOp",EDGE,"E144")}),1.0]])]});
            var Q3;
            Q3=makeQuery(id+"F0.imprint","IMPRINT",FACE,{"disambiguationData":[TD([[makeQuery(id+"F0.imprint","IMPRINT",EDGE,{"derivedFrom":sQuery(id+"F0.wireOp",EDGE,"E240")}),-1.0]])]});
            var Q4;
            Q4=makeQuery(id+"F0.imprint","IMPRINT",FACE,{"disambiguationData":[TD([[makeQuery(id+"F0.imprint","IMPRINT",EDGE,{"derivedFrom":sQuery(id+"F0.wireOp",EDGE,"E717")}),-1.0]])]});
            var Q5;
            Q5=makeQuery(id+"F0.imprint","IMPRINT",FACE,{"disambiguationData":[TD([[makeQuery(id+"F0.imprint","IMPRINT",EDGE,{"derivedFrom":sQuery(id+"F0.wireOp",EDGE,"E271")}),1.0]])]});
            var Q6;
            {var subQ3=sQuery(id+"F0.wireOp",EDGE,"E11");Q6=makeQuery(id+"F0.imprint","IMPRINT",FACE,{"disambiguationData":[TD([[makeQuery(id+"F0.imprint","IMPRINT",EDGE,{"derivedFrom":subQ3}),1.0]])]});}
            var Q7;
            Q7=makeQuery(id+"F0.imprint","IMPRINT",FACE,{"disambiguationData":[TD([[makeQuery(id+"F0.imprint","IMPRINT",EDGE,{"derivedFrom":sQuery(id+"F0.wireOp",EDGE,"E717")}),1.0]])]});
            var Q8;
            Q8=makeQuery(id+"F0.imprint","IMPRINT",FACE,{"disambiguationData":[TD([[makeQuery(id+"F0.imprint","IMPRINT",EDGE,{"derivedFrom":sQuery(id+"F0.wireOp",EDGE,"E11")}),-1.0]])]});
            var Q9;
            Q9=makeQuery(id+"F0.imprint","IMPRINT",FACE,{"disambiguationData":[TD([[makeQuery(id+"F0.imprint","IMPRINT",EDGE,{"derivedFrom":sQuery(id+"F0.wireOp",EDGE,"E41")}),-1.0]])]});
            var Q10;
            Q10=makeQuery(id+"F0.imprint","IMPRINT",FACE,{"disambiguationData":[TD([[makeQuery(id+"F0.imprint","IMPRINT",EDGE,{"derivedFrom":sQuery(id+"F0.wireOp",EDGE,"E315")}),1.0]])]});
            var Q11;
            Q11=makeQuery(id+"F0.imprint","IMPRINT",FACE,{"disambiguationData":[TD([[makeQuery(id+"F0.imprint","IMPRINT",EDGE,{"derivedFrom":sQuery(id+"F0.wireOp",EDGE,"E140")}),1.0]])]});
            var Q12;
            Q12=makeQuery(id+"F0.imprint","IMPRINT",FACE,{"disambiguationData":[TD([[makeQuery(id+"F0.imprint","IMPRINT",EDGE,{"derivedFrom":sQuery(id+"F0.wireOp",EDGE,"E1492")}),1.0]])]});
            var Q13;
            Q13=makeQuery(id+"F0.imprint","IMPRINT",FACE,{"disambiguationData":[TD([[makeQuery(id+"F0.imprint","IMPRINT",EDGE,{"derivedFrom":sQuery(id+"F0.wireOp",EDGE,"E434")}),-1.0]])]});
            var Q14;
            Q14=makeQuery(id+"F0.imprint","IMPRINT",FACE,{"disambiguationData":[TD([[makeQuery(id+"F0.imprint","IMPRINT",EDGE,{"derivedFrom":sQuery(id+"F0.wireOp",EDGE,"E635")}),1.0]])]});
            var Q15;
            {var subQ4=sQuery(id+"F0.wireOp",EDGE,"E19");Q15=makeQuery(id+"F0.imprint","IMPRINT",FACE,{"disambiguationData":[TD([[makeQuery(id+"F0.imprint","IMPRINT",EDGE,{"derivedFrom":subQ4}),1.0]])]});}
            var Q16;
            {var subQ3=sQuery(id+"F0.wireOp",EDGE,"E14");Q16=makeQuery(id+"F0.imprint","IMPRINT",FACE,{"disambiguationData":[TD([[makeQuery(id+"F0.imprint","IMPRINT",EDGE,{"derivedFrom":subQ3}),-1.0]])]});}
            var Q17;
            Q17=makeQuery(id+"F0.imprint","IMPRINT",FACE,{"disambiguationData":[TD([[makeQuery(id+"F0.imprint","IMPRINT",EDGE,{"derivedFrom":sQuery(id+"F0.wireOp",EDGE,"E51")}),-1.0]])]});
            var Q18;
            Q18=makeQuery(id+"F0.imprint","IMPRINT",FACE,{"disambiguationData":[TD([[makeQuery(id+"F0.imprint","IMPRINT",EDGE,{"derivedFrom":sQuery(id+"F0.wireOp",EDGE,"E52")}),-1.0]])]});
            var Q19;
            Q19=makeQuery(id+"F0.imprint","IMPRINT",FACE,{"disambiguationData":[TD([[makeQuery(id+"F0.imprint","IMPRINT",EDGE,{"derivedFrom":sQuery(id+"F0.wireOp",EDGE,"E0")}),-1.0]])]});
            var Q20;
            Q20=makeQuery(id+"F0.imprint","IMPRINT",FACE,{"disambiguationData":[TD([[makeQuery(id+"F0.imprint","IMPRINT",EDGE,{"derivedFrom":sQuery(id+"F0.wireOp",EDGE,"E61")}),1.0]])]});
            var Q21;
            Q21=makeQuery(id+"F0.imprint","IMPRINT",FACE,{"disambiguationData":[TD([[makeQuery(id+"F0.imprint","IMPRINT",EDGE,{"derivedFrom":sQuery(id+"F0.wireOp",EDGE,"E1463")}),-1.0]])]});
            var Q22;
            {var subQ6=sQuery(id+"F0.wireOp",EDGE,"E31");Q22=makeQuery(id+"F0.imprint","IMPRINT",FACE,{"disambiguationData":[TD([[makeQuery(id+"F0.imprint","IMPRINT",EDGE,{"derivedFrom":subQ6}),1.0]])]});}
            var Q23;
            Q23=makeQuery(id+"F0.imprint","IMPRINT",FACE,{"disambiguationData":[TD([[makeQuery(id+"F0.imprint","IMPRINT",EDGE,{"derivedFrom":sQuery(id+"F0.wireOp",EDGE,"E61")}),-1.0]])]});
            var Q24;
            Q24=makeQuery(id+"F0.imprint","IMPRINT",FACE,{"disambiguationData":[TD([[makeQuery(id+"F0.imprint","IMPRINT",EDGE,{"derivedFrom":sQuery(id+"F0.wireOp",EDGE,"E122")}),-1.0]])]});
            var Q25;
            Q25=makeQuery(id+"F0.imprint","IMPRINT",FACE,{"disambiguationData":[TD([[makeQuery(id+"F0.imprint","IMPRINT",EDGE,{"derivedFrom":sQuery(id+"F0.wireOp",EDGE,"E765")}),1.0]])]});
            var Q26;
            Q26=makeQuery(id+"F0.imprint","IMPRINT",FACE,{"disambiguationData":[TD([[makeQuery(id+"F0.imprint","IMPRINT",EDGE,{"derivedFrom":sQuery(id+"F0.wireOp",EDGE,"E155")}),1.0]])]});
            var Q27;
            Q27=makeQuery(id+"F0.imprint","IMPRINT",FACE,{"disambiguationData":[TD([[makeQuery(id+"F0.imprint","IMPRINT",EDGE,{"derivedFrom":sQuery(id+"F0.wireOp",EDGE,"E165")}),1.0]])]});
            var Q28;
            Q28=makeQuery(id+"F0.imprint","IMPRINT",FACE,{"disambiguationData":[TD([[makeQuery(id+"F0.imprint","IMPRINT",EDGE,{"derivedFrom":sQuery(id+"F0.wireOp",EDGE,"E262")}),-1.0]])]});
            var Q29;
            {var subQ3=sQuery(id+"F0.wireOp",EDGE,"E15");Q29=makeQuery(id+"F0.imprint","IMPRINT",FACE,{"disambiguationData":[TD([[makeQuery(id+"F0.imprint","IMPRINT",EDGE,{"derivedFrom":subQ3}),1.0]])]});}
            var Q30;
            {var subQ5=sQuery(id+"F0.wireOp",EDGE,"E17");Q30=makeQuery(id+"F0.imprint","IMPRINT",FACE,{"disambiguationData":[TD([[makeQuery(id+"F0.imprint","IMPRINT",EDGE,{"derivedFrom":subQ5}),-1.0]])]});}
            var Q31;
            Q31=makeQuery(id+"F0.imprint","IMPRINT",FACE,{"disambiguationData":[TD([[makeQuery(id+"F0.imprint","IMPRINT",EDGE,{"derivedFrom":sQuery(id+"F0.wireOp",EDGE,"E772")}),-1.0]])]});
            var Q32;
            Q32=makeQuery(id+"F0.imprint","IMPRINT",FACE,{"disambiguationData":[TD([[makeQuery(id+"F0.imprint","IMPRINT",EDGE,{"derivedFrom":sQuery(id+"F0.wireOp",EDGE,"E141")}),1.0]])]});
            var Q33;
            Q33=makeQuery(id+"F0.imprint","IMPRINT",FACE,{"disambiguationData":[TD([[makeQuery(id+"F0.imprint","IMPRINT",EDGE,{"derivedFrom":sQuery(id+"F0.wireOp",EDGE,"E175")}),1.0]])]});
            var Q34;
            Q34=makeQuery(id+"F0.imprint","IMPRINT",FACE,{"disambiguationData":[TD([[makeQuery(id+"F0.imprint","IMPRINT",EDGE,{"derivedFrom":sQuery(id+"F0.wireOp",EDGE,"E338")}),-1.0]])]});
            var Q35;
            Q35=makeQuery(id+"F0.imprint","IMPRINT",FACE,{"disambiguationData":[TD([[makeQuery(id+"F0.imprint","IMPRINT",EDGE,{"derivedFrom":sQuery(id+"F0.wireOp",EDGE,"E387")}),-1.0]])]});
            var Q36;
            {var subQ3=sQuery(id+"F0.wireOp",EDGE,"E27");Q36=makeQuery(id+"F0.imprint","IMPRINT",FACE,{"disambiguationData":[TD([[makeQuery(id+"F0.imprint","IMPRINT",EDGE,{"derivedFrom":subQ3}),-1.0]])]});}
            var Q37;
            {var subQ3=sQuery(id+"F0.wireOp",EDGE,"E37");Q37=makeQuery(id+"F0.imprint","IMPRINT",FACE,{"disambiguationData":[TD([[makeQuery(id+"F0.imprint","IMPRINT",EDGE,{"derivedFrom":subQ3}),-1.0]])]});}
            var Q38;
            Q38=makeQuery(id+"F0.imprint","IMPRINT",FACE,{"disambiguationData":[TD([[makeQuery(id+"F0.imprint","IMPRINT",EDGE,{"derivedFrom":sQuery(id+"F0.wireOp",EDGE,"E307")}),1.0]])]});
            var Q39;
            Q39=makeQuery(id+"F0.imprint","IMPRINT",FACE,{"disambiguationData":[TD([[makeQuery(id+"F0.imprint","IMPRINT",EDGE,{"derivedFrom":sQuery(id+"F0.wireOp",EDGE,"E298")}),1.0]])]});
            var Q40;
            Q40=makeQuery(id+"F0.imprint","IMPRINT",FACE,{"disambiguationData":[TD([[makeQuery(id+"F0.imprint","IMPRINT",EDGE,{"derivedFrom":sQuery(id+"F0.wireOp",EDGE,"E876")}),1.0]])]});
            var Q41;
            Q41=makeQuery(id+"F0.imprint","IMPRINT",FACE,{"disambiguationData":[TD([[makeQuery(id+"F0.imprint","IMPRINT",EDGE,{"derivedFrom":sQuery(id+"F0.wireOp",EDGE,"E856")}),-1.0]])]});
            var Q42;
            Q42=makeQuery(id+"F0.imprint","IMPRINT",FACE,{"disambiguationData":[TD([[makeQuery(id+"F0.imprint","IMPRINT",EDGE,{"derivedFrom":sQuery(id+"F0.wireOp",EDGE,"E841")}),-1.0]])]});
            extrude(context, id + "F1", {"entities" : qUnion([Q0, Q1, Q2, Q3, Q4, Q5, Q6, Q7, Q8, Q9, Q10, Q11, Q12, Q13, Q14, Q15, Q16, Q17, Q18, Q19, Q20, Q21, Q22, Q23, Q24, Q25, Q26, Q27, Q28, Q29, Q30, Q31, Q32, Q33, Q34, Q35, Q36, Q37, Q38, Q39, Q40, Q41, Q42]), "depth" : 25.4 * mm});
        }
        {
            var Q0;
            Q0 = qSketchRegion(id + "F0", true);
            extrude(context, id + "F2", {"entities" : qUnion([Q0]), "operationType" : NewBodyOperationType.ADD, "oppositeDirection" : true, "depth" : 20.44 * mm});
        }
        {
            var Q0;
            Q0=makeQuery(id+"F0.imprint","IMPRINT",FACE,{"disambiguationData":[TD([[makeQuery(id+"F0.imprint","IMPRINT",EDGE,{"derivedFrom":sQuery(id+"F0.wireOp",EDGE,"E175")}),1.0]])]});
            extrude(context, id + "F3", {"entities" : qUnion([Q0]), "operationType" : NewBodyOperationType.ADD, "depth" : 28.58 * mm});
        }
        {
            var Q0;
            Q0=makeQuery(id+"F0.imprint","IMPRINT",FACE,{"disambiguationData":[TD([[makeQuery(id+"F0.imprint","IMPRINT",EDGE,{"derivedFrom":sQuery(id+"F0.wireOp",EDGE,"E124")}),-1.0]])]});
            extrude(context, id + "F4", {"entities" : qUnion([Q0]), "operationType" : NewBodyOperationType.ADD, "depth" : 28.58 * mm});
        }
        {
            var Q0;
            Q0=makeQuery(id+"F0.imprint","IMPRINT",FACE,{"disambiguationData":[TD([[makeQuery(id+"F0.imprint","IMPRINT",EDGE,{"derivedFrom":sQuery(id+"F0.wireOp",EDGE,"E132")}),-1.0]])]});
            extrude(context, id + "F5", {"entities" : qUnion([Q0]), "operationType" : NewBodyOperationType.ADD, "depth" : 28.58 * mm});
        }
        {
            var Q0;
            Q0=makeQuery(id+"F0.imprint","IMPRINT",FACE,{"disambiguationData":[TD([[makeQuery(id+"F0.imprint","IMPRINT",EDGE,{"derivedFrom":sQuery(id+"F0.wireOp",EDGE,"E240")}),-1.0]])]});
            extrude(context, id + "F6", {"entities" : qUnion([Q0]), "operationType" : NewBodyOperationType.ADD, "depth" : 28.58 * mm});
        }
        {
            var Q0;
            Q0=makeQuery(id+"F0.imprint","IMPRINT",FACE,{"disambiguationData":[TD([[makeQuery(id+"F0.imprint","IMPRINT",EDGE,{"derivedFrom":sQuery(id+"F0.wireOp",EDGE,"E271")}),1.0]])]});
            extrude(context, id + "F7", {"entities" : qUnion([Q0]), "operationType" : NewBodyOperationType.ADD, "depth" : 28.58 * mm});
        }
        {
            var Q0;
            Q0=makeQuery(id+"F0.imprint","IMPRINT",FACE,{"disambiguationData":[TD([[makeQuery(id+"F0.imprint","IMPRINT",EDGE,{"derivedFrom":sQuery(id+"F0.wireOp",EDGE,"E315")}),1.0]])]});
            extrude(context, id + "F8", {"entities" : qUnion([Q0]), "operationType" : NewBodyOperationType.ADD, "depth" : 28.58 * mm});
        }
        {
            var Q0;
            Q0=makeQuery(id+"F0.imprint","IMPRINT",FACE,{"disambiguationData":[TD([[makeQuery(id+"F0.imprint","IMPRINT",EDGE,{"derivedFrom":sQuery(id+"F0.wireOp",EDGE,"E338")}),-1.0]])]});
            extrude(context, id + "F9", {"entities" : qUnion([Q0]), "operationType" : NewBodyOperationType.ADD, "depth" : 28.58 * mm});
        }
        {
            var Q0;
            Q0=makeQuery(id+"F0.imprint","IMPRINT",FACE,{"disambiguationData":[TD([[makeQuery(id+"F0.imprint","IMPRINT",EDGE,{"derivedFrom":sQuery(id+"F0.wireOp",EDGE,"E144")}),1.0]])]});
            extrude(context, id + "F10", {"entities" : qUnion([Q0]), "operationType" : NewBodyOperationType.ADD, "depth" : 28.58 * mm});
        }
        {
            var Q0;
            Q0=makeQuery(id+"F0.imprint","IMPRINT",FACE,{"disambiguationData":[TD([[makeQuery(id+"F0.imprint","IMPRINT",EDGE,{"derivedFrom":sQuery(id+"F0.wireOp",EDGE,"E387")}),-1.0]])]});
            extrude(context, id + "F11", {"entities" : qUnion([Q0]), "operationType" : NewBodyOperationType.ADD, "depth" : 28.58 * mm});
        }
        {
            var Q0;
            Q0=makeQuery(id+"F0.imprint","IMPRINT",FACE,{"disambiguationData":[TD([[makeQuery(id+"F0.imprint","IMPRINT",EDGE,{"derivedFrom":sQuery(id+"F0.wireOp",EDGE,"E61")}),-1.0]])]});
            extrude(context, id + "F12", {"entities" : qUnion([Q0]), "operationType" : NewBodyOperationType.ADD, "depth" : 28.58 * mm});
        }
        {
            var Q0;
            Q0=makeQuery(id+"F0.imprint","IMPRINT",FACE,{"disambiguationData":[TD([[makeQuery(id+"F0.imprint","IMPRINT",EDGE,{"derivedFrom":sQuery(id+"F0.wireOp",EDGE,"E52")}),-1.0]])]});
            extrude(context, id + "F13", {"entities" : qUnion([Q0]), "operationType" : NewBodyOperationType.ADD, "depth" : 28.58 * mm});
        }
        {
            var Q0;
            Q0=makeQuery(id+"F0.imprint","IMPRINT",FACE,{"disambiguationData":[TD([[makeQuery(id+"F0.imprint","IMPRINT",EDGE,{"derivedFrom":sQuery(id+"F0.wireOp",EDGE,"E51")}),-1.0]])]});
            extrude(context, id + "F14", {"entities" : qUnion([Q0]), "operationType" : NewBodyOperationType.ADD, "depth" : 28.58 * mm});
        }
        {
            var Q0;
            Q0=makeQuery(id+"F0.imprint","IMPRINT",FACE,{"disambiguationData":[TD([[makeQuery(id+"F0.imprint","IMPRINT",EDGE,{"derivedFrom":sQuery(id+"F0.wireOp",EDGE,"E41")}),-1.0]])]});
            extrude(context, id + "F15", {"entities" : qUnion([Q0]), "operationType" : NewBodyOperationType.ADD, "depth" : 28.58 * mm});
        }
        {
            var Q0;
            {var subQ3=sQuery(id+"F0.wireOp",EDGE,"E14");Q0=makeQuery(id+"F0.imprint","IMPRINT",FACE,{"disambiguationData":[TD([[makeQuery(id+"F0.imprint","IMPRINT",EDGE,{"derivedFrom":subQ3}),-1.0]])]});}
            extrude(context, id + "F16", {"entities" : qUnion([Q0]), "operationType" : NewBodyOperationType.ADD, "depth" : 28.58 * mm});
        }
        {
            var Q0;
            {var subQ3=sQuery(id+"F0.wireOp",EDGE,"E11");Q0=makeQuery(id+"F0.imprint","IMPRINT",FACE,{"disambiguationData":[TD([[makeQuery(id+"F0.imprint","IMPRINT",EDGE,{"derivedFrom":subQ3}),1.0]])]});}
            extrude(context, id + "F17", {"entities" : qUnion([Q0]), "operationType" : NewBodyOperationType.ADD, "depth" : 28.58 * mm});
        }
        {
            var Q0;
            {var subQ4=sQuery(id+"F0.wireOp",EDGE,"E19");Q0=makeQuery(id+"F0.imprint","IMPRINT",FACE,{"disambiguationData":[TD([[makeQuery(id+"F0.imprint","IMPRINT",EDGE,{"derivedFrom":subQ4}),1.0]])]});}
            extrude(context, id + "F18", {"entities" : qUnion([Q0]), "operationType" : NewBodyOperationType.ADD, "depth" : 28.58 * mm});
        }
        {
            var Q0;
            {var subQ3=sQuery(id+"F0.wireOp",EDGE,"E15");Q0=makeQuery(id+"F0.imprint","IMPRINT",FACE,{"disambiguationData":[TD([[makeQuery(id+"F0.imprint","IMPRINT",EDGE,{"derivedFrom":subQ3}),1.0]])]});}
            extrude(context, id + "F19", {"entities" : qUnion([Q0]), "operationType" : NewBodyOperationType.ADD, "depth" : 28.58 * mm});
        }
        {
            var Q0;
            Q0=makeQuery(id+"F0.imprint","IMPRINT",FACE,{"disambiguationData":[TD([[makeQuery(id+"F0.imprint","IMPRINT",EDGE,{"derivedFrom":sQuery(id+"F0.wireOp",EDGE,"E155")}),1.0]])]});
            extrude(context, id + "F20", {"entities" : qUnion([Q0]), "operationType" : NewBodyOperationType.ADD, "depth" : 28.58 * mm});
        }
        {
            var Q0;
            Q0=makeQuery(id+"F0.imprint","IMPRINT",FACE,{"disambiguationData":[TD([[makeQuery(id+"F0.imprint","IMPRINT",EDGE,{"derivedFrom":sQuery(id+"F0.wireOp",EDGE,"E165")}),1.0]])]});
            extrude(context, id + "F21", {"entities" : qUnion([Q0]), "operationType" : NewBodyOperationType.ADD, "depth" : 28.58 * mm});
        }
        {
            var Q0;
            Q0=makeQuery(id+"F0.imprint","IMPRINT",FACE,{"disambiguationData":[TD([[makeQuery(id+"F0.imprint","IMPRINT",EDGE,{"derivedFrom":sQuery(id+"F0.wireOp",EDGE,"E635")}),1.0]])]});
            extrude(context, id + "F22", {"entities" : qUnion([Q0]), "operationType" : NewBodyOperationType.ADD, "depth" : 28.58 * mm});
        }
        {
            var Q0;
            Q0=makeQuery(id+"F0.imprint","IMPRINT",FACE,{"disambiguationData":[TD([[makeQuery(id+"F0.imprint","IMPRINT",EDGE,{"derivedFrom":sQuery(id+"F0.wireOp",EDGE,"E717")}),-1.0]])]});
            extrude(context, id + "F23", {"entities" : qUnion([Q0]), "operationType" : NewBodyOperationType.ADD, "depth" : 28.58 * mm});
        }
        {
            var Q0;
            Q0=makeQuery(id+"F0.imprint","IMPRINT",FACE,{"disambiguationData":[TD([[makeQuery(id+"F0.imprint","IMPRINT",EDGE,{"derivedFrom":sQuery(id+"F0.wireOp",EDGE,"E1463")}),-1.0]])]});
            extrude(context, id + "F24", {"entities" : qUnion([Q0]), "operationType" : NewBodyOperationType.ADD, "depth" : 28.58 * mm});
        }
        {
            var Q0;
            Q0=makeQuery(id+"F0.imprint","IMPRINT",FACE,{"disambiguationData":[TD([[makeQuery(id+"F0.imprint","IMPRINT",EDGE,{"derivedFrom":sQuery(id+"F0.wireOp",EDGE,"E1492")}),1.0]])]});
            extrude(context, id + "F25", {"entities" : qUnion([Q0]), "operationType" : NewBodyOperationType.ADD, "depth" : 28.58 * mm});
        }
        {
            var Q0;
            Q0=makeQuery(id+"F0.imprint","IMPRINT",FACE,{"disambiguationData":[TD([[makeQuery(id+"F0.imprint","IMPRINT",EDGE,{"derivedFrom":sQuery(id+"F0.wireOp",EDGE,"E772")}),-1.0]])]});
            extrude(context, id + "F26", {"entities" : qUnion([Q0]), "operationType" : NewBodyOperationType.ADD, "depth" : 28.58 * mm});
        }
        {
            var Q0;
            Q0=makeQuery(id+"F0.imprint","IMPRINT",FACE,{"disambiguationData":[TD([[makeQuery(id+"F0.imprint","IMPRINT",EDGE,{"derivedFrom":sQuery(id+"F0.wireOp",EDGE,"E856")}),-1.0]])]});
            extrude(context, id + "F27", {"entities" : qUnion([Q0]), "operationType" : NewBodyOperationType.ADD, "depth" : 28.58 * mm});
        }
        {
            var Q0;
            Q0=makeQuery(id+"F0.imprint","IMPRINT",FACE,{"disambiguationData":[TD([[makeQuery(id+"F0.imprint","IMPRINT",EDGE,{"derivedFrom":sQuery(id+"F0.wireOp",EDGE,"E841")}),-1.0]])]});
            var Q1;
            Q1=makeQuery(id+"F0.imprint","IMPRINT",FACE,{"disambiguationData":[TD([[makeQuery(id+"F0.imprint","IMPRINT",EDGE,{"derivedFrom":sQuery(id+"F0.wireOp",EDGE,"E876")}),1.0]])]});
            extrude(context, id + "F28", {"entities" : qUnion([Q0, Q1]), "operationType" : NewBodyOperationType.ADD, "depth" : 28.58 * mm});
        }
        {
            var Q0;
            Q0=makeQuery(id+"F0.imprint","IMPRINT",FACE,{"disambiguationData":[TD([[makeQuery(id+"F0.imprint","IMPRINT",EDGE,{"derivedFrom":sQuery(id+"F0.wireOp",EDGE,"E876")}),1.0]])]});
            extrude(context, id + "F29", {"entities" : qUnion([Q0]), "operationType" : NewBodyOperationType.ADD, "depth" : 28.58 * mm});
        }
        {
            var Q0;
            Q0=makeQuery(id+"F0.imprint","IMPRINT",FACE,{"disambiguationData":[TD([[makeQuery(id+"F0.imprint","IMPRINT",EDGE,{"derivedFrom":sQuery(id+"F0.wireOp",EDGE,"E434")}),-1.0]])]});
            extrude(context, id + "F30", {"entities" : qUnion([Q0]), "operationType" : NewBodyOperationType.ADD, "depth" : 28.58 * mm});
        }
    });
